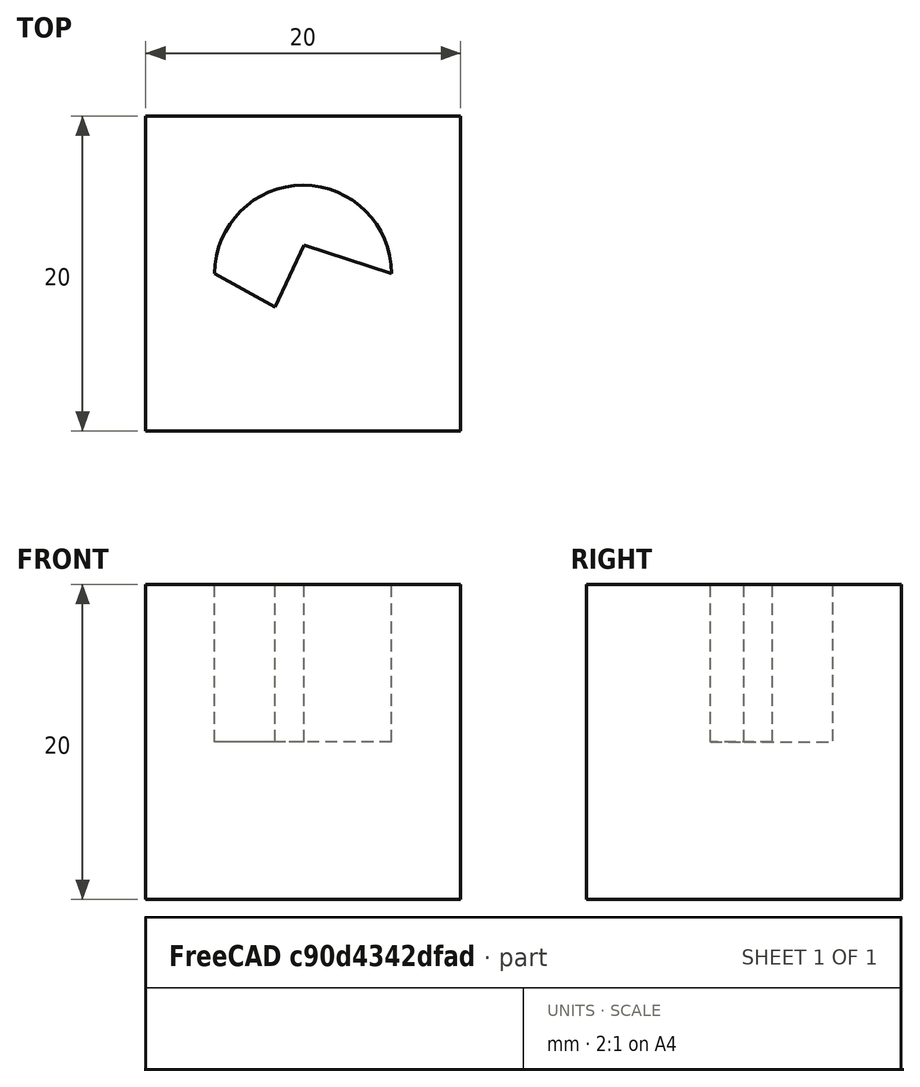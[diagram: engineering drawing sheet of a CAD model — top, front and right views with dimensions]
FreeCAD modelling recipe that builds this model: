
FCSTD DOCUMENT  (FreeCAD 0.21R33694 (Git))
Label: extrudeLimitation-1
License: All rights reserved
LicenseURL: http://en.wikipedia.org/wiki/All_rights_reserved
objects: App::DocumentObjectGroupPython×1248, App::Part×2, Part::FeaturePython×1, Sketcher::SketchObject×1, Part::Extrusion×1
note: 3 computed .brp shape members not serialized (recipe doc carries the construction recipe); baked Part::Feature solids carry a one-line shape summary decoded from their .brp

FEATURE [App::DocumentObjectGroupPython] HALFPI  # scripted group (container) (typed FeaturePython)
  name = HALFPI
  value = pi/2.
FEATURE [App::DocumentObjectGroupPython] PI  # scripted group (container) (typed FeaturePython)
  name = PI
  value = 1.*pi
FEATURE [App::DocumentObjectGroupPython] TWOPI  # scripted group (container) (typed FeaturePython)
  name = TWOPI
  value = 2.*pi
FEATURE [App::DocumentObjectGroupPython] Constants  # scripted group (container) (typed FeaturePython)
  Group = -> [HALFPI,PI,TWOPI]
FEATURE [App::DocumentObjectGroupPython] Variables  # scripted group (container) (typed FeaturePython)
FEATURE [App::DocumentObjectGroupPython] Quantities  # scripted group (container) (typed FeaturePython)
FEATURE [App::DocumentObjectGroupPython] Isotopes  # scripted group (container) (typed FeaturePython)
FEATURE [App::DocumentObjectGroupPython] Elements  # scripted group (container) (typed FeaturePython)
FEATURE [App::DocumentObjectGroupPython] G4Isotopes  # scripted group (container) (typed FeaturePython)
FEATURE [App::DocumentObjectGroupPython] H_element  # scripted group (container) (typed FeaturePython)
  Z = 1
  atom_value = 1.008
  formula = H
  name = H_element
FEATURE [App::DocumentObjectGroupPython] He_element  # scripted group (container) (typed FeaturePython)
  Z = 2
  atom_value = 4.0026
  formula = He
  name = He_element
FEATURE [App::DocumentObjectGroupPython] Li_element  # scripted group (container) (typed FeaturePython)
  Z = 3
  atom_value = 6.94
  formula = Li
  name = Li_element
FEATURE [App::DocumentObjectGroupPython] Be_element  # scripted group (container) (typed FeaturePython)
  Z = 4
  atom_value = 9.01218
  formula = Be
  name = Be_element
FEATURE [App::DocumentObjectGroupPython] B_element  # scripted group (container) (typed FeaturePython)
  Z = 5
  atom_value = 10.81
  formula = B
  name = B_element
FEATURE [App::DocumentObjectGroupPython] C_element  # scripted group (container) (typed FeaturePython)
  Z = 6
  atom_value = 12.011
  formula = C
  name = C_element
FEATURE [App::DocumentObjectGroupPython] N_element  # scripted group (container) (typed FeaturePython)
  Z = 7
  atom_value = 14.007
  formula = N
  name = N_element
FEATURE [App::DocumentObjectGroupPython] O_element  # scripted group (container) (typed FeaturePython)
  Z = 8
  atom_value = 15.999
  formula = O
  name = O_element
FEATURE [App::DocumentObjectGroupPython] F_element  # scripted group (container) (typed FeaturePython)
  Z = 9
  atom_value = 18.9984
  formula = F
  name = F_element
FEATURE [App::DocumentObjectGroupPython] Ne_element  # scripted group (container) (typed FeaturePython)
  Z = 10
  atom_value = 20.1797
  formula = Ne
  name = Ne_element
FEATURE [App::DocumentObjectGroupPython] Na_element  # scripted group (container) (typed FeaturePython)
  Z = 11
  atom_value = 22.9898
  formula = Na
  name = Na_element
FEATURE [App::DocumentObjectGroupPython] Mg_element  # scripted group (container) (typed FeaturePython)
  Z = 12
  atom_value = 24.305
  formula = Mg
  name = Mg_element
FEATURE [App::DocumentObjectGroupPython] Al_element  # scripted group (container) (typed FeaturePython)
  Z = 13
  atom_value = 26.9815
  formula = Al
  name = Al_element
FEATURE [App::DocumentObjectGroupPython] Si_element  # scripted group (container) (typed FeaturePython)
  Z = 14
  atom_value = 28.085
  formula = Si
  name = Si_element
FEATURE [App::DocumentObjectGroupPython] P_element  # scripted group (container) (typed FeaturePython)
  Z = 15
  atom_value = 30.9738
  formula = P
  name = P_element
FEATURE [App::DocumentObjectGroupPython] S_element  # scripted group (container) (typed FeaturePython)
  Z = 16
  atom_value = 32.06
  formula = S
  name = S_element
FEATURE [App::DocumentObjectGroupPython] Cl_element  # scripted group (container) (typed FeaturePython)
  Z = 17
  atom_value = 35.45
  formula = Cl
  name = Cl_element
FEATURE [App::DocumentObjectGroupPython] Ar_element  # scripted group (container) (typed FeaturePython)
  Z = 18
  atom_value = 39.95
  formula = Ar
  name = Ar_element
FEATURE [App::DocumentObjectGroupPython] K_element  # scripted group (container) (typed FeaturePython)
  Z = 19
  atom_value = 39.0983
  formula = K
  name = K_element
FEATURE [App::DocumentObjectGroupPython] Ca_element  # scripted group (container) (typed FeaturePython)
  Z = 20
  atom_value = 40.078
  formula = Ca
  name = Ca_element
FEATURE [App::DocumentObjectGroupPython] Sc_element  # scripted group (container) (typed FeaturePython)
  Z = 21
  atom_value = 44.9559
  formula = Sc
  name = Sc_element
FEATURE [App::DocumentObjectGroupPython] Ti_element  # scripted group (container) (typed FeaturePython)
  Z = 22
  atom_value = 47.867
  formula = Ti
  name = Ti_element
FEATURE [App::DocumentObjectGroupPython] V_element  # scripted group (container) (typed FeaturePython)
  Z = 23
  atom_value = 50.9415
  formula = V
  name = V_element
FEATURE [App::DocumentObjectGroupPython] Cr_element  # scripted group (container) (typed FeaturePython)
  Z = 24
  atom_value = 51.9961
  formula = Cr
  name = Cr_element
FEATURE [App::DocumentObjectGroupPython] Mn_element  # scripted group (container) (typed FeaturePython)
  Z = 25
  atom_value = 54.938
  formula = Mn
  name = Mn_element
FEATURE [App::DocumentObjectGroupPython] Fe_element  # scripted group (container) (typed FeaturePython)
  Z = 26
  atom_value = 55.845
  formula = Fe
  name = Fe_element
FEATURE [App::DocumentObjectGroupPython] Co_element  # scripted group (container) (typed FeaturePython)
  Z = 27
  atom_value = 58.9332
  formula = Co
  name = Co_element
FEATURE [App::DocumentObjectGroupPython] Ni_element  # scripted group (container) (typed FeaturePython)
  Z = 28
  atom_value = 58.6934
  formula = Ni
  name = Ni_element
FEATURE [App::DocumentObjectGroupPython] Cu_element  # scripted group (container) (typed FeaturePython)
  Z = 29
  atom_value = 63.546
  formula = Cu
  name = Cu_element
FEATURE [App::DocumentObjectGroupPython] Zn_element  # scripted group (container) (typed FeaturePython)
  Z = 30
  atom_value = 65.38
  formula = Zn
  name = Zn_element
FEATURE [App::DocumentObjectGroupPython] Ga_element  # scripted group (container) (typed FeaturePython)
  Z = 31
  atom_value = 69.723
  formula = Ga
  name = Ga_element
FEATURE [App::DocumentObjectGroupPython] Ge_element  # scripted group (container) (typed FeaturePython)
  Z = 32
  atom_value = 72.63
  formula = Ge
  name = Ge_element
FEATURE [App::DocumentObjectGroupPython] As_element  # scripted group (container) (typed FeaturePython)
  Z = 33
  atom_value = 74.9216
  formula = As
  name = As_element
FEATURE [App::DocumentObjectGroupPython] Se_element  # scripted group (container) (typed FeaturePython)
  Z = 34
  atom_value = 78.971
  formula = Se
  name = Se_element
FEATURE [App::DocumentObjectGroupPython] Br_element  # scripted group (container) (typed FeaturePython)
  Z = 35
  atom_value = 79.904
  formula = Br
  name = Br_element
FEATURE [App::DocumentObjectGroupPython] Kr_element  # scripted group (container) (typed FeaturePython)
  Z = 36
  atom_value = 83.798
  formula = Kr
  name = Kr_element
FEATURE [App::DocumentObjectGroupPython] Rb_element  # scripted group (container) (typed FeaturePython)
  Z = 37
  atom_value = 85.4678
  formula = Rb
  name = Rb_element
FEATURE [App::DocumentObjectGroupPython] Sr_element  # scripted group (container) (typed FeaturePython)
  Z = 38
  atom_value = 87.62
  formula = Sr
  name = Sr_element
FEATURE [App::DocumentObjectGroupPython] Y_element  # scripted group (container) (typed FeaturePython)
  Z = 39
  atom_value = 88.9058
  formula = Y
  name = Y_element
FEATURE [App::DocumentObjectGroupPython] Zr_element  # scripted group (container) (typed FeaturePython)
  Z = 40
  atom_value = 91.224
  formula = Zr
  name = Zr_element
FEATURE [App::DocumentObjectGroupPython] Nb_element  # scripted group (container) (typed FeaturePython)
  Z = 41
  atom_value = 92.9064
  formula = Nb
  name = Nb_element
FEATURE [App::DocumentObjectGroupPython] Mo_element  # scripted group (container) (typed FeaturePython)
  Z = 42
  atom_value = 95.95
  formula = Mo
  name = Mo_element
FEATURE [App::DocumentObjectGroupPython] Tc_element  # scripted group (container) (typed FeaturePython)
  Z = 43
  atom_value = 97
  formula = Tc
  name = Tc_element
FEATURE [App::DocumentObjectGroupPython] Ru_element  # scripted group (container) (typed FeaturePython)
  Z = 44
  atom_value = 101.07
  formula = Ru
  name = Ru_element
FEATURE [App::DocumentObjectGroupPython] Rh_element  # scripted group (container) (typed FeaturePython)
  Z = 45
  atom_value = 102.905
  formula = Rh
  name = Rh_element
FEATURE [App::DocumentObjectGroupPython] Pd_element  # scripted group (container) (typed FeaturePython)
  Z = 46
  atom_value = 106.42
  formula = Pd
  name = Pd_element
FEATURE [App::DocumentObjectGroupPython] Ag_element  # scripted group (container) (typed FeaturePython)
  Z = 47
  atom_value = 107.868
  formula = Ag
  name = Ag_element
FEATURE [App::DocumentObjectGroupPython] Cd_element  # scripted group (container) (typed FeaturePython)
  Z = 48
  atom_value = 112.414
  formula = Cd
  name = Cd_element
FEATURE [App::DocumentObjectGroupPython] In_element  # scripted group (container) (typed FeaturePython)
  Z = 49
  atom_value = 114.818
  formula = In
  name = In_element
FEATURE [App::DocumentObjectGroupPython] Sn_element  # scripted group (container) (typed FeaturePython)
  Z = 50
  atom_value = 118.71
  formula = Sn
  name = Sn_element
FEATURE [App::DocumentObjectGroupPython] Sb_element  # scripted group (container) (typed FeaturePython)
  Z = 51
  atom_value = 121.76
  formula = Sb
  name = Sb_element
FEATURE [App::DocumentObjectGroupPython] Te_element  # scripted group (container) (typed FeaturePython)
  Z = 52
  atom_value = 127.6
  formula = Te
  name = Te_element
FEATURE [App::DocumentObjectGroupPython] I_element  # scripted group (container) (typed FeaturePython)
  Z = 53
  atom_value = 126.904
  formula = I
  name = I_element
FEATURE [App::DocumentObjectGroupPython] Xe_element  # scripted group (container) (typed FeaturePython)
  Z = 54
  atom_value = 131.293
  formula = Xe
  name = Xe_element
FEATURE [App::DocumentObjectGroupPython] Cs_element  # scripted group (container) (typed FeaturePython)
  Z = 55
  atom_value = 132.905
  formula = Cs
  name = Cs_element
FEATURE [App::DocumentObjectGroupPython] Ba_element  # scripted group (container) (typed FeaturePython)
  Z = 56
  atom_value = 137.327
  formula = Ba
  name = Ba_element
FEATURE [App::DocumentObjectGroupPython] La_element  # scripted group (container) (typed FeaturePython)
  Z = 57
  atom_value = 138.905
  formula = La
  name = La_element
FEATURE [App::DocumentObjectGroupPython] Ce_element  # scripted group (container) (typed FeaturePython)
  Z = 58
  atom_value = 140.116
  formula = Ce
  name = Ce_element
FEATURE [App::DocumentObjectGroupPython] Pr_element  # scripted group (container) (typed FeaturePython)
  Z = 59
  atom_value = 140.908
  formula = Pr
  name = Pr_element
FEATURE [App::DocumentObjectGroupPython] Nd_element  # scripted group (container) (typed FeaturePython)
  Z = 60
  atom_value = 144.242
  formula = Nd
  name = Nd_element
FEATURE [App::DocumentObjectGroupPython] Pm_element  # scripted group (container) (typed FeaturePython)
  Z = 61
  atom_value = 145
  formula = Pm
  name = Pm_element
FEATURE [App::DocumentObjectGroupPython] Sm_element  # scripted group (container) (typed FeaturePython)
  Z = 62
  atom_value = 150.36
  formula = Sm
  name = Sm_element
FEATURE [App::DocumentObjectGroupPython] Eu_element  # scripted group (container) (typed FeaturePython)
  Z = 63
  atom_value = 151.964
  formula = Eu
  name = Eu_element
FEATURE [App::DocumentObjectGroupPython] Gd_element  # scripted group (container) (typed FeaturePython)
  Z = 64
  atom_value = 157.25
  formula = Gd
  name = Gd_element
FEATURE [App::DocumentObjectGroupPython] Tb_element  # scripted group (container) (typed FeaturePython)
  Z = 65
  atom_value = 158.925
  formula = Tb
  name = Tb_element
FEATURE [App::DocumentObjectGroupPython] Dy_element  # scripted group (container) (typed FeaturePython)
  Z = 66
  atom_value = 162.5
  formula = Dy
  name = Dy_element
FEATURE [App::DocumentObjectGroupPython] Ho_element  # scripted group (container) (typed FeaturePython)
  Z = 67
  atom_value = 164.93
  formula = Ho
  name = Ho_element
FEATURE [App::DocumentObjectGroupPython] Er_element  # scripted group (container) (typed FeaturePython)
  Z = 68
  atom_value = 167.259
  formula = Er
  name = Er_element
FEATURE [App::DocumentObjectGroupPython] Tm_element  # scripted group (container) (typed FeaturePython)
  Z = 69
  atom_value = 168.934
  formula = Tm
  name = Tm_element
FEATURE [App::DocumentObjectGroupPython] Yb_element  # scripted group (container) (typed FeaturePython)
  Z = 70
  atom_value = 173.045
  formula = Yb
  name = Yb_element
FEATURE [App::DocumentObjectGroupPython] Lu_element  # scripted group (container) (typed FeaturePython)
  Z = 71
  atom_value = 174.967
  formula = Lu
  name = Lu_element
FEATURE [App::DocumentObjectGroupPython] Hf_element  # scripted group (container) (typed FeaturePython)
  Z = 72
  atom_value = 178.49
  formula = Hf
  name = Hf_element
FEATURE [App::DocumentObjectGroupPython] Ta_element  # scripted group (container) (typed FeaturePython)
  Z = 73
  atom_value = 180.948
  formula = Ta
  name = Ta_element
FEATURE [App::DocumentObjectGroupPython] W_element  # scripted group (container) (typed FeaturePython)
  Z = 74
  atom_value = 183.84
  formula = W
  name = W_element
FEATURE [App::DocumentObjectGroupPython] Re_element  # scripted group (container) (typed FeaturePython)
  Z = 75
  atom_value = 186.207
  formula = Re
  name = Re_element
FEATURE [App::DocumentObjectGroupPython] Os_element  # scripted group (container) (typed FeaturePython)
  Z = 76
  atom_value = 190.23
  formula = Os
  name = Os_element
FEATURE [App::DocumentObjectGroupPython] Ir_element  # scripted group (container) (typed FeaturePython)
  Z = 77
  atom_value = 192.217
  formula = Ir
  name = Ir_element
FEATURE [App::DocumentObjectGroupPython] Pt_element  # scripted group (container) (typed FeaturePython)
  Z = 78
  atom_value = 195.084
  formula = Pt
  name = Pt_element
FEATURE [App::DocumentObjectGroupPython] Au_element  # scripted group (container) (typed FeaturePython)
  Z = 79
  atom_value = 196.967
  formula = Au
  name = Au_element
FEATURE [App::DocumentObjectGroupPython] Hg_element  # scripted group (container) (typed FeaturePython)
  Z = 80
  atom_value = 200.592
  formula = Hg
  name = Hg_element
FEATURE [App::DocumentObjectGroupPython] Tl_element  # scripted group (container) (typed FeaturePython)
  Z = 81
  atom_value = 204.38
  formula = Tl
  name = Tl_element
FEATURE [App::DocumentObjectGroupPython] Pb_element  # scripted group (container) (typed FeaturePython)
  Z = 82
  atom_value = 207.2
  formula = Pb
  name = Pb_element
FEATURE [App::DocumentObjectGroupPython] Bi_element  # scripted group (container) (typed FeaturePython)
  Z = 83
  atom_value = 208.98
  formula = Bi
  name = Bi_element
FEATURE [App::DocumentObjectGroupPython] Po_element  # scripted group (container) (typed FeaturePython)
  Z = 84
  atom_value = 209
  formula = Po
  name = Po_element
FEATURE [App::DocumentObjectGroupPython] At_element  # scripted group (container) (typed FeaturePython)
  Z = 85
  atom_value = 210
  formula = At
  name = At_element
FEATURE [App::DocumentObjectGroupPython] Rn_element  # scripted group (container) (typed FeaturePython)
  Z = 86
  atom_value = 222
  formula = Rn
  name = Rn_element
FEATURE [App::DocumentObjectGroupPython] Fr_element  # scripted group (container) (typed FeaturePython)
  Z = 87
  atom_value = 223
  formula = Fr
  name = Fr_element
FEATURE [App::DocumentObjectGroupPython] Ra_element  # scripted group (container) (typed FeaturePython)
  Z = 88
  atom_value = 226
  formula = Ra
  name = Ra_element
FEATURE [App::DocumentObjectGroupPython] Ac_element  # scripted group (container) (typed FeaturePython)
  Z = 89
  atom_value = 227
  formula = Ac
  name = Ac_element
FEATURE [App::DocumentObjectGroupPython] Th_element  # scripted group (container) (typed FeaturePython)
  Z = 90
  atom_value = 232.038
  formula = Th
  name = Th_element
FEATURE [App::DocumentObjectGroupPython] Pa_element  # scripted group (container) (typed FeaturePython)
  Z = 91
  atom_value = 231.036
  formula = Pa
  name = Pa_element
FEATURE [App::DocumentObjectGroupPython] U_element  # scripted group (container) (typed FeaturePython)
  Z = 92
  atom_value = 238.029
  formula = U
  name = U_element
FEATURE [App::DocumentObjectGroupPython] Np_element  # scripted group (container) (typed FeaturePython)
  Z = 93
  atom_value = 237
  formula = Np
  name = Np_element
FEATURE [App::DocumentObjectGroupPython] Pu_element  # scripted group (container) (typed FeaturePython)
  Z = 94
  atom_value = 244
  formula = Pu
  name = Pu_element
FEATURE [App::DocumentObjectGroupPython] Am_element  # scripted group (container) (typed FeaturePython)
  Z = 95
  atom_value = 243
  formula = Am
  name = Am_element
FEATURE [App::DocumentObjectGroupPython] Cm_element  # scripted group (container) (typed FeaturePython)
  Z = 96
  atom_value = 247
  formula = Cm
  name = Cm_element
FEATURE [App::DocumentObjectGroupPython] Bk_element  # scripted group (container) (typed FeaturePython)
  Z = 97
  atom_value = 247
  formula = Bk
  name = Bk_element
FEATURE [App::DocumentObjectGroupPython] Cf_element  # scripted group (container) (typed FeaturePython)
  Z = 98
  atom_value = 251
  formula = Cf
  name = Cf_element
FEATURE [App::DocumentObjectGroupPython] G4Elements  # scripted group (container) (typed FeaturePython)
  Group = -> [H_element,He_element,Li_element,Be_element,B_element,C_element,N_element,O_element,F_element,Ne_element,Na_element,Mg_element,Al_element,Si_element,P_element,S_element,Cl_element,Ar_element,K_element,Ca_element,Sc_element,Ti_element,V_element,Cr_element,Mn_element,Fe_element,Co_element,Ni_element,Cu_element,Zn_element,Ga_element,Ge_element,As_element,Se_element,Br_element,Kr_element,Rb_element,+61 more]
FEATURE [App::DocumentObjectGroupPython] H_element001  label="H_element : 0.101"  # scripted group (container) (typed FeaturePython)
  n = 0.101327
FEATURE [App::DocumentObjectGroupPython] C_element001  label="C_element : 0.775"  # scripted group (container) (typed FeaturePython)
  n = 0.7755
FEATURE [App::DocumentObjectGroupPython] N_element001  label="N_element : 0.035"  # scripted group (container) (typed FeaturePython)
  n = 0.035057
FEATURE [App::DocumentObjectGroupPython] O_element001  label="O_element : 0.052"  # scripted group (container) (typed FeaturePython)
  n = 0.0523159
FEATURE [App::DocumentObjectGroupPython] F_element001  label="F_element : 0.017"  # scripted group (container) (typed FeaturePython)
  n = 0.017422
FEATURE [App::DocumentObjectGroupPython] Ca_element001  label="Ca_element : 0.018"  # scripted group (container) (typed FeaturePython)
  n = 0.018378
FEATURE [App::DocumentObjectGroupPython] G4_A_150_TISSUE  label="G4_A-150_TISSUE"  # scripted group (container) (typed FeaturePython)
  Dunit = g/cm3
  Dvalue = 1.127
  Group = -> [H_element001,C_element001,N_element001,O_element001,F_element001,Ca_element001]
  conduct = 2
  density = 1
  expand = 3
  formula = G4_A-150_TISSUE
  name = G4_A-150_TISSUE
  specific = 4
FEATURE [App::DocumentObjectGroupPython] C_element002  label="C_element : 3"  # scripted group (container) (typed FeaturePython)
  n = 3
  ref = C_element
FEATURE [App::DocumentObjectGroupPython] H_element002  label="H_element : 6"  # scripted group (container) (typed FeaturePython)
  n = 6
  ref = H_element
FEATURE [App::DocumentObjectGroupPython] O_element002  label="O_element : 1"  # scripted group (container) (typed FeaturePython)
  n = 1
  ref = O_element
FEATURE [App::DocumentObjectGroupPython] G4_ACETONE  # scripted group (container) (typed FeaturePython)
  Dunit = g/cm3
  Dvalue = 0.7899
  Group = -> [C_element002,H_element002,O_element002]
  conduct = 2
  density = 1
  expand = 3
  formula = G4_ACETONE
  name = G4_ACETONE
  specific = 4
FEATURE [App::DocumentObjectGroupPython] C_element003  label="C_element : 2"  # scripted group (container) (typed FeaturePython)
  n = 2
  ref = C_element
FEATURE [App::DocumentObjectGroupPython] H_element003  label="H_element : 2"  # scripted group (container) (typed FeaturePython)
  n = 2
  ref = H_element
FEATURE [App::DocumentObjectGroupPython] G4_ACETYLENE  # scripted group (container) (typed FeaturePython)
  Dunit = g/cm3
  Dvalue = 0.0010967
  Group = -> [C_element003,H_element003]
  conduct = 2
  density = 1
  expand = 3
  formula = G4_ACETYLENE
  name = G4_ACETYLENE
  specific = 4
FEATURE [App::DocumentObjectGroupPython] C_element004  label="C_element : 5"  # scripted group (container) (typed FeaturePython)
  n = 5
  ref = C_element
FEATURE [App::DocumentObjectGroupPython] H_element004  label="H_element : 5"  # scripted group (container) (typed FeaturePython)
  n = 5
  ref = H_element
FEATURE [App::DocumentObjectGroupPython] N_element002  label="N_element : 5"  # scripted group (container) (typed FeaturePython)
  n = 5
  ref = N_element
FEATURE [App::DocumentObjectGroupPython] G4_ADENINE  # scripted group (container) (typed FeaturePython)
  Dunit = g/cm3
  Dvalue = 1.6
  Group = -> [C_element004,H_element004,N_element002]
  conduct = 2
  density = 1
  expand = 3
  formula = G4_ADENINE
  name = G4_ADENINE
  specific = 4
FEATURE [App::DocumentObjectGroupPython] H_element005  label="H_element : 0.114"  # scripted group (container) (typed FeaturePython)
  n = 0.114
FEATURE [App::DocumentObjectGroupPython] C_element005  label="C_element : 0.598"  # scripted group (container) (typed FeaturePython)
  n = 0.598
FEATURE [App::DocumentObjectGroupPython] N_element003  label="N_element : 0.007"  # scripted group (container) (typed FeaturePython)
  n = 0.007
FEATURE [App::DocumentObjectGroupPython] O_element003  label="O_element : 0.278"  # scripted group (container) (typed FeaturePython)
  n = 0.278
FEATURE [App::DocumentObjectGroupPython] Na_element001  label="Na_element : 0.001"  # scripted group (container) (typed FeaturePython)
  n = 0.001
FEATURE [App::DocumentObjectGroupPython] S_element001  label="S_element : 0.001"  # scripted group (container) (typed FeaturePython)
  n = 0.001
FEATURE [App::DocumentObjectGroupPython] Cl_element001  label="Cl_element : 0.001"  # scripted group (container) (typed FeaturePython)
  n = 0.001
FEATURE [App::DocumentObjectGroupPython] G4_ADIPOSE_TISSUE_ICRP  # scripted group (container) (typed FeaturePython)
  Dunit = g/cm3
  Dvalue = 0.95
  Group = -> [H_element005,C_element005,N_element003,O_element003,Na_element001,S_element001,Cl_element001]
  conduct = 2
  density = 1
  expand = 3
  formula = G4_ADIPOSE_TISSUE_ICRP
  name = G4_ADIPOSE_TISSUE_ICRP
  specific = 4
FEATURE [App::DocumentObjectGroupPython] C_element006  label="C_element : 0.000"  # scripted group (container) (typed FeaturePython)
  n = 0.000124
FEATURE [App::DocumentObjectGroupPython] N_element004  label="N_element : 0.755"  # scripted group (container) (typed FeaturePython)
  n = 0.755268
FEATURE [App::DocumentObjectGroupPython] O_element004  label="O_element : 0.232"  # scripted group (container) (typed FeaturePython)
  n = 0.231781
FEATURE [App::DocumentObjectGroupPython] Ar_element001  label="Ar_element : 0.013"  # scripted group (container) (typed FeaturePython)
  n = 0.012827
FEATURE [App::DocumentObjectGroupPython] G4_AIR  # scripted group (container) (typed FeaturePython)
  Dunit = g/cm3
  Dvalue = 0.00120479
  Group = -> [C_element006,N_element004,O_element004,Ar_element001]
  conduct = 2
  density = 1
  expand = 3
  formula = G4_AIR
  name = G4_AIR
  specific = 4
FEATURE [App::DocumentObjectGroupPython] C_element007  label="C_element : 006"  # scripted group (container) (typed FeaturePython)
  n = 3
  ref = C_element
FEATURE [App::DocumentObjectGroupPython] H_element006  label="H_element : 7"  # scripted group (container) (typed FeaturePython)
  n = 7
  ref = H_element
FEATURE [App::DocumentObjectGroupPython] N_element005  label="N_element : 1"  # scripted group (container) (typed FeaturePython)
  n = 1
  ref = N_element
FEATURE [App::DocumentObjectGroupPython] O_element005  label="O_element : 2"  # scripted group (container) (typed FeaturePython)
  n = 2
  ref = O_element
FEATURE [App::DocumentObjectGroupPython] G4_ALANINE  # scripted group (container) (typed FeaturePython)
  Dunit = g/cm3
  Dvalue = 1.42
  Group = -> [C_element007,H_element006,N_element005,O_element005]
  conduct = 2
  density = 1
  expand = 3
  formula = G4_ALANINE
  name = G4_ALANINE
  specific = 4
FEATURE [App::DocumentObjectGroupPython] Al_element001  label="Al_element : 2"  # scripted group (container) (typed FeaturePython)
  n = 2
  ref = Al_element
FEATURE [App::DocumentObjectGroupPython] O_element006  label="O_element : 3"  # scripted group (container) (typed FeaturePython)
  n = 3
  ref = O_element
FEATURE [App::DocumentObjectGroupPython] G4_ALUMINUM_OXIDE  # scripted group (container) (typed FeaturePython)
  Dunit = g/cm3
  Dvalue = 3.97
  Group = -> [Al_element001,O_element006]
  conduct = 2
  density = 1
  expand = 3
  formula = G4_ALUMINUM_OXIDE
  name = G4_ALUMINUM_OXIDE
  specific = 4
FEATURE [App::DocumentObjectGroupPython] H_element007  label="H_element : 0.106"  # scripted group (container) (typed FeaturePython)
  n = 0.10593
FEATURE [App::DocumentObjectGroupPython] C_element008  label="C_element : 0.789"  # scripted group (container) (typed FeaturePython)
  n = 0.788974
FEATURE [App::DocumentObjectGroupPython] O_element007  label="O_element : 0.105"  # scripted group (container) (typed FeaturePython)
  n = 0.105096
FEATURE [App::DocumentObjectGroupPython] G4_AMBER  # scripted group (container) (typed FeaturePython)
  Dunit = g/cm3
  Dvalue = 1.1
  Group = -> [H_element007,C_element008,O_element007]
  conduct = 2
  density = 1
  expand = 3
  formula = G4_AMBER
  name = G4_AMBER
  specific = 4
FEATURE [App::DocumentObjectGroupPython] N_element006  label="N_element : 006"  # scripted group (container) (typed FeaturePython)
  n = 1
  ref = N_element
FEATURE [App::DocumentObjectGroupPython] H_element008  label="H_element : 3"  # scripted group (container) (typed FeaturePython)
  n = 3
  ref = H_element
FEATURE [App::DocumentObjectGroupPython] G4_AMMONIA  # scripted group (container) (typed FeaturePython)
  Dunit = g/cm3
  Dvalue = 0.000826019
  Group = -> [N_element006,H_element008]
  conduct = 2
  density = 1
  expand = 3
  formula = G4_AMMONIA
  name = G4_AMMONIA
  specific = 4
FEATURE [App::DocumentObjectGroupPython] C_element009  label="C_element : 6"  # scripted group (container) (typed FeaturePython)
  n = 6
  ref = C_element
FEATURE [App::DocumentObjectGroupPython] H_element009  label="H_element : 008"  # scripted group (container) (typed FeaturePython)
  n = 7
  ref = H_element
FEATURE [App::DocumentObjectGroupPython] N_element007  label="N_element : 007"  # scripted group (container) (typed FeaturePython)
  n = 1
  ref = N_element
FEATURE [App::DocumentObjectGroupPython] G4_ANILINE  # scripted group (container) (typed FeaturePython)
  Dunit = g/cm3
  Dvalue = 1.0235
  Group = -> [C_element009,H_element009,N_element007]
  conduct = 2
  density = 1
  expand = 3
  formula = G4_ANILINE
  name = G4_ANILINE
  specific = 4
FEATURE [App::DocumentObjectGroupPython] C_element010  label="C_element : 14"  # scripted group (container) (typed FeaturePython)
  n = 14
  ref = C_element
FEATURE [App::DocumentObjectGroupPython] H_element010  label="H_element : 10"  # scripted group (container) (typed FeaturePython)
  n = 10
  ref = H_element
FEATURE [App::DocumentObjectGroupPython] G4_ANTHRACENE  # scripted group (container) (typed FeaturePython)
  Dunit = g/cm3
  Dvalue = 1.283
  Group = -> [C_element010,H_element010]
  conduct = 2
  density = 1
  expand = 3
  formula = G4_ANTHRACENE
  name = G4_ANTHRACENE
  specific = 4
FEATURE [App::DocumentObjectGroupPython] H_element011  label="H_element : 0.065"  # scripted group (container) (typed FeaturePython)
  n = 0.0654709
FEATURE [App::DocumentObjectGroupPython] C_element011  label="C_element : 0.537"  # scripted group (container) (typed FeaturePython)
  n = 0.536944
FEATURE [App::DocumentObjectGroupPython] N_element008  label="N_element : 0.021"  # scripted group (container) (typed FeaturePython)
  n = 0.0215
FEATURE [App::DocumentObjectGroupPython] O_element008  label="O_element : 0.032"  # scripted group (container) (typed FeaturePython)
  n = 0.032085
FEATURE [App::DocumentObjectGroupPython] F_element002  label="F_element : 0.167"  # scripted group (container) (typed FeaturePython)
  n = 0.167411
FEATURE [App::DocumentObjectGroupPython] Ca_element002  label="Ca_element : 0.177"  # scripted group (container) (typed FeaturePython)
  n = 0.176589
FEATURE [App::DocumentObjectGroupPython] G4_B_100_BONE  label="G4_B-100_BONE"  # scripted group (container) (typed FeaturePython)
  Dunit = g/cm3
  Dvalue = 1.45
  Group = -> [H_element011,C_element011,N_element008,O_element008,F_element002,Ca_element002]
  conduct = 2
  density = 1
  expand = 3
  formula = G4_B-100_BONE
  name = G4_B-100_BONE
  specific = 4
FEATURE [App::DocumentObjectGroupPython] H_element012  label="H_element : 0.057"  # scripted group (container) (typed FeaturePython)
  n = 0.057441
FEATURE [App::DocumentObjectGroupPython] C_element012  label="C_element : 0.790"  # scripted group (container) (typed FeaturePython)
  n = 0.774591
FEATURE [App::DocumentObjectGroupPython] O_element009  label="O_element : 0.168"  # scripted group (container) (typed FeaturePython)
  n = 0.167968
FEATURE [App::DocumentObjectGroupPython] G4_BAKELITE  # scripted group (container) (typed FeaturePython)
  Dunit = g/cm3
  Dvalue = 1.25
  Group = -> [H_element012,C_element012,O_element009]
  conduct = 2
  density = 1
  expand = 3
  formula = G4_BAKELITE
  name = G4_BAKELITE
  specific = 4
FEATURE [App::DocumentObjectGroupPython] Ba_element001  label="Ba_element : 1"  # scripted group (container) (typed FeaturePython)
  n = 1
  ref = Ba_element
FEATURE [App::DocumentObjectGroupPython] F_element003  label="F_element : 2"  # scripted group (container) (typed FeaturePython)
  n = 2
  ref = F_element
FEATURE [App::DocumentObjectGroupPython] G4_BARIUM_FLUORIDE  # scripted group (container) (typed FeaturePython)
  Dunit = g/cm3
  Dvalue = 4.89
  Group = -> [Ba_element001,F_element003]
  conduct = 2
  density = 1
  expand = 3
  formula = G4_BARIUM_FLUORIDE
  name = G4_BARIUM_FLUORIDE
  specific = 4
FEATURE [App::DocumentObjectGroupPython] Ba_element002  label="Ba_element : 002"  # scripted group (container) (typed FeaturePython)
  n = 1
  ref = Ba_element
FEATURE [App::DocumentObjectGroupPython] S_element002  label="S_element : 1"  # scripted group (container) (typed FeaturePython)
  n = 1
  ref = S_element
FEATURE [App::DocumentObjectGroupPython] O_element010  label="O_element : 4"  # scripted group (container) (typed FeaturePython)
  n = 4
  ref = O_element
FEATURE [App::DocumentObjectGroupPython] G4_BARIUM_SULFATE  # scripted group (container) (typed FeaturePython)
  Dunit = g/cm3
  Dvalue = 4.5
  Group = -> [Ba_element002,S_element002,O_element010]
  conduct = 2
  density = 1
  expand = 3
  formula = G4_BARIUM_SULFATE
  name = G4_BARIUM_SULFATE
  specific = 4
FEATURE [App::DocumentObjectGroupPython] C_element013  label="C_element : 007"  # scripted group (container) (typed FeaturePython)
  n = 6
  ref = C_element
FEATURE [App::DocumentObjectGroupPython] H_element013  label="H_element : 009"  # scripted group (container) (typed FeaturePython)
  n = 6
  ref = H_element
FEATURE [App::DocumentObjectGroupPython] G4_BENZENE  # scripted group (container) (typed FeaturePython)
  Dunit = g/cm3
  Dvalue = 0.87865
  Group = -> [C_element013,H_element013]
  conduct = 2
  density = 1
  expand = 3
  formula = G4_BENZENE
  name = G4_BENZENE
  specific = 4
FEATURE [App::DocumentObjectGroupPython] Be_element001  label="Be_element : 1"  # scripted group (container) (typed FeaturePython)
  n = 1
  ref = Be_element
FEATURE [App::DocumentObjectGroupPython] O_element011  label="O_element : 005"  # scripted group (container) (typed FeaturePython)
  n = 1
  ref = O_element
FEATURE [App::DocumentObjectGroupPython] G4_BERYLLIUM_OXIDE  # scripted group (container) (typed FeaturePython)
  Dunit = g/cm3
  Dvalue = 3.01
  Group = -> [Be_element001,O_element011]
  conduct = 2
  density = 1
  expand = 3
  formula = G4_BERYLLIUM_OXIDE
  name = G4_BERYLLIUM_OXIDE
  specific = 4
FEATURE [App::DocumentObjectGroupPython] Bi_element001  label="Bi_element : 4"  # scripted group (container) (typed FeaturePython)
  n = 4
  ref = Bi_element
FEATURE [App::DocumentObjectGroupPython] Ge_element001  label="Ge_element : 3"  # scripted group (container) (typed FeaturePython)
  n = 3
  ref = Ge_element
FEATURE [App::DocumentObjectGroupPython] O_element012  label="O_element : 12"  # scripted group (container) (typed FeaturePython)
  n = 12
  ref = O_element
FEATURE [App::DocumentObjectGroupPython] G4_BGO  # scripted group (container) (typed FeaturePython)
  Dunit = g/cm3
  Dvalue = 7.13
  Group = -> [Bi_element001,Ge_element001,O_element012]
  conduct = 2
  density = 1
  expand = 3
  formula = G4_BGO
  name = G4_BGO
  specific = 4
FEATURE [App::DocumentObjectGroupPython] H_element014  label="H_element : 0.102"  # scripted group (container) (typed FeaturePython)
  n = 0.102
FEATURE [App::DocumentObjectGroupPython] C_element014  label="C_element : 0.110"  # scripted group (container) (typed FeaturePython)
  n = 0.11
FEATURE [App::DocumentObjectGroupPython] N_element009  label="N_element : 0.033"  # scripted group (container) (typed FeaturePython)
  n = 0.033
FEATURE [App::DocumentObjectGroupPython] O_element013  label="O_element : 0.745"  # scripted group (container) (typed FeaturePython)
  n = 0.745
FEATURE [App::DocumentObjectGroupPython] Na_element002  label="Na_element : 0.002"  # scripted group (container) (typed FeaturePython)
  n = 0.001
FEATURE [App::DocumentObjectGroupPython] P_element001  label="P_element : 0.001"  # scripted group (container) (typed FeaturePython)
  n = 0.001
FEATURE [App::DocumentObjectGroupPython] S_element003  label="S_element : 0.002"  # scripted group (container) (typed FeaturePython)
  n = 0.002
FEATURE [App::DocumentObjectGroupPython] Cl_element002  label="Cl_element : 0.003"  # scripted group (container) (typed FeaturePython)
  n = 0.003
FEATURE [App::DocumentObjectGroupPython] K_element001  label="K_element : 0.002"  # scripted group (container) (typed FeaturePython)
  n = 0.002
FEATURE [App::DocumentObjectGroupPython] Fe_element001  label="Fe_element : 0.001"  # scripted group (container) (typed FeaturePython)
  n = 0.001
FEATURE [App::DocumentObjectGroupPython] G4_BLOOD_ICRP  # scripted group (container) (typed FeaturePython)
  Dunit = g/cm3
  Dvalue = 1.06
  Group = -> [H_element014,C_element014,N_element009,O_element013,Na_element002,P_element001,S_element003,Cl_element002,K_element001,Fe_element001]
  conduct = 2
  density = 1
  expand = 3
  formula = G4_BLOOD_ICRP
  name = G4_BLOOD_ICRP
  specific = 4
FEATURE [App::DocumentObjectGroupPython] H_element015  label="H_element : 0.064"  # scripted group (container) (typed FeaturePython)
  n = 0.064
FEATURE [App::DocumentObjectGroupPython] C_element015  label="C_element : 0.278"  # scripted group (container) (typed FeaturePython)
  n = 0.278
FEATURE [App::DocumentObjectGroupPython] N_element010  label="N_element : 0.027"  # scripted group (container) (typed FeaturePython)
  n = 0.027
FEATURE [App::DocumentObjectGroupPython] O_element014  label="O_element : 0.410"  # scripted group (container) (typed FeaturePython)
  n = 0.41
FEATURE [App::DocumentObjectGroupPython] Mg_element001  label="Mg_element : 0.002"  # scripted group (container) (typed FeaturePython)
  n = 0.002
FEATURE [App::DocumentObjectGroupPython] P_element002  label="P_element : 0.070"  # scripted group (container) (typed FeaturePython)
  n = 0.07
FEATURE [App::DocumentObjectGroupPython] S_element004  label="S_element : 0.003"  # scripted group (container) (typed FeaturePython)
  n = 0.002
FEATURE [App::DocumentObjectGroupPython] Ca_element003  label="Ca_element : 0.147"  # scripted group (container) (typed FeaturePython)
  n = 0.147
FEATURE [App::DocumentObjectGroupPython] G4_BONE_COMPACT_ICRU  # scripted group (container) (typed FeaturePython)
  Dunit = g/cm3
  Dvalue = 1.85
  Group = -> [H_element015,C_element015,N_element010,O_element014,Mg_element001,P_element002,S_element004,Ca_element003]
  conduct = 2
  density = 1
  expand = 3
  formula = G4_BONE_COMPACT_ICRU
  name = G4_BONE_COMPACT_ICRU
  specific = 4
FEATURE [App::DocumentObjectGroupPython] H_element016  label="H_element : 0.034"  # scripted group (container) (typed FeaturePython)
  n = 0.034
FEATURE [App::DocumentObjectGroupPython] C_element016  label="C_element : 0.155"  # scripted group (container) (typed FeaturePython)
  n = 0.155
FEATURE [App::DocumentObjectGroupPython] N_element011  label="N_element : 0.042"  # scripted group (container) (typed FeaturePython)
  n = 0.042
FEATURE [App::DocumentObjectGroupPython] O_element015  label="O_element : 0.435"  # scripted group (container) (typed FeaturePython)
  n = 0.435
FEATURE [App::DocumentObjectGroupPython] Na_element003  label="Na_element : 0.003"  # scripted group (container) (typed FeaturePython)
  n = 0.001
FEATURE [App::DocumentObjectGroupPython] Mg_element002  label="Mg_element : 0.003"  # scripted group (container) (typed FeaturePython)
  n = 0.002
FEATURE [App::DocumentObjectGroupPython] P_element003  label="P_element : 0.103"  # scripted group (container) (typed FeaturePython)
  n = 0.103
FEATURE [App::DocumentObjectGroupPython] S_element005  label="S_element : 0.004"  # scripted group (container) (typed FeaturePython)
  n = 0.003
FEATURE [App::DocumentObjectGroupPython] Ca_element004  label="Ca_element : 0.225"  # scripted group (container) (typed FeaturePython)
  n = 0.225
FEATURE [App::DocumentObjectGroupPython] G4_BONE_CORTICAL_ICRP  # scripted group (container) (typed FeaturePython)
  Dunit = g/cm3
  Dvalue = 1.92
  Group = -> [H_element016,C_element016,N_element011,O_element015,Na_element003,Mg_element002,P_element003,S_element005,Ca_element004]
  conduct = 2
  density = 1
  expand = 3
  formula = G4_BONE_CORTICAL_ICRP
  name = G4_BONE_CORTICAL_ICRP
  specific = 4
FEATURE [App::DocumentObjectGroupPython] B_element001  label="B_element : 4"  # scripted group (container) (typed FeaturePython)
  n = 4
  ref = B_element
FEATURE [App::DocumentObjectGroupPython] C_element017  label="C_element : 1"  # scripted group (container) (typed FeaturePython)
  n = 1
  ref = C_element
FEATURE [App::DocumentObjectGroupPython] G4_BORON_CARBIDE  # scripted group (container) (typed FeaturePython)
  Dunit = g/cm3
  Dvalue = 2.52
  Group = -> [B_element001,C_element017]
  conduct = 2
  density = 1
  expand = 3
  formula = G4_BORON_CARBIDE
  name = G4_BORON_CARBIDE
  specific = 4
FEATURE [App::DocumentObjectGroupPython] B_element002  label="B_element : 2"  # scripted group (container) (typed FeaturePython)
  n = 2
  ref = B_element
FEATURE [App::DocumentObjectGroupPython] O_element016  label="O_element : 006"  # scripted group (container) (typed FeaturePython)
  n = 3
  ref = O_element
FEATURE [App::DocumentObjectGroupPython] G4_BORON_OXIDE  # scripted group (container) (typed FeaturePython)
  Dunit = g/cm3
  Dvalue = 1.812
  Group = -> [B_element002,O_element016]
  conduct = 2
  density = 1
  expand = 3
  formula = G4_BORON_OXIDE
  name = G4_BORON_OXIDE
  specific = 4
FEATURE [App::DocumentObjectGroupPython] H_element017  label="H_element : 0.107"  # scripted group (container) (typed FeaturePython)
  n = 0.107
FEATURE [App::DocumentObjectGroupPython] C_element018  label="C_element : 0.145"  # scripted group (container) (typed FeaturePython)
  n = 0.145
FEATURE [App::DocumentObjectGroupPython] N_element012  label="N_element : 0.022"  # scripted group (container) (typed FeaturePython)
  n = 0.022
FEATURE [App::DocumentObjectGroupPython] O_element017  label="O_element : 0.712"  # scripted group (container) (typed FeaturePython)
  n = 0.712
FEATURE [App::DocumentObjectGroupPython] Na_element004  label="Na_element : 0.004"  # scripted group (container) (typed FeaturePython)
  n = 0.002
FEATURE [App::DocumentObjectGroupPython] P_element004  label="P_element : 0.004"  # scripted group (container) (typed FeaturePython)
  n = 0.004
FEATURE [App::DocumentObjectGroupPython] S_element006  label="S_element : 0.005"  # scripted group (container) (typed FeaturePython)
  n = 0.002
FEATURE [App::DocumentObjectGroupPython] Cl_element003  label="Cl_element : 0.004"  # scripted group (container) (typed FeaturePython)
  n = 0.003
FEATURE [App::DocumentObjectGroupPython] K_element002  label="K_element : 0.003"  # scripted group (container) (typed FeaturePython)
  n = 0.003
FEATURE [App::DocumentObjectGroupPython] G4_BRAIN_ICRP  # scripted group (container) (typed FeaturePython)
  Dunit = g/cm3
  Dvalue = 1.04
  Group = -> [H_element017,C_element018,N_element012,O_element017,Na_element004,P_element004,S_element006,Cl_element003,K_element002]
  conduct = 2
  density = 1
  expand = 3
  formula = G4_BRAIN_ICRP
  name = G4_BRAIN_ICRP
  specific = 4
FEATURE [App::DocumentObjectGroupPython] C_element019  label="C_element : 4"  # scripted group (container) (typed FeaturePython)
  n = 4
  ref = C_element
FEATURE [App::DocumentObjectGroupPython] H_element018  label="H_element : 010"  # scripted group (container) (typed FeaturePython)
  n = 10
  ref = H_element
FEATURE [App::DocumentObjectGroupPython] G4_BUTANE  # scripted group (container) (typed FeaturePython)
  Dunit = g/cm3
  Dvalue = 0.00249343
  Group = -> [C_element019,H_element018]
  conduct = 2
  density = 1
  expand = 3
  formula = G4_BUTANE
  name = G4_BUTANE
  specific = 4
FEATURE [App::DocumentObjectGroupPython] C_element020  label="C_element : 008"  # scripted group (container) (typed FeaturePython)
  n = 4
  ref = C_element
FEATURE [App::DocumentObjectGroupPython] H_element019  label="H_element : 011"  # scripted group (container) (typed FeaturePython)
  n = 10
  ref = H_element
FEATURE [App::DocumentObjectGroupPython] O_element018  label="O_element : 007"  # scripted group (container) (typed FeaturePython)
  n = 1
  ref = O_element
FEATURE [App::DocumentObjectGroupPython] G4_N_BUTYL_ALCOHOL  label="G4_N-BUTYL_ALCOHOL"  # scripted group (container) (typed FeaturePython)
  Dunit = g/cm3
  Dvalue = 0.8098
  Group = -> [C_element020,H_element019,O_element018]
  conduct = 2
  density = 1
  expand = 3
  formula = G4_N-BUTYL_ALCOHOL
  name = G4_N-BUTYL_ALCOHOL
  specific = 4
FEATURE [App::DocumentObjectGroupPython] H_element020  label="H_element : 0.025"  # scripted group (container) (typed FeaturePython)
  n = 0.02468
FEATURE [App::DocumentObjectGroupPython] C_element021  label="C_element : 0.502"  # scripted group (container) (typed FeaturePython)
  n = 0.501611
FEATURE [App::DocumentObjectGroupPython] O_element019  label="O_element : 0.005"  # scripted group (container) (typed FeaturePython)
  n = 0.004527
FEATURE [App::DocumentObjectGroupPython] F_element004  label="F_element : 0.465"  # scripted group (container) (typed FeaturePython)
  n = 0.465209
FEATURE [App::DocumentObjectGroupPython] Si_element001  label="Si_element : 0.004"  # scripted group (container) (typed FeaturePython)
  n = 0.003973
FEATURE [App::DocumentObjectGroupPython] G4_C_552  label="G4_C-552"  # scripted group (container) (typed FeaturePython)
  Dunit = g/cm3
  Dvalue = 1.76
  Group = -> [H_element020,C_element021,O_element019,F_element004,Si_element001]
  conduct = 2
  density = 1
  expand = 3
  formula = G4_C-552
  name = G4_C-552
  specific = 4
FEATURE [App::DocumentObjectGroupPython] Cd_element001  label="Cd_element : 1"  # scripted group (container) (typed FeaturePython)
  n = 1
  ref = Cd_element
FEATURE [App::DocumentObjectGroupPython] Te_element001  label="Te_element : 1"  # scripted group (container) (typed FeaturePython)
  n = 1
  ref = Te_element
FEATURE [App::DocumentObjectGroupPython] G4_CADMIUM_TELLURIDE  # scripted group (container) (typed FeaturePython)
  Dunit = g/cm3
  Dvalue = 6.2
  Group = -> [Cd_element001,Te_element001]
  conduct = 2
  density = 1
  expand = 3
  formula = G4_CADMIUM_TELLURIDE
  name = G4_CADMIUM_TELLURIDE
  specific = 4
FEATURE [App::DocumentObjectGroupPython] Cd_element002  label="Cd_element : 002"  # scripted group (container) (typed FeaturePython)
  n = 1
  ref = Cd_element
FEATURE [App::DocumentObjectGroupPython] W_element001  label="W_element : 1"  # scripted group (container) (typed FeaturePython)
  n = 1
  ref = W_element
FEATURE [App::DocumentObjectGroupPython] O_element020  label="O_element : 008"  # scripted group (container) (typed FeaturePython)
  n = 4
  ref = O_element
FEATURE [App::DocumentObjectGroupPython] G4_CADMIUM_TUNGSTATE  # scripted group (container) (typed FeaturePython)
  Dunit = g/cm3
  Dvalue = 7.9
  Group = -> [Cd_element002,W_element001,O_element020]
  conduct = 2
  density = 1
  expand = 3
  formula = G4_CADMIUM_TUNGSTATE
  name = G4_CADMIUM_TUNGSTATE
  specific = 4
FEATURE [App::DocumentObjectGroupPython] Ca_element005  label="Ca_element : 1"  # scripted group (container) (typed FeaturePython)
  n = 1
  ref = Ca_element
FEATURE [App::DocumentObjectGroupPython] C_element022  label="C_element : 009"  # scripted group (container) (typed FeaturePython)
  n = 1
  ref = C_element
FEATURE [App::DocumentObjectGroupPython] O_element021  label="O_element : 009"  # scripted group (container) (typed FeaturePython)
  n = 3
  ref = O_element
FEATURE [App::DocumentObjectGroupPython] G4_CALCIUM_CARBONATE  # scripted group (container) (typed FeaturePython)
  Dunit = g/cm3
  Dvalue = 2.8
  Group = -> [Ca_element005,C_element022,O_element021]
  conduct = 2
  density = 1
  expand = 3
  formula = G4_CALCIUM_CARBONATE
  name = G4_CALCIUM_CARBONATE
  specific = 4
FEATURE [App::DocumentObjectGroupPython] Ca_element006  label="Ca_element : 002"  # scripted group (container) (typed FeaturePython)
  n = 1
  ref = Ca_element
FEATURE [App::DocumentObjectGroupPython] F_element005  label="F_element : 003"  # scripted group (container) (typed FeaturePython)
  n = 2
  ref = F_element
FEATURE [App::DocumentObjectGroupPython] G4_CALCIUM_FLUORIDE  # scripted group (container) (typed FeaturePython)
  Dunit = g/cm3
  Dvalue = 3.18
  Group = -> [Ca_element006,F_element005]
  conduct = 2
  density = 1
  expand = 3
  formula = G4_CALCIUM_FLUORIDE
  name = G4_CALCIUM_FLUORIDE
  specific = 4
FEATURE [App::DocumentObjectGroupPython] Ca_element007  label="Ca_element : 003"  # scripted group (container) (typed FeaturePython)
  n = 1
  ref = Ca_element
FEATURE [App::DocumentObjectGroupPython] O_element022  label="O_element : 010"  # scripted group (container) (typed FeaturePython)
  n = 1
  ref = O_element
FEATURE [App::DocumentObjectGroupPython] G4_CALCIUM_OXIDE  # scripted group (container) (typed FeaturePython)
  Dunit = g/cm3
  Dvalue = 3.3
  Group = -> [Ca_element007,O_element022]
  conduct = 2
  density = 1
  expand = 3
  formula = G4_CALCIUM_OXIDE
  name = G4_CALCIUM_OXIDE
  specific = 4
FEATURE [App::DocumentObjectGroupPython] Ca_element008  label="Ca_element : 004"  # scripted group (container) (typed FeaturePython)
  n = 1
  ref = Ca_element
FEATURE [App::DocumentObjectGroupPython] S_element007  label="S_element : 002"  # scripted group (container) (typed FeaturePython)
  n = 1
  ref = S_element
FEATURE [App::DocumentObjectGroupPython] O_element023  label="O_element : 011"  # scripted group (container) (typed FeaturePython)
  n = 4
  ref = O_element
FEATURE [App::DocumentObjectGroupPython] G4_CALCIUM_SULFATE  # scripted group (container) (typed FeaturePython)
  Dunit = g/cm3
  Dvalue = 2.96
  Group = -> [Ca_element008,S_element007,O_element023]
  conduct = 2
  density = 1
  expand = 3
  formula = G4_CALCIUM_SULFATE
  name = G4_CALCIUM_SULFATE
  specific = 4
FEATURE [App::DocumentObjectGroupPython] Ca_element009  label="Ca_element : 005"  # scripted group (container) (typed FeaturePython)
  n = 1
  ref = Ca_element
FEATURE [App::DocumentObjectGroupPython] W_element002  label="W_element : 002"  # scripted group (container) (typed FeaturePython)
  n = 1
  ref = W_element
FEATURE [App::DocumentObjectGroupPython] O_element024  label="O_element : 012"  # scripted group (container) (typed FeaturePython)
  n = 4
  ref = O_element
FEATURE [App::DocumentObjectGroupPython] G4_CALCIUM_TUNGSTATE  # scripted group (container) (typed FeaturePython)
  Dunit = g/cm3
  Dvalue = 6.062
  Group = -> [Ca_element009,W_element002,O_element024]
  conduct = 2
  density = 1
  expand = 3
  formula = G4_CALCIUM_TUNGSTATE
  name = G4_CALCIUM_TUNGSTATE
  specific = 4
FEATURE [App::DocumentObjectGroupPython] C_element023  label="C_element : 010"  # scripted group (container) (typed FeaturePython)
  n = 1
  ref = C_element
FEATURE [App::DocumentObjectGroupPython] O_element025  label="O_element : 013"  # scripted group (container) (typed FeaturePython)
  n = 2
  ref = O_element
FEATURE [App::DocumentObjectGroupPython] G4_CARBON_DIOXIDE  # scripted group (container) (typed FeaturePython)
  Dunit = g/cm3
  Dvalue = 0.00184212
  Group = -> [C_element023,O_element025]
  conduct = 2
  density = 1
  expand = 3
  formula = G4_CARBON_DIOXIDE
  name = G4_CARBON_DIOXIDE
  specific = 4
FEATURE [App::DocumentObjectGroupPython] C_element024  label="C_element : 011"  # scripted group (container) (typed FeaturePython)
  n = 1
  ref = C_element
FEATURE [App::DocumentObjectGroupPython] Cl_element004  label="Cl_element : 4"  # scripted group (container) (typed FeaturePython)
  n = 4
  ref = Cl_element
FEATURE [App::DocumentObjectGroupPython] G4_CARBON_TETRACHLORIDE  # scripted group (container) (typed FeaturePython)
  Dunit = g/cm3
  Dvalue = 1.594
  Group = -> [C_element024,Cl_element004]
  conduct = 2
  density = 1
  expand = 3
  formula = G4_CARBON_TETRACHLORIDE
  name = G4_CARBON_TETRACHLORIDE
  specific = 4
FEATURE [App::DocumentObjectGroupPython] C_element025  label="C_element : 012"  # scripted group (container) (typed FeaturePython)
  n = 6
  ref = C_element
FEATURE [App::DocumentObjectGroupPython] H_element021  label="H_element : 012"  # scripted group (container) (typed FeaturePython)
  n = 10
  ref = H_element
FEATURE [App::DocumentObjectGroupPython] O_element026  label="O_element : 5"  # scripted group (container) (typed FeaturePython)
  n = 5
  ref = O_element
FEATURE [App::DocumentObjectGroupPython] G4_CELLULOSE_CELLOPHANE  # scripted group (container) (typed FeaturePython)
  Dunit = g/cm3
  Dvalue = 1.42
  Group = -> [C_element025,H_element021,O_element026]
  conduct = 2
  density = 1
  expand = 3
  formula = G4_CELLULOSE_CELLOPHANE
  name = G4_CELLULOSE_CELLOPHANE
  specific = 4
FEATURE [App::DocumentObjectGroupPython] H_element022  label="H_element : 0.067"  # scripted group (container) (typed FeaturePython)
  n = 0.067125
FEATURE [App::DocumentObjectGroupPython] C_element026  label="C_element : 0.545"  # scripted group (container) (typed FeaturePython)
  n = 0.545403
FEATURE [App::DocumentObjectGroupPython] O_element027  label="O_element : 0.387"  # scripted group (container) (typed FeaturePython)
  n = 0.387472
FEATURE [App::DocumentObjectGroupPython] G4_CELLULOSE_BUTYRATE  # scripted group (container) (typed FeaturePython)
  Dunit = g/cm3
  Dvalue = 1.2
  Group = -> [H_element022,C_element026,O_element027]
  conduct = 2
  density = 1
  expand = 3
  formula = G4_CELLULOSE_BUTYRATE
  name = G4_CELLULOSE_BUTYRATE
  specific = 4
FEATURE [App::DocumentObjectGroupPython] H_element023  label="H_element : 0.029"  # scripted group (container) (typed FeaturePython)
  n = 0.029216
FEATURE [App::DocumentObjectGroupPython] C_element027  label="C_element : 0.271"  # scripted group (container) (typed FeaturePython)
  n = 0.271296
FEATURE [App::DocumentObjectGroupPython] N_element013  label="N_element : 0.121"  # scripted group (container) (typed FeaturePython)
  n = 0.121276
FEATURE [App::DocumentObjectGroupPython] O_element028  label="O_element : 0.578"  # scripted group (container) (typed FeaturePython)
  n = 0.578212
FEATURE [App::DocumentObjectGroupPython] G4_CELLULOSE_NITRATE  # scripted group (container) (typed FeaturePython)
  Dunit = g/cm3
  Dvalue = 1.49
  Group = -> [H_element023,C_element027,N_element013,O_element028]
  conduct = 2
  density = 1
  expand = 3
  formula = G4_CELLULOSE_NITRATE
  name = G4_CELLULOSE_NITRATE
  specific = 4
FEATURE [App::DocumentObjectGroupPython] H_element024  label="H_element : 0.108"  # scripted group (container) (typed FeaturePython)
  n = 0.107596
FEATURE [App::DocumentObjectGroupPython] N_element014  label="N_element : 0.001"  # scripted group (container) (typed FeaturePython)
  n = 0.0008
FEATURE [App::DocumentObjectGroupPython] O_element029  label="O_element : 0.875"  # scripted group (container) (typed FeaturePython)
  n = 0.874976
FEATURE [App::DocumentObjectGroupPython] S_element008  label="S_element : 0.015"  # scripted group (container) (typed FeaturePython)
  n = 0.014627
FEATURE [App::DocumentObjectGroupPython] Ce_element001  label="Ce_element : 0.002"  # scripted group (container) (typed FeaturePython)
  n = 0.002001
FEATURE [App::DocumentObjectGroupPython] G4_CERIC_SULFATE  # scripted group (container) (typed FeaturePython)
  Dunit = g/cm3
  Dvalue = 1.03
  Group = -> [H_element024,N_element014,O_element029,S_element008,Ce_element001]
  conduct = 2
  density = 1
  expand = 3
  formula = G4_CERIC_SULFATE
  name = G4_CERIC_SULFATE
  specific = 4
FEATURE [App::DocumentObjectGroupPython] Cs_element001  label="Cs_element : 1"  # scripted group (container) (typed FeaturePython)
  n = 1
  ref = Cs_element
FEATURE [App::DocumentObjectGroupPython] F_element006  label="F_element : 1"  # scripted group (container) (typed FeaturePython)
  n = 1
  ref = F_element
FEATURE [App::DocumentObjectGroupPython] G4_CESIUM_FLUORIDE  # scripted group (container) (typed FeaturePython)
  Dunit = g/cm3
  Dvalue = 4.115
  Group = -> [Cs_element001,F_element006]
  conduct = 2
  density = 1
  expand = 3
  formula = G4_CESIUM_FLUORIDE
  name = G4_CESIUM_FLUORIDE
  specific = 4
FEATURE [App::DocumentObjectGroupPython] Cs_element002  label="Cs_element : 002"  # scripted group (container) (typed FeaturePython)
  n = 1
  ref = Cs_element
FEATURE [App::DocumentObjectGroupPython] I_element001  label="I_element : 1"  # scripted group (container) (typed FeaturePython)
  n = 1
  ref = I_element
FEATURE [App::DocumentObjectGroupPython] G4_CESIUM_IODIDE  # scripted group (container) (typed FeaturePython)
  Dunit = g/cm3
  Dvalue = 4.51
  Group = -> [Cs_element002,I_element001]
  conduct = 2
  density = 1
  expand = 3
  formula = G4_CESIUM_IODIDE
  name = G4_CESIUM_IODIDE
  specific = 4
FEATURE [App::DocumentObjectGroupPython] C_element028  label="C_element : 013"  # scripted group (container) (typed FeaturePython)
  n = 6
  ref = C_element
FEATURE [App::DocumentObjectGroupPython] H_element025  label="H_element : 013"  # scripted group (container) (typed FeaturePython)
  n = 5
  ref = H_element
FEATURE [App::DocumentObjectGroupPython] Cl_element005  label="Cl_element : 1"  # scripted group (container) (typed FeaturePython)
  n = 1
  ref = Cl_element
FEATURE [App::DocumentObjectGroupPython] G4_CHLOROBENZENE  # scripted group (container) (typed FeaturePython)
  Dunit = g/cm3
  Dvalue = 1.1058
  Group = -> [C_element028,H_element025,Cl_element005]
  conduct = 2
  density = 1
  expand = 3
  formula = G4_CHLOROBENZENE
  name = G4_CHLOROBENZENE
  specific = 4
FEATURE [App::DocumentObjectGroupPython] C_element029  label="C_element : 014"  # scripted group (container) (typed FeaturePython)
  n = 1
  ref = C_element
FEATURE [App::DocumentObjectGroupPython] H_element026  label="H_element : 1"  # scripted group (container) (typed FeaturePython)
  n = 1
  ref = H_element
FEATURE [App::DocumentObjectGroupPython] Cl_element006  label="Cl_element : 3"  # scripted group (container) (typed FeaturePython)
  n = 3
  ref = Cl_element
FEATURE [App::DocumentObjectGroupPython] G4_CHLOROFORM  # scripted group (container) (typed FeaturePython)
  Dunit = g/cm3
  Dvalue = 1.4832
  Group = -> [C_element029,H_element026,Cl_element006]
  conduct = 2
  density = 1
  expand = 3
  formula = G4_CHLOROFORM
  name = G4_CHLOROFORM
  specific = 4
FEATURE [App::DocumentObjectGroupPython] H_element027  label="H_element : 0.010"  # scripted group (container) (typed FeaturePython)
  n = 0.01
FEATURE [App::DocumentObjectGroupPython] C_element030  label="C_element : 0.001"  # scripted group (container) (typed FeaturePython)
  n = 0.001
FEATURE [App::DocumentObjectGroupPython] O_element030  label="O_element : 0.529"  # scripted group (container) (typed FeaturePython)
  n = 0.529107
FEATURE [App::DocumentObjectGroupPython] Na_element005  label="Na_element : 0.016"  # scripted group (container) (typed FeaturePython)
  n = 0.016
FEATURE [App::DocumentObjectGroupPython] Mg_element003  label="Mg_element : 0.004"  # scripted group (container) (typed FeaturePython)
  n = 0.002
FEATURE [App::DocumentObjectGroupPython] Al_element002  label="Al_element : 0.034"  # scripted group (container) (typed FeaturePython)
  n = 0.033872
FEATURE [App::DocumentObjectGroupPython] Si_element002  label="Si_element : 0.337"  # scripted group (container) (typed FeaturePython)
  n = 0.337021
FEATURE [App::DocumentObjectGroupPython] K_element003  label="K_element : 0.013"  # scripted group (container) (typed FeaturePython)
  n = 0.013
FEATURE [App::DocumentObjectGroupPython] Ca_element010  label="Ca_element : 0.044"  # scripted group (container) (typed FeaturePython)
  n = 0.044
FEATURE [App::DocumentObjectGroupPython] Fe_element002  label="Fe_element : 0.014"  # scripted group (container) (typed FeaturePython)
  n = 0.014
FEATURE [App::DocumentObjectGroupPython] G4_CONCRETE  # scripted group (container) (typed FeaturePython)
  Dunit = g/cm3
  Dvalue = 2.3
  Group = -> [H_element027,C_element030,O_element030,Na_element005,Mg_element003,Al_element002,Si_element002,K_element003,Ca_element010,Fe_element002]
  conduct = 2
  density = 1
  expand = 3
  formula = G4_CONCRETE
  name = G4_CONCRETE
  specific = 4
FEATURE [App::DocumentObjectGroupPython] C_element031  label="C_element : 015"  # scripted group (container) (typed FeaturePython)
  n = 6
  ref = C_element
FEATURE [App::DocumentObjectGroupPython] H_element028  label="H_element : 12"  # scripted group (container) (typed FeaturePython)
  n = 12
  ref = H_element
FEATURE [App::DocumentObjectGroupPython] G4_CYCLOHEXANE  # scripted group (container) (typed FeaturePython)
  Dunit = g/cm3
  Dvalue = 0.779
  Group = -> [C_element031,H_element028]
  conduct = 2
  density = 1
  expand = 3
  formula = G4_CYCLOHEXANE
  name = G4_CYCLOHEXANE
  specific = 4
FEATURE [App::DocumentObjectGroupPython] C_element032  label="C_element : 016"  # scripted group (container) (typed FeaturePython)
  n = 6
  ref = C_element
FEATURE [App::DocumentObjectGroupPython] H_element029  label="H_element : 4"  # scripted group (container) (typed FeaturePython)
  n = 4
  ref = H_element
FEATURE [App::DocumentObjectGroupPython] Cl_element007  label="Cl_element : 2"  # scripted group (container) (typed FeaturePython)
  n = 2
  ref = Cl_element
FEATURE [App::DocumentObjectGroupPython] G4_1_2_DICHLOROBENZENE  label="G4_1.2-DICHLOROBENZENE"  # scripted group (container) (typed FeaturePython)
  Dunit = g/cm3
  Dvalue = 1.3048
  Group = -> [C_element032,H_element029,Cl_element007]
  conduct = 2
  density = 1
  expand = 3
  formula = G4_1.2-DICHLOROBENZENE
  name = G4_1.2-DICHLOROBENZENE
  specific = 4
FEATURE [App::DocumentObjectGroupPython] C_element033  label="C_element : 017"  # scripted group (container) (typed FeaturePython)
  n = 4
  ref = C_element
FEATURE [App::DocumentObjectGroupPython] H_element030  label="H_element : 8"  # scripted group (container) (typed FeaturePython)
  n = 8
  ref = H_element
FEATURE [App::DocumentObjectGroupPython] O_element031  label="O_element : 014"  # scripted group (container) (typed FeaturePython)
  n = 1
  ref = O_element
FEATURE [App::DocumentObjectGroupPython] Cl_element008  label="Cl_element : 005"  # scripted group (container) (typed FeaturePython)
  n = 2
  ref = Cl_element
FEATURE [App::DocumentObjectGroupPython] G4_DICHLORODIETHYL_ETHER  # scripted group (container) (typed FeaturePython)
  Dunit = g/cm3
  Dvalue = 1.2199
  Group = -> [C_element033,H_element030,O_element031,Cl_element008]
  conduct = 2
  density = 1
  expand = 3
  formula = G4_DICHLORODIETHYL_ETHER
  name = G4_DICHLORODIETHYL_ETHER
  specific = 4
FEATURE [App::DocumentObjectGroupPython] C_element034  label="C_element : 018"  # scripted group (container) (typed FeaturePython)
  n = 2
  ref = C_element
FEATURE [App::DocumentObjectGroupPython] H_element031  label="H_element : 014"  # scripted group (container) (typed FeaturePython)
  n = 4
  ref = H_element
FEATURE [App::DocumentObjectGroupPython] Cl_element009  label="Cl_element : 006"  # scripted group (container) (typed FeaturePython)
  n = 2
  ref = Cl_element
FEATURE [App::DocumentObjectGroupPython] G4_1_2_DICHLOROETHANE  label="G4_1.2-DICHLOROETHANE"  # scripted group (container) (typed FeaturePython)
  Dunit = g/cm3
  Dvalue = 1.2351
  Group = -> [C_element034,H_element031,Cl_element009]
  conduct = 2
  density = 1
  expand = 3
  formula = G4_1.2-DICHLOROETHANE
  name = G4_1.2-DICHLOROETHANE
  specific = 4
FEATURE [App::DocumentObjectGroupPython] C_element035  label="C_element : 019"  # scripted group (container) (typed FeaturePython)
  n = 4
  ref = C_element
FEATURE [App::DocumentObjectGroupPython] H_element032  label="H_element : 015"  # scripted group (container) (typed FeaturePython)
  n = 10
  ref = H_element
FEATURE [App::DocumentObjectGroupPython] O_element032  label="O_element : 015"  # scripted group (container) (typed FeaturePython)
  n = 1
  ref = O_element
FEATURE [App::DocumentObjectGroupPython] G4_DIETHYL_ETHER  # scripted group (container) (typed FeaturePython)
  Dunit = g/cm3
  Dvalue = 0.71378
  Group = -> [C_element035,H_element032,O_element032]
  conduct = 2
  density = 1
  expand = 3
  formula = G4_DIETHYL_ETHER
  name = G4_DIETHYL_ETHER
  specific = 4
FEATURE [App::DocumentObjectGroupPython] C_element036  label="C_element : 020"  # scripted group (container) (typed FeaturePython)
  n = 3
  ref = C_element
FEATURE [App::DocumentObjectGroupPython] H_element033  label="H_element : 016"  # scripted group (container) (typed FeaturePython)
  n = 7
  ref = H_element
FEATURE [App::DocumentObjectGroupPython] N_element015  label="N_element : 008"  # scripted group (container) (typed FeaturePython)
  n = 1
  ref = N_element
FEATURE [App::DocumentObjectGroupPython] O_element033  label="O_element : 016"  # scripted group (container) (typed FeaturePython)
  n = 1
  ref = O_element
FEATURE [App::DocumentObjectGroupPython] G4_N_N_DIMETHYL_FORMAMIDE  label="G4_N.N-DIMETHYL_FORMAMIDE"  # scripted group (container) (typed FeaturePython)
  Dunit = g/cm3
  Dvalue = 0.9487
  Group = -> [C_element036,H_element033,N_element015,O_element033]
  conduct = 2
  density = 1
  expand = 3
  formula = G4_N.N-DIMETHYL_FORMAMIDE
  name = G4_N.N-DIMETHYL_FORMAMIDE
  specific = 4
FEATURE [App::DocumentObjectGroupPython] C_element037  label="C_element : 021"  # scripted group (container) (typed FeaturePython)
  n = 2
  ref = C_element
FEATURE [App::DocumentObjectGroupPython] H_element034  label="H_element : 017"  # scripted group (container) (typed FeaturePython)
  n = 6
  ref = H_element
FEATURE [App::DocumentObjectGroupPython] O_element034  label="O_element : 017"  # scripted group (container) (typed FeaturePython)
  n = 1
  ref = O_element
FEATURE [App::DocumentObjectGroupPython] S_element009  label="S_element : 003"  # scripted group (container) (typed FeaturePython)
  n = 1
  ref = S_element
FEATURE [App::DocumentObjectGroupPython] G4_DIMETHYL_SULFOXIDE  # scripted group (container) (typed FeaturePython)
  Dunit = g/cm3
  Dvalue = 1.1014
  Group = -> [C_element037,H_element034,O_element034,S_element009]
  conduct = 2
  density = 1
  expand = 3
  formula = G4_DIMETHYL_SULFOXIDE
  name = G4_DIMETHYL_SULFOXIDE
  specific = 4
FEATURE [App::DocumentObjectGroupPython] C_element038  label="C_element : 022"  # scripted group (container) (typed FeaturePython)
  n = 2
  ref = C_element
FEATURE [App::DocumentObjectGroupPython] H_element035  label="H_element : 018"  # scripted group (container) (typed FeaturePython)
  n = 6
  ref = H_element
FEATURE [App::DocumentObjectGroupPython] G4_ETHANE  # scripted group (container) (typed FeaturePython)
  Dunit = g/cm3
  Dvalue = 0.00125324
  Group = -> [C_element038,H_element035]
  conduct = 2
  density = 1
  expand = 3
  formula = G4_ETHANE
  name = G4_ETHANE
  specific = 4
FEATURE [App::DocumentObjectGroupPython] C_element039  label="C_element : 023"  # scripted group (container) (typed FeaturePython)
  n = 2
  ref = C_element
FEATURE [App::DocumentObjectGroupPython] H_element036  label="H_element : 019"  # scripted group (container) (typed FeaturePython)
  n = 6
  ref = H_element
FEATURE [App::DocumentObjectGroupPython] O_element035  label="O_element : 018"  # scripted group (container) (typed FeaturePython)
  n = 1
  ref = O_element
FEATURE [App::DocumentObjectGroupPython] G4_ETHYL_ALCOHOL  # scripted group (container) (typed FeaturePython)
  Dunit = g/cm3
  Dvalue = 0.7893
  Group = -> [C_element039,H_element036,O_element035]
  conduct = 2
  density = 1
  expand = 3
  formula = G4_ETHYL_ALCOHOL
  name = G4_ETHYL_ALCOHOL
  specific = 4
FEATURE [App::DocumentObjectGroupPython] H_element037  label="H_element : 0.090"  # scripted group (container) (typed FeaturePython)
  n = 0.090027
FEATURE [App::DocumentObjectGroupPython] C_element040  label="C_element : 0.585"  # scripted group (container) (typed FeaturePython)
  n = 0.585182
FEATURE [App::DocumentObjectGroupPython] O_element036  label="O_element : 0.325"  # scripted group (container) (typed FeaturePython)
  n = 0.324791
FEATURE [App::DocumentObjectGroupPython] G4_ETHYL_CELLULOSE  # scripted group (container) (typed FeaturePython)
  Dunit = g/cm3
  Dvalue = 1.13
  Group = -> [H_element037,C_element040,O_element036]
  conduct = 2
  density = 1
  expand = 3
  formula = G4_ETHYL_CELLULOSE
  name = G4_ETHYL_CELLULOSE
  specific = 4
FEATURE [App::DocumentObjectGroupPython] C_element041  label="C_element : 024"  # scripted group (container) (typed FeaturePython)
  n = 2
  ref = C_element
FEATURE [App::DocumentObjectGroupPython] H_element038  label="H_element : 020"  # scripted group (container) (typed FeaturePython)
  n = 4
  ref = H_element
FEATURE [App::DocumentObjectGroupPython] G4_ETHYLENE  # scripted group (container) (typed FeaturePython)
  Dunit = g/cm3
  Dvalue = 0.00117497
  Group = -> [C_element041,H_element038]
  conduct = 2
  density = 1
  expand = 3
  formula = G4_ETHYLENE
  name = G4_ETHYLENE
  specific = 4
FEATURE [App::DocumentObjectGroupPython] H_element039  label="H_element : 0.096"  # scripted group (container) (typed FeaturePython)
  n = 0.096
FEATURE [App::DocumentObjectGroupPython] C_element042  label="C_element : 0.195"  # scripted group (container) (typed FeaturePython)
  n = 0.195
FEATURE [App::DocumentObjectGroupPython] N_element016  label="N_element : 0.057"  # scripted group (container) (typed FeaturePython)
  n = 0.057
FEATURE [App::DocumentObjectGroupPython] O_element037  label="O_element : 0.646"  # scripted group (container) (typed FeaturePython)
  n = 0.646
FEATURE [App::DocumentObjectGroupPython] Na_element006  label="Na_element : 0.017"  # scripted group (container) (typed FeaturePython)
  n = 0.001
FEATURE [App::DocumentObjectGroupPython] P_element005  label="P_element : 0.104"  # scripted group (container) (typed FeaturePython)
  n = 0.001
FEATURE [App::DocumentObjectGroupPython] S_element010  label="S_element : 0.016"  # scripted group (container) (typed FeaturePython)
  n = 0.003
FEATURE [App::DocumentObjectGroupPython] Cl_element010  label="Cl_element : 0.005"  # scripted group (container) (typed FeaturePython)
  n = 0.001
FEATURE [App::DocumentObjectGroupPython] G4_EYE_LENS_ICRP  # scripted group (container) (typed FeaturePython)
  Dunit = g/cm3
  Dvalue = 1.07
  Group = -> [H_element039,C_element042,N_element016,O_element037,Na_element006,P_element005,S_element010,Cl_element010]
  conduct = 2
  density = 1
  expand = 3
  formula = G4_EYE_LENS_ICRP
  name = G4_EYE_LENS_ICRP
  specific = 4
FEATURE [App::DocumentObjectGroupPython] Fe_element003  label="Fe_element : 2"  # scripted group (container) (typed FeaturePython)
  n = 2
  ref = Fe_element
FEATURE [App::DocumentObjectGroupPython] O_element038  label="O_element : 019"  # scripted group (container) (typed FeaturePython)
  n = 3
  ref = O_element
FEATURE [App::DocumentObjectGroupPython] G4_FERRIC_OXIDE  # scripted group (container) (typed FeaturePython)
  Dunit = g/cm3
  Dvalue = 5.2
  Group = -> [Fe_element003,O_element038]
  conduct = 2
  density = 1
  expand = 3
  formula = G4_FERRIC_OXIDE
  name = G4_FERRIC_OXIDE
  specific = 4
FEATURE [App::DocumentObjectGroupPython] Fe_element004  label="Fe_element : 1"  # scripted group (container) (typed FeaturePython)
  n = 1
  ref = Fe_element
FEATURE [App::DocumentObjectGroupPython] B_element003  label="B_element : 1"  # scripted group (container) (typed FeaturePython)
  n = 1
  ref = B_element
FEATURE [App::DocumentObjectGroupPython] G4_FERROBORIDE  # scripted group (container) (typed FeaturePython)
  Dunit = g/cm3
  Dvalue = 7.15
  Group = -> [Fe_element004,B_element003]
  conduct = 2
  density = 1
  expand = 3
  formula = G4_FERROBORIDE
  name = G4_FERROBORIDE
  specific = 4
FEATURE [App::DocumentObjectGroupPython] Fe_element005  label="Fe_element : 003"  # scripted group (container) (typed FeaturePython)
  n = 1
  ref = Fe_element
FEATURE [App::DocumentObjectGroupPython] O_element039  label="O_element : 020"  # scripted group (container) (typed FeaturePython)
  n = 1
  ref = O_element
FEATURE [App::DocumentObjectGroupPython] G4_FERROUS_OXIDE  # scripted group (container) (typed FeaturePython)
  Dunit = g/cm3
  Dvalue = 5.7
  Group = -> [Fe_element005,O_element039]
  conduct = 2
  density = 1
  expand = 3
  formula = G4_FERROUS_OXIDE
  name = G4_FERROUS_OXIDE
  specific = 4
FEATURE [App::DocumentObjectGroupPython] H_element040  label="H_element : 0.115"  # scripted group (container) (typed FeaturePython)
  n = 0.108259
FEATURE [App::DocumentObjectGroupPython] N_element017  label="N_element : 0.000"  # scripted group (container) (typed FeaturePython)
  n = 2.7e-05
FEATURE [App::DocumentObjectGroupPython] O_element040  label="O_element : 0.879"  # scripted group (container) (typed FeaturePython)
  n = 0.878636
FEATURE [App::DocumentObjectGroupPython] Na_element007  label="Na_element : 0.000"  # scripted group (container) (typed FeaturePython)
  n = 2.2e-05
FEATURE [App::DocumentObjectGroupPython] S_element011  label="S_element : 0.013"  # scripted group (container) (typed FeaturePython)
  n = 0.012968
FEATURE [App::DocumentObjectGroupPython] Cl_element011  label="Cl_element : 0.000"  # scripted group (container) (typed FeaturePython)
  n = 3.4e-05
FEATURE [App::DocumentObjectGroupPython] Fe_element006  label="Fe_element : 0.000"  # scripted group (container) (typed FeaturePython)
  n = 5.4e-05
FEATURE [App::DocumentObjectGroupPython] G4_FERROUS_SULFATE  # scripted group (container) (typed FeaturePython)
  Dunit = g/cm3
  Dvalue = 1.024
  Group = -> [H_element040,N_element017,O_element040,Na_element007,S_element011,Cl_element011,Fe_element006]
  conduct = 2
  density = 1
  expand = 3
  formula = G4_FERROUS_SULFATE
  name = G4_FERROUS_SULFATE
  specific = 4
FEATURE [App::DocumentObjectGroupPython] C_element043  label="C_element : 0.099"  # scripted group (container) (typed FeaturePython)
  n = 0.099335
FEATURE [App::DocumentObjectGroupPython] F_element007  label="F_element : 0.314"  # scripted group (container) (typed FeaturePython)
  n = 0.314247
FEATURE [App::DocumentObjectGroupPython] Cl_element012  label="Cl_element : 0.586"  # scripted group (container) (typed FeaturePython)
  n = 0.586418
FEATURE [App::DocumentObjectGroupPython] G4_FREON_12  label="G4_FREON-12"  # scripted group (container) (typed FeaturePython)
  Dunit = g/cm3
  Dvalue = 1.12
  Group = -> [C_element043,F_element007,Cl_element012]
  conduct = 2
  density = 1
  expand = 3
  formula = G4_FREON-12
  name = G4_FREON-12
  specific = 4
FEATURE [App::DocumentObjectGroupPython] C_element044  label="C_element : 0.057"  # scripted group (container) (typed FeaturePython)
  n = 0.057245
FEATURE [App::DocumentObjectGroupPython] F_element008  label="F_element : 0.181"  # scripted group (container) (typed FeaturePython)
  n = 0.181096
FEATURE [App::DocumentObjectGroupPython] Br_element001  label="Br_element : 0.762"  # scripted group (container) (typed FeaturePython)
  n = 0.761659
FEATURE [App::DocumentObjectGroupPython] G4_FREON_12B2  label="G4_FREON-12B2"  # scripted group (container) (typed FeaturePython)
  Dunit = g/cm3
  Dvalue = 1.8
  Group = -> [C_element044,F_element008,Br_element001]
  conduct = 2
  density = 1
  expand = 3
  formula = G4_FREON-12B2
  name = G4_FREON-12B2
  specific = 4
FEATURE [App::DocumentObjectGroupPython] C_element045  label="C_element : 0.115"  # scripted group (container) (typed FeaturePython)
  n = 0.114983
FEATURE [App::DocumentObjectGroupPython] F_element009  label="F_element : 0.546"  # scripted group (container) (typed FeaturePython)
  n = 0.545621
FEATURE [App::DocumentObjectGroupPython] Cl_element013  label="Cl_element : 0.339"  # scripted group (container) (typed FeaturePython)
  n = 0.339396
FEATURE [App::DocumentObjectGroupPython] G4_FREON_13  label="G4_FREON-13"  # scripted group (container) (typed FeaturePython)
  Dunit = g/cm3
  Dvalue = 0.95
  Group = -> [C_element045,F_element009,Cl_element013]
  conduct = 2
  density = 1
  expand = 3
  formula = G4_FREON-13
  name = G4_FREON-13
  specific = 4
FEATURE [App::DocumentObjectGroupPython] C_element046  label="C_element : 025"  # scripted group (container) (typed FeaturePython)
  n = 1
  ref = C_element
FEATURE [App::DocumentObjectGroupPython] F_element010  label="F_element : 3"  # scripted group (container) (typed FeaturePython)
  n = 3
  ref = F_element
FEATURE [App::DocumentObjectGroupPython] Br_element002  label="Br_element : 1"  # scripted group (container) (typed FeaturePython)
  n = 1
  ref = Br_element
FEATURE [App::DocumentObjectGroupPython] G4_FREON_13B1  label="G4_FREON-13B1"  # scripted group (container) (typed FeaturePython)
  Dunit = g/cm3
  Dvalue = 1.5
  Group = -> [C_element046,F_element010,Br_element002]
  conduct = 2
  density = 1
  expand = 3
  formula = G4_FREON-13B1
  name = G4_FREON-13B1
  specific = 4
FEATURE [App::DocumentObjectGroupPython] C_element047  label="C_element : 0.061"  # scripted group (container) (typed FeaturePython)
  n = 0.061309
FEATURE [App::DocumentObjectGroupPython] F_element011  label="F_element : 0.291"  # scripted group (container) (typed FeaturePython)
  n = 0.290924
FEATURE [App::DocumentObjectGroupPython] I_element002  label="I_element : 0.648"  # scripted group (container) (typed FeaturePython)
  n = 0.647767
FEATURE [App::DocumentObjectGroupPython] G4_FREON_13I1  label="G4_FREON-13I1"  # scripted group (container) (typed FeaturePython)
  Dunit = g/cm3
  Dvalue = 1.8
  Group = -> [C_element047,F_element011,I_element002]
  conduct = 2
  density = 1
  expand = 3
  formula = G4_FREON-13I1
  name = G4_FREON-13I1
  specific = 4
FEATURE [App::DocumentObjectGroupPython] Gd_element001  label="Gd_element : 2"  # scripted group (container) (typed FeaturePython)
  n = 2
  ref = Gd_element
FEATURE [App::DocumentObjectGroupPython] O_element041  label="O_element : 021"  # scripted group (container) (typed FeaturePython)
  n = 2
  ref = O_element
FEATURE [App::DocumentObjectGroupPython] S_element012  label="S_element : 004"  # scripted group (container) (typed FeaturePython)
  n = 1
  ref = S_element
FEATURE [App::DocumentObjectGroupPython] G4_GADOLINIUM_OXYSULFIDE  # scripted group (container) (typed FeaturePython)
  Dunit = g/cm3
  Dvalue = 7.44
  Group = -> [Gd_element001,O_element041,S_element012]
  conduct = 2
  density = 1
  expand = 3
  formula = G4_GADOLINIUM_OXYSULFIDE
  name = G4_GADOLINIUM_OXYSULFIDE
  specific = 4
FEATURE [App::DocumentObjectGroupPython] Ga_element001  label="Ga_element : 1"  # scripted group (container) (typed FeaturePython)
  n = 1
  ref = Ga_element
FEATURE [App::DocumentObjectGroupPython] As_element001  label="As_element : 1"  # scripted group (container) (typed FeaturePython)
  n = 1
  ref = As_element
FEATURE [App::DocumentObjectGroupPython] G4_GALLIUM_ARSENIDE  # scripted group (container) (typed FeaturePython)
  Dunit = g/cm3
  Dvalue = 5.31
  Group = -> [Ga_element001,As_element001]
  conduct = 2
  density = 1
  expand = 3
  formula = G4_GALLIUM_ARSENIDE
  name = G4_GALLIUM_ARSENIDE
  specific = 4
FEATURE [App::DocumentObjectGroupPython] H_element041  label="H_element : 0.081"  # scripted group (container) (typed FeaturePython)
  n = 0.08118
FEATURE [App::DocumentObjectGroupPython] C_element048  label="C_element : 0.416"  # scripted group (container) (typed FeaturePython)
  n = 0.41606
FEATURE [App::DocumentObjectGroupPython] N_element018  label="N_element : 0.111"  # scripted group (container) (typed FeaturePython)
  n = 0.11124
FEATURE [App::DocumentObjectGroupPython] O_element042  label="O_element : 0.381"  # scripted group (container) (typed FeaturePython)
  n = 0.38064
FEATURE [App::DocumentObjectGroupPython] S_element013  label="S_element : 0.011"  # scripted group (container) (typed FeaturePython)
  n = 0.01088
FEATURE [App::DocumentObjectGroupPython] G4_GEL_PHOTO_EMULSION  # scripted group (container) (typed FeaturePython)
  Dunit = g/cm3
  Dvalue = 1.2914
  Group = -> [H_element041,C_element048,N_element018,O_element042,S_element013]
  conduct = 2
  density = 1
  expand = 3
  formula = G4_GEL_PHOTO_EMULSION
  name = G4_GEL_PHOTO_EMULSION
  specific = 4
FEATURE [App::DocumentObjectGroupPython] B_element004  label="B_element : 0.040"  # scripted group (container) (typed FeaturePython)
  n = 0.0400639
FEATURE [App::DocumentObjectGroupPython] O_element043  label="O_element : 0.540"  # scripted group (container) (typed FeaturePython)
  n = 0.539561
FEATURE [App::DocumentObjectGroupPython] Na_element008  label="Na_element : 0.028"  # scripted group (container) (typed FeaturePython)
  n = 0.0281909
FEATURE [App::DocumentObjectGroupPython] Al_element003  label="Al_element : 0.012"  # scripted group (container) (typed FeaturePython)
  n = 0.011644
FEATURE [App::DocumentObjectGroupPython] Si_element003  label="Si_element : 0.377"  # scripted group (container) (typed FeaturePython)
  n = 0.377219
FEATURE [App::DocumentObjectGroupPython] K_element004  label="K_element : 0.014"  # scripted group (container) (typed FeaturePython)
  n = 0.00332099
FEATURE [App::DocumentObjectGroupPython] G4_Pyrex_Glass  # scripted group (container) (typed FeaturePython)
  Dunit = g/cm3
  Dvalue = 2.23
  Group = -> [B_element004,O_element043,Na_element008,Al_element003,Si_element003,K_element004]
  conduct = 2
  density = 1
  expand = 3
  formula = G4_Pyrex_Glass
  name = G4_Pyrex_Glass
  specific = 4
FEATURE [App::DocumentObjectGroupPython] O_element044  label="O_element : 0.156"  # scripted group (container) (typed FeaturePython)
  n = 0.156453
FEATURE [App::DocumentObjectGroupPython] Si_element004  label="Si_element : 0.081"  # scripted group (container) (typed FeaturePython)
  n = 0.080866
FEATURE [App::DocumentObjectGroupPython] Ti_element001  label="Ti_element : 0.008"  # scripted group (container) (typed FeaturePython)
  n = 0.008092
FEATURE [App::DocumentObjectGroupPython] As_element002  label="As_element : 0.003"  # scripted group (container) (typed FeaturePython)
  n = 0.002651
FEATURE [App::DocumentObjectGroupPython] Pb_element001  label="Pb_element : 0.752"  # scripted group (container) (typed FeaturePython)
  n = 0.751938
FEATURE [App::DocumentObjectGroupPython] G4_GLASS_LEAD  # scripted group (container) (typed FeaturePython)
  Dunit = g/cm3
  Dvalue = 6.22
  Group = -> [O_element044,Si_element004,Ti_element001,As_element002,Pb_element001]
  conduct = 2
  density = 1
  expand = 3
  formula = G4_GLASS_LEAD
  name = G4_GLASS_LEAD
  specific = 4
FEATURE [App::DocumentObjectGroupPython] O_element045  label="O_element : 0.460"  # scripted group (container) (typed FeaturePython)
  n = 0.4598
FEATURE [App::DocumentObjectGroupPython] Na_element009  label="Na_element : 0.096"  # scripted group (container) (typed FeaturePython)
  n = 0.0964411
FEATURE [App::DocumentObjectGroupPython] Si_element005  label="Si_element : 0.378"  # scripted group (container) (typed FeaturePython)
  n = 0.336553
FEATURE [App::DocumentObjectGroupPython] Ca_element011  label="Ca_element : 0.107"  # scripted group (container) (typed FeaturePython)
  n = 0.107205
FEATURE [App::DocumentObjectGroupPython] G4_GLASS_PLATE  # scripted group (container) (typed FeaturePython)
  Dunit = g/cm3
  Dvalue = 2.4
  Group = -> [O_element045,Na_element009,Si_element005,Ca_element011]
  conduct = 2
  density = 1
  expand = 3
  formula = G4_GLASS_PLATE
  name = G4_GLASS_PLATE
  specific = 4
FEATURE [App::DocumentObjectGroupPython] C_element049  label="C_element : 026"  # scripted group (container) (typed FeaturePython)
  n = 5
  ref = C_element
FEATURE [App::DocumentObjectGroupPython] H_element042  label="H_element : 021"  # scripted group (container) (typed FeaturePython)
  n = 10
  ref = H_element
FEATURE [App::DocumentObjectGroupPython] N_element019  label="N_element : 2"  # scripted group (container) (typed FeaturePython)
  n = 2
  ref = N_element
FEATURE [App::DocumentObjectGroupPython] O_element046  label="O_element : 022"  # scripted group (container) (typed FeaturePython)
  n = 3
  ref = O_element
FEATURE [App::DocumentObjectGroupPython] G4_GLUTAMINE  # scripted group (container) (typed FeaturePython)
  Dunit = g/cm3
  Dvalue = 1.46
  Group = -> [C_element049,H_element042,N_element019,O_element046]
  conduct = 2
  density = 1
  expand = 3
  formula = G4_GLUTAMINE
  name = G4_GLUTAMINE
  specific = 4
FEATURE [App::DocumentObjectGroupPython] C_element050  label="C_element : 027"  # scripted group (container) (typed FeaturePython)
  n = 3
  ref = C_element
FEATURE [App::DocumentObjectGroupPython] H_element043  label="H_element : 022"  # scripted group (container) (typed FeaturePython)
  n = 8
  ref = H_element
FEATURE [App::DocumentObjectGroupPython] O_element047  label="O_element : 023"  # scripted group (container) (typed FeaturePython)
  n = 3
  ref = O_element
FEATURE [App::DocumentObjectGroupPython] G4_GLYCEROL  # scripted group (container) (typed FeaturePython)
  Dunit = g/cm3
  Dvalue = 1.2613
  Group = -> [C_element050,H_element043,O_element047]
  conduct = 2
  density = 1
  expand = 3
  formula = G4_GLYCEROL
  name = G4_GLYCEROL
  specific = 4
FEATURE [App::DocumentObjectGroupPython] C_element051  label="C_element : 028"  # scripted group (container) (typed FeaturePython)
  n = 5
  ref = C_element
FEATURE [App::DocumentObjectGroupPython] H_element044  label="H_element : 023"  # scripted group (container) (typed FeaturePython)
  n = 5
  ref = H_element
FEATURE [App::DocumentObjectGroupPython] N_element020  label="N_element : 009"  # scripted group (container) (typed FeaturePython)
  n = 5
  ref = N_element
FEATURE [App::DocumentObjectGroupPython] O_element048  label="O_element : 024"  # scripted group (container) (typed FeaturePython)
  n = 1
  ref = O_element
FEATURE [App::DocumentObjectGroupPython] G4_GUANINE  # scripted group (container) (typed FeaturePython)
  Dunit = g/cm3
  Dvalue = 2.2
  Group = -> [C_element051,H_element044,N_element020,O_element048]
  conduct = 2
  density = 1
  expand = 3
  formula = G4_GUANINE
  name = G4_GUANINE
  specific = 4
FEATURE [App::DocumentObjectGroupPython] Ca_element012  label="Ca_element : 006"  # scripted group (container) (typed FeaturePython)
  n = 1
  ref = Ca_element
FEATURE [App::DocumentObjectGroupPython] S_element014  label="S_element : 005"  # scripted group (container) (typed FeaturePython)
  n = 1
  ref = S_element
FEATURE [App::DocumentObjectGroupPython] O_element049  label="O_element : 6"  # scripted group (container) (typed FeaturePython)
  n = 6
  ref = O_element
FEATURE [App::DocumentObjectGroupPython] H_element045  label="H_element : 024"  # scripted group (container) (typed FeaturePython)
  n = 4
  ref = H_element
FEATURE [App::DocumentObjectGroupPython] G4_GYPSUM  # scripted group (container) (typed FeaturePython)
  Dunit = g/cm3
  Dvalue = 2.32
  Group = -> [Ca_element012,S_element014,O_element049,H_element045]
  conduct = 2
  density = 1
  expand = 3
  formula = G4_GYPSUM
  name = G4_GYPSUM
  specific = 4
FEATURE [App::DocumentObjectGroupPython] C_element052  label="C_element : 7"  # scripted group (container) (typed FeaturePython)
  n = 7
  ref = C_element
FEATURE [App::DocumentObjectGroupPython] H_element046  label="H_element : 16"  # scripted group (container) (typed FeaturePython)
  n = 16
  ref = H_element
FEATURE [App::DocumentObjectGroupPython] G4_N_HEPTANE  label="G4_N-HEPTANE"  # scripted group (container) (typed FeaturePython)
  Dunit = g/cm3
  Dvalue = 0.68376
  Group = -> [C_element052,H_element046]
  conduct = 2
  density = 1
  expand = 3
  formula = G4_N-HEPTANE
  name = G4_N-HEPTANE
  specific = 4
FEATURE [App::DocumentObjectGroupPython] C_element053  label="C_element : 029"  # scripted group (container) (typed FeaturePython)
  n = 6
  ref = C_element
FEATURE [App::DocumentObjectGroupPython] H_element047  label="H_element : 14"  # scripted group (container) (typed FeaturePython)
  n = 14
  ref = H_element
FEATURE [App::DocumentObjectGroupPython] G4_N_HEXANE  label="G4_N-HEXANE"  # scripted group (container) (typed FeaturePython)
  Dunit = g/cm3
  Dvalue = 0.6603
  Group = -> [C_element053,H_element047]
  conduct = 2
  density = 1
  expand = 3
  formula = G4_N-HEXANE
  name = G4_N-HEXANE
  specific = 4
FEATURE [App::DocumentObjectGroupPython] C_element054  label="C_element : 22"  # scripted group (container) (typed FeaturePython)
  n = 22
  ref = C_element
FEATURE [App::DocumentObjectGroupPython] H_element048  label="H_element : 025"  # scripted group (container) (typed FeaturePython)
  n = 10
  ref = H_element
FEATURE [App::DocumentObjectGroupPython] N_element021  label="N_element : 010"  # scripted group (container) (typed FeaturePython)
  n = 2
  ref = N_element
FEATURE [App::DocumentObjectGroupPython] O_element050  label="O_element : 025"  # scripted group (container) (typed FeaturePython)
  n = 5
  ref = O_element
FEATURE [App::DocumentObjectGroupPython] G4_KAPTON  # scripted group (container) (typed FeaturePython)
  Dunit = g/cm3
  Dvalue = 1.42
  Group = -> [C_element054,H_element048,N_element021,O_element050]
  conduct = 2
  density = 1
  expand = 3
  formula = G4_KAPTON
  name = G4_KAPTON
  specific = 4
FEATURE [App::DocumentObjectGroupPython] La_element001  label="La_element : 1"  # scripted group (container) (typed FeaturePython)
  n = 1
  ref = La_element
FEATURE [App::DocumentObjectGroupPython] Br_element003  label="Br_element : 002"  # scripted group (container) (typed FeaturePython)
  n = 1
  ref = Br_element
FEATURE [App::DocumentObjectGroupPython] O_element051  label="O_element : 026"  # scripted group (container) (typed FeaturePython)
  n = 1
  ref = O_element
FEATURE [App::DocumentObjectGroupPython] G4_LANTHANUM_OXYBROMIDE  # scripted group (container) (typed FeaturePython)
  Dunit = g/cm3
  Dvalue = 6.28
  Group = -> [La_element001,Br_element003,O_element051]
  conduct = 2
  density = 1
  expand = 3
  formula = G4_LANTHANUM_OXYBROMIDE
  name = G4_LANTHANUM_OXYBROMIDE
  specific = 4
FEATURE [App::DocumentObjectGroupPython] La_element002  label="La_element : 2"  # scripted group (container) (typed FeaturePython)
  n = 2
  ref = La_element
FEATURE [App::DocumentObjectGroupPython] O_element052  label="O_element : 027"  # scripted group (container) (typed FeaturePython)
  n = 2
  ref = O_element
FEATURE [App::DocumentObjectGroupPython] S_element015  label="S_element : 006"  # scripted group (container) (typed FeaturePython)
  n = 1
  ref = S_element
FEATURE [App::DocumentObjectGroupPython] G4_LANTHANUM_OXYSULFIDE  # scripted group (container) (typed FeaturePython)
  Dunit = g/cm3
  Dvalue = 5.86
  Group = -> [La_element002,O_element052,S_element015]
  conduct = 2
  density = 1
  expand = 3
  formula = G4_LANTHANUM_OXYSULFIDE
  name = G4_LANTHANUM_OXYSULFIDE
  specific = 4
FEATURE [App::DocumentObjectGroupPython] O_element053  label="O_element : 0.072"  # scripted group (container) (typed FeaturePython)
  n = 0.071682
FEATURE [App::DocumentObjectGroupPython] Pb_element002  label="Pb_element : 0.928"  # scripted group (container) (typed FeaturePython)
  n = 0.928318
FEATURE [App::DocumentObjectGroupPython] G4_LEAD_OXIDE  # scripted group (container) (typed FeaturePython)
  Dunit = g/cm3
  Dvalue = 9.53
  Group = -> [O_element053,Pb_element002]
  conduct = 2
  density = 1
  expand = 3
  formula = G4_LEAD_OXIDE
  name = G4_LEAD_OXIDE
  specific = 4
FEATURE [App::DocumentObjectGroupPython] Li_element001  label="Li_element : 1"  # scripted group (container) (typed FeaturePython)
  n = 1
  ref = Li_element
FEATURE [App::DocumentObjectGroupPython] N_element022  label="N_element : 011"  # scripted group (container) (typed FeaturePython)
  n = 1
  ref = N_element
FEATURE [App::DocumentObjectGroupPython] H_element049  label="H_element : 026"  # scripted group (container) (typed FeaturePython)
  n = 2
  ref = H_element
FEATURE [App::DocumentObjectGroupPython] G4_LITHIUM_AMIDE  # scripted group (container) (typed FeaturePython)
  Dunit = g/cm3
  Dvalue = 1.178
  Group = -> [Li_element001,N_element022,H_element049]
  conduct = 2
  density = 1
  expand = 3
  formula = G4_LITHIUM_AMIDE
  name = G4_LITHIUM_AMIDE
  specific = 4
FEATURE [App::DocumentObjectGroupPython] Li_element002  label="Li_element : 2"  # scripted group (container) (typed FeaturePython)
  n = 2
  ref = Li_element
FEATURE [App::DocumentObjectGroupPython] C_element055  label="C_element : 030"  # scripted group (container) (typed FeaturePython)
  n = 1
  ref = C_element
FEATURE [App::DocumentObjectGroupPython] O_element054  label="O_element : 028"  # scripted group (container) (typed FeaturePython)
  n = 3
  ref = O_element
FEATURE [App::DocumentObjectGroupPython] G4_LITHIUM_CARBONATE  # scripted group (container) (typed FeaturePython)
  Dunit = g/cm3
  Dvalue = 2.11
  Group = -> [Li_element002,C_element055,O_element054]
  conduct = 2
  density = 1
  expand = 3
  formula = G4_LITHIUM_CARBONATE
  name = G4_LITHIUM_CARBONATE
  specific = 4
FEATURE [App::DocumentObjectGroupPython] Li_element003  label="Li_element : 003"  # scripted group (container) (typed FeaturePython)
  n = 1
  ref = Li_element
FEATURE [App::DocumentObjectGroupPython] F_element012  label="F_element : 004"  # scripted group (container) (typed FeaturePython)
  n = 1
  ref = F_element
FEATURE [App::DocumentObjectGroupPython] G4_LITHIUM_FLUORIDE  # scripted group (container) (typed FeaturePython)
  Dunit = g/cm3
  Dvalue = 2.635
  Group = -> [Li_element003,F_element012]
  conduct = 2
  density = 1
  expand = 3
  formula = G4_LITHIUM_FLUORIDE
  name = G4_LITHIUM_FLUORIDE
  specific = 4
FEATURE [App::DocumentObjectGroupPython] Li_element004  label="Li_element : 004"  # scripted group (container) (typed FeaturePython)
  n = 1
  ref = Li_element
FEATURE [App::DocumentObjectGroupPython] H_element050  label="H_element : 027"  # scripted group (container) (typed FeaturePython)
  n = 1
  ref = H_element
FEATURE [App::DocumentObjectGroupPython] G4_LITHIUM_HYDRIDE  # scripted group (container) (typed FeaturePython)
  Dunit = g/cm3
  Dvalue = 0.82
  Group = -> [Li_element004,H_element050]
  conduct = 2
  density = 1
  expand = 3
  formula = G4_LITHIUM_HYDRIDE
  name = G4_LITHIUM_HYDRIDE
  specific = 4
FEATURE [App::DocumentObjectGroupPython] Li_element005  label="Li_element : 005"  # scripted group (container) (typed FeaturePython)
  n = 1
  ref = Li_element
FEATURE [App::DocumentObjectGroupPython] I_element003  label="I_element : 002"  # scripted group (container) (typed FeaturePython)
  n = 1
  ref = I_element
FEATURE [App::DocumentObjectGroupPython] G4_LITHIUM_IODIDE  # scripted group (container) (typed FeaturePython)
  Dunit = g/cm3
  Dvalue = 3.494
  Group = -> [Li_element005,I_element003]
  conduct = 2
  density = 1
  expand = 3
  formula = G4_LITHIUM_IODIDE
  name = G4_LITHIUM_IODIDE
  specific = 4
FEATURE [App::DocumentObjectGroupPython] Li_element006  label="Li_element : 006"  # scripted group (container) (typed FeaturePython)
  n = 2
  ref = Li_element
FEATURE [App::DocumentObjectGroupPython] O_element055  label="O_element : 029"  # scripted group (container) (typed FeaturePython)
  n = 1
  ref = O_element
FEATURE [App::DocumentObjectGroupPython] G4_LITHIUM_OXIDE  # scripted group (container) (typed FeaturePython)
  Dunit = g/cm3
  Dvalue = 2.013
  Group = -> [Li_element006,O_element055]
  conduct = 2
  density = 1
  expand = 3
  formula = G4_LITHIUM_OXIDE
  name = G4_LITHIUM_OXIDE
  specific = 4
FEATURE [App::DocumentObjectGroupPython] Li_element007  label="Li_element : 007"  # scripted group (container) (typed FeaturePython)
  n = 2
  ref = Li_element
FEATURE [App::DocumentObjectGroupPython] B_element005  label="B_element : 005"  # scripted group (container) (typed FeaturePython)
  n = 4
  ref = B_element
FEATURE [App::DocumentObjectGroupPython] O_element056  label="O_element : 7"  # scripted group (container) (typed FeaturePython)
  n = 7
  ref = O_element
FEATURE [App::DocumentObjectGroupPython] G4_LITHIUM_TETRABORATE  # scripted group (container) (typed FeaturePython)
  Dunit = g/cm3
  Dvalue = 2.44
  Group = -> [Li_element007,B_element005,O_element056]
  conduct = 2
  density = 1
  expand = 3
  formula = G4_LITHIUM_TETRABORATE
  name = G4_LITHIUM_TETRABORATE
  specific = 4
FEATURE [App::DocumentObjectGroupPython] H_element051  label="H_element : 0.105"  # scripted group (container) (typed FeaturePython)
  n = 0.105
FEATURE [App::DocumentObjectGroupPython] C_element056  label="C_element : 0.083"  # scripted group (container) (typed FeaturePython)
  n = 0.083
FEATURE [App::DocumentObjectGroupPython] N_element023  label="N_element : 0.023"  # scripted group (container) (typed FeaturePython)
  n = 0.023
FEATURE [App::DocumentObjectGroupPython] O_element057  label="O_element : 0.779"  # scripted group (container) (typed FeaturePython)
  n = 0.779
FEATURE [App::DocumentObjectGroupPython] Na_element010  label="Na_element : 0.097"  # scripted group (container) (typed FeaturePython)
  n = 0.002
FEATURE [App::DocumentObjectGroupPython] P_element006  label="P_element : 0.105"  # scripted group (container) (typed FeaturePython)
  n = 0.001
FEATURE [App::DocumentObjectGroupPython] S_element016  label="S_element : 0.017"  # scripted group (container) (typed FeaturePython)
  n = 0.002
FEATURE [App::DocumentObjectGroupPython] Cl_element014  label="Cl_element : 0.587"  # scripted group (container) (typed FeaturePython)
  n = 0.003
FEATURE [App::DocumentObjectGroupPython] K_element005  label="K_element : 0.015"  # scripted group (container) (typed FeaturePython)
  n = 0.002
FEATURE [App::DocumentObjectGroupPython] G4_LUNG_ICRP  # scripted group (container) (typed FeaturePython)
  Dunit = g/cm3
  Dvalue = 1.04
  Group = -> [H_element051,C_element056,N_element023,O_element057,Na_element010,P_element006,S_element016,Cl_element014,K_element005]
  conduct = 2
  density = 1
  expand = 3
  formula = G4_LUNG_ICRP
  name = G4_LUNG_ICRP
  specific = 4
FEATURE [App::DocumentObjectGroupPython] H_element052  label="H_element : 0.116"  # scripted group (container) (typed FeaturePython)
  n = 0.114318
FEATURE [App::DocumentObjectGroupPython] C_element057  label="C_element : 0.656"  # scripted group (container) (typed FeaturePython)
  n = 0.655824
FEATURE [App::DocumentObjectGroupPython] O_element058  label="O_element : 0.092"  # scripted group (container) (typed FeaturePython)
  n = 0.0921831
FEATURE [App::DocumentObjectGroupPython] Mg_element004  label="Mg_element : 0.135"  # scripted group (container) (typed FeaturePython)
  n = 0.134792
FEATURE [App::DocumentObjectGroupPython] Ca_element013  label="Ca_element : 0.003"  # scripted group (container) (typed FeaturePython)
  n = 0.002883
FEATURE [App::DocumentObjectGroupPython] G4_M3_WAX  # scripted group (container) (typed FeaturePython)
  Dunit = g/cm3
  Dvalue = 1.05
  Group = -> [H_element052,C_element057,O_element058,Mg_element004,Ca_element013]
  conduct = 2
  density = 1
  expand = 3
  formula = G4_M3_WAX
  name = G4_M3_WAX
  specific = 4
FEATURE [App::DocumentObjectGroupPython] Mg_element005  label="Mg_element : 1"  # scripted group (container) (typed FeaturePython)
  n = 1
  ref = Mg_element
FEATURE [App::DocumentObjectGroupPython] C_element058  label="C_element : 031"  # scripted group (container) (typed FeaturePython)
  n = 1
  ref = C_element
FEATURE [App::DocumentObjectGroupPython] O_element059  label="O_element : 030"  # scripted group (container) (typed FeaturePython)
  n = 3
  ref = O_element
FEATURE [App::DocumentObjectGroupPython] G4_MAGNESIUM_CARBONATE  # scripted group (container) (typed FeaturePython)
  Dunit = g/cm3
  Dvalue = 2.958
  Group = -> [Mg_element005,C_element058,O_element059]
  conduct = 2
  density = 1
  expand = 3
  formula = G4_MAGNESIUM_CARBONATE
  name = G4_MAGNESIUM_CARBONATE
  specific = 4
FEATURE [App::DocumentObjectGroupPython] Mg_element006  label="Mg_element : 002"  # scripted group (container) (typed FeaturePython)
  n = 1
  ref = Mg_element
FEATURE [App::DocumentObjectGroupPython] F_element013  label="F_element : 005"  # scripted group (container) (typed FeaturePython)
  n = 2
  ref = F_element
FEATURE [App::DocumentObjectGroupPython] G4_MAGNESIUM_FLUORIDE  # scripted group (container) (typed FeaturePython)
  Dunit = g/cm3
  Dvalue = 3
  Group = -> [Mg_element006,F_element013]
  conduct = 2
  density = 1
  expand = 3
  formula = G4_MAGNESIUM_FLUORIDE
  name = G4_MAGNESIUM_FLUORIDE
  specific = 4
FEATURE [App::DocumentObjectGroupPython] Mg_element007  label="Mg_element : 003"  # scripted group (container) (typed FeaturePython)
  n = 1
  ref = Mg_element
FEATURE [App::DocumentObjectGroupPython] O_element060  label="O_element : 031"  # scripted group (container) (typed FeaturePython)
  n = 1
  ref = O_element
FEATURE [App::DocumentObjectGroupPython] G4_MAGNESIUM_OXIDE  # scripted group (container) (typed FeaturePython)
  Dunit = g/cm3
  Dvalue = 3.58
  Group = -> [Mg_element007,O_element060]
  conduct = 2
  density = 1
  expand = 3
  formula = G4_MAGNESIUM_OXIDE
  name = G4_MAGNESIUM_OXIDE
  specific = 4
FEATURE [App::DocumentObjectGroupPython] Mg_element008  label="Mg_element : 004"  # scripted group (container) (typed FeaturePython)
  n = 1
  ref = Mg_element
FEATURE [App::DocumentObjectGroupPython] B_element006  label="B_element : 006"  # scripted group (container) (typed FeaturePython)
  n = 4
  ref = B_element
FEATURE [App::DocumentObjectGroupPython] O_element061  label="O_element : 032"  # scripted group (container) (typed FeaturePython)
  n = 7
  ref = O_element
FEATURE [App::DocumentObjectGroupPython] G4_MAGNESIUM_TETRABORATE  # scripted group (container) (typed FeaturePython)
  Dunit = g/cm3
  Dvalue = 2.53
  Group = -> [Mg_element008,B_element006,O_element061]
  conduct = 2
  density = 1
  expand = 3
  formula = G4_MAGNESIUM_TETRABORATE
  name = G4_MAGNESIUM_TETRABORATE
  specific = 4
FEATURE [App::DocumentObjectGroupPython] Hg_element001  label="Hg_element : 1"  # scripted group (container) (typed FeaturePython)
  n = 1
  ref = Hg_element
FEATURE [App::DocumentObjectGroupPython] I_element004  label="I_element : 2"  # scripted group (container) (typed FeaturePython)
  n = 2
  ref = I_element
FEATURE [App::DocumentObjectGroupPython] G4_MERCURIC_IODIDE  # scripted group (container) (typed FeaturePython)
  Dunit = g/cm3
  Dvalue = 6.36
  Group = -> [Hg_element001,I_element004]
  conduct = 2
  density = 1
  expand = 3
  formula = G4_MERCURIC_IODIDE
  name = G4_MERCURIC_IODIDE
  specific = 4
FEATURE [App::DocumentObjectGroupPython] C_element059  label="C_element : 032"  # scripted group (container) (typed FeaturePython)
  n = 1
  ref = C_element
FEATURE [App::DocumentObjectGroupPython] H_element053  label="H_element : 028"  # scripted group (container) (typed FeaturePython)
  n = 4
  ref = H_element
FEATURE [App::DocumentObjectGroupPython] G4_METHANE  # scripted group (container) (typed FeaturePython)
  Dunit = g/cm3
  Dvalue = 0.000667151
  Group = -> [C_element059,H_element053]
  conduct = 2
  density = 1
  expand = 3
  formula = G4_METHANE
  name = G4_METHANE
  specific = 4
FEATURE [App::DocumentObjectGroupPython] C_element060  label="C_element : 033"  # scripted group (container) (typed FeaturePython)
  n = 1
  ref = C_element
FEATURE [App::DocumentObjectGroupPython] H_element054  label="H_element : 029"  # scripted group (container) (typed FeaturePython)
  n = 4
  ref = H_element
FEATURE [App::DocumentObjectGroupPython] O_element062  label="O_element : 033"  # scripted group (container) (typed FeaturePython)
  n = 1
  ref = O_element
FEATURE [App::DocumentObjectGroupPython] G4_METHANOL  # scripted group (container) (typed FeaturePython)
  Dunit = g/cm3
  Dvalue = 0.7914
  Group = -> [C_element060,H_element054,O_element062]
  conduct = 2
  density = 1
  expand = 3
  formula = G4_METHANOL
  name = G4_METHANOL
  specific = 4
FEATURE [App::DocumentObjectGroupPython] H_element055  label="H_element : 0.134"  # scripted group (container) (typed FeaturePython)
  n = 0.13404
FEATURE [App::DocumentObjectGroupPython] C_element061  label="C_element : 0.778"  # scripted group (container) (typed FeaturePython)
  n = 0.77796
FEATURE [App::DocumentObjectGroupPython] O_element063  label="O_element : 0.035"  # scripted group (container) (typed FeaturePython)
  n = 0.03502
FEATURE [App::DocumentObjectGroupPython] Mg_element009  label="Mg_element : 0.039"  # scripted group (container) (typed FeaturePython)
  n = 0.038594
FEATURE [App::DocumentObjectGroupPython] Ti_element002  label="Ti_element : 0.014"  # scripted group (container) (typed FeaturePython)
  n = 0.014386
FEATURE [App::DocumentObjectGroupPython] G4_MIX_D_WAX  # scripted group (container) (typed FeaturePython)
  Dunit = g/cm3
  Dvalue = 0.99
  Group = -> [H_element055,C_element061,O_element063,Mg_element009,Ti_element002]
  conduct = 2
  density = 1
  expand = 3
  formula = G4_MIX_D_WAX
  name = G4_MIX_D_WAX
  specific = 4
FEATURE [App::DocumentObjectGroupPython] H_element056  label="H_element : 0.135"  # scripted group (container) (typed FeaturePython)
  n = 0.081192
FEATURE [App::DocumentObjectGroupPython] C_element062  label="C_element : 0.583"  # scripted group (container) (typed FeaturePython)
  n = 0.583442
FEATURE [App::DocumentObjectGroupPython] N_element024  label="N_element : 0.018"  # scripted group (container) (typed FeaturePython)
  n = 0.017798
FEATURE [App::DocumentObjectGroupPython] O_element064  label="O_element : 0.186"  # scripted group (container) (typed FeaturePython)
  n = 0.186381
FEATURE [App::DocumentObjectGroupPython] Mg_element010  label="Mg_element : 0.130"  # scripted group (container) (typed FeaturePython)
  n = 0.130287
FEATURE [App::DocumentObjectGroupPython] Cl_element015  label="Cl_element : 0.588"  # scripted group (container) (typed FeaturePython)
  n = 0.0009
FEATURE [App::DocumentObjectGroupPython] G4_MS20_TISSUE  # scripted group (container) (typed FeaturePython)
  Dunit = g/cm3
  Dvalue = 1
  Group = -> [H_element056,C_element062,N_element024,O_element064,Mg_element010,Cl_element015]
  conduct = 2
  density = 1
  expand = 3
  formula = G4_MS20_TISSUE
  name = G4_MS20_TISSUE
  specific = 4
FEATURE [App::DocumentObjectGroupPython] H_element057  label="H_element : 0.136"  # scripted group (container) (typed FeaturePython)
  n = 0.102
FEATURE [App::DocumentObjectGroupPython] C_element063  label="C_element : 0.143"  # scripted group (container) (typed FeaturePython)
  n = 0.143
FEATURE [App::DocumentObjectGroupPython] N_element025  label="N_element : 0.034"  # scripted group (container) (typed FeaturePython)
  n = 0.034
FEATURE [App::DocumentObjectGroupPython] O_element065  label="O_element : 0.710"  # scripted group (container) (typed FeaturePython)
  n = 0.71
FEATURE [App::DocumentObjectGroupPython] Na_element011  label="Na_element : 0.098"  # scripted group (container) (typed FeaturePython)
  n = 0.001
FEATURE [App::DocumentObjectGroupPython] P_element007  label="P_element : 0.002"  # scripted group (container) (typed FeaturePython)
  n = 0.002
FEATURE [App::DocumentObjectGroupPython] S_element017  label="S_element : 0.018"  # scripted group (container) (typed FeaturePython)
  n = 0.003
FEATURE [App::DocumentObjectGroupPython] Cl_element016  label="Cl_element : 0.589"  # scripted group (container) (typed FeaturePython)
  n = 0.001
FEATURE [App::DocumentObjectGroupPython] K_element006  label="K_element : 0.004"  # scripted group (container) (typed FeaturePython)
  n = 0.004
FEATURE [App::DocumentObjectGroupPython] G4_MUSCLE_SKELETAL_ICRP  # scripted group (container) (typed FeaturePython)
  Dunit = g/cm3
  Dvalue = 1.05
  Group = -> [H_element057,C_element063,N_element025,O_element065,Na_element011,P_element007,S_element017,Cl_element016,K_element006]
  conduct = 2
  density = 1
  expand = 3
  formula = G4_MUSCLE_SKELETAL_ICRP
  name = G4_MUSCLE_SKELETAL_ICRP
  specific = 4
FEATURE [App::DocumentObjectGroupPython] H_element058  label="H_element : 0.137"  # scripted group (container) (typed FeaturePython)
  n = 0.102102
FEATURE [App::DocumentObjectGroupPython] C_element064  label="C_element : 0.123"  # scripted group (container) (typed FeaturePython)
  n = 0.123123
FEATURE [App::DocumentObjectGroupPython] N_element026  label="N_element : 0.756"  # scripted group (container) (typed FeaturePython)
  n = 0.035035
FEATURE [App::DocumentObjectGroupPython] O_element066  label="O_element : 0.730"  # scripted group (container) (typed FeaturePython)
  n = 0.72973
FEATURE [App::DocumentObjectGroupPython] Na_element012  label="Na_element : 0.099"  # scripted group (container) (typed FeaturePython)
  n = 0.001001
FEATURE [App::DocumentObjectGroupPython] P_element008  label="P_element : 0.106"  # scripted group (container) (typed FeaturePython)
  n = 0.002002
FEATURE [App::DocumentObjectGroupPython] S_element018  label="S_element : 0.019"  # scripted group (container) (typed FeaturePython)
  n = 0.004004
FEATURE [App::DocumentObjectGroupPython] K_element007  label="K_element : 0.016"  # scripted group (container) (typed FeaturePython)
  n = 0.003003
FEATURE [App::DocumentObjectGroupPython] G4_MUSCLE_STRIATED_ICRU  # scripted group (container) (typed FeaturePython)
  Dunit = g/cm3
  Dvalue = 1.04
  Group = -> [H_element058,C_element064,N_element026,O_element066,Na_element012,P_element008,S_element018,K_element007]
  conduct = 2
  density = 1
  expand = 3
  formula = G4_MUSCLE_STRIATED_ICRU
  name = G4_MUSCLE_STRIATED_ICRU
  specific = 4
FEATURE [App::DocumentObjectGroupPython] H_element059  label="H_element : 0.098"  # scripted group (container) (typed FeaturePython)
  n = 0.0982341
FEATURE [App::DocumentObjectGroupPython] C_element065  label="C_element : 0.156"  # scripted group (container) (typed FeaturePython)
  n = 0.156214
FEATURE [App::DocumentObjectGroupPython] N_element027  label="N_element : 0.757"  # scripted group (container) (typed FeaturePython)
  n = 0.035451
FEATURE [App::DocumentObjectGroupPython] O_element067  label="O_element : 0.880"  # scripted group (container) (typed FeaturePython)
  n = 0.710101
FEATURE [App::DocumentObjectGroupPython] G4_MUSCLE_WITH_SUCROSE  # scripted group (container) (typed FeaturePython)
  Dunit = g/cm3
  Dvalue = 1.11
  Group = -> [H_element059,C_element065,N_element027,O_element067]
  conduct = 2
  density = 1
  expand = 3
  formula = G4_MUSCLE_WITH_SUCROSE
  name = G4_MUSCLE_WITH_SUCROSE
  specific = 4
FEATURE [App::DocumentObjectGroupPython] H_element060  label="H_element : 0.138"  # scripted group (container) (typed FeaturePython)
  n = 0.101969
FEATURE [App::DocumentObjectGroupPython] C_element066  label="C_element : 0.120"  # scripted group (container) (typed FeaturePython)
  n = 0.120058
FEATURE [App::DocumentObjectGroupPython] N_element028  label="N_element : 0.758"  # scripted group (container) (typed FeaturePython)
  n = 0.035451
FEATURE [App::DocumentObjectGroupPython] O_element068  label="O_element : 0.743"  # scripted group (container) (typed FeaturePython)
  n = 0.742522
FEATURE [App::DocumentObjectGroupPython] G4_MUSCLE_WITHOUT_SUCROSE  # scripted group (container) (typed FeaturePython)
  Dunit = g/cm3
  Dvalue = 1.07
  Group = -> [H_element060,C_element066,N_element028,O_element068]
  conduct = 2
  density = 1
  expand = 3
  formula = G4_MUSCLE_WITHOUT_SUCROSE
  name = G4_MUSCLE_WITHOUT_SUCROSE
  specific = 4
FEATURE [App::DocumentObjectGroupPython] C_element067  label="C_element : 10"  # scripted group (container) (typed FeaturePython)
  n = 10
  ref = C_element
FEATURE [App::DocumentObjectGroupPython] H_element061  label="H_element : 030"  # scripted group (container) (typed FeaturePython)
  n = 8
  ref = H_element
FEATURE [App::DocumentObjectGroupPython] G4_NAPHTHALENE  # scripted group (container) (typed FeaturePython)
  Dunit = g/cm3
  Dvalue = 1.145
  Group = -> [C_element067,H_element061]
  conduct = 2
  density = 1
  expand = 3
  formula = G4_NAPHTHALENE
  name = G4_NAPHTHALENE
  specific = 4
FEATURE [App::DocumentObjectGroupPython] C_element068  label="C_element : 034"  # scripted group (container) (typed FeaturePython)
  n = 6
  ref = C_element
FEATURE [App::DocumentObjectGroupPython] H_element062  label="H_element : 031"  # scripted group (container) (typed FeaturePython)
  n = 5
  ref = H_element
FEATURE [App::DocumentObjectGroupPython] N_element029  label="N_element : 012"  # scripted group (container) (typed FeaturePython)
  n = 1
  ref = N_element
FEATURE [App::DocumentObjectGroupPython] O_element069  label="O_element : 034"  # scripted group (container) (typed FeaturePython)
  n = 2
  ref = O_element
FEATURE [App::DocumentObjectGroupPython] G4_NITROBENZENE  # scripted group (container) (typed FeaturePython)
  Dunit = g/cm3
  Dvalue = 1.19867
  Group = -> [C_element068,H_element062,N_element029,O_element069]
  conduct = 2
  density = 1
  expand = 3
  formula = G4_NITROBENZENE
  name = G4_NITROBENZENE
  specific = 4
FEATURE [App::DocumentObjectGroupPython] N_element030  label="N_element : 013"  # scripted group (container) (typed FeaturePython)
  n = 2
  ref = N_element
FEATURE [App::DocumentObjectGroupPython] O_element070  label="O_element : 035"  # scripted group (container) (typed FeaturePython)
  n = 1
  ref = O_element
FEATURE [App::DocumentObjectGroupPython] G4_NITROUS_OXIDE  # scripted group (container) (typed FeaturePython)
  Dunit = g/cm3
  Dvalue = 0.00183094
  Group = -> [N_element030,O_element070]
  conduct = 2
  density = 1
  expand = 3
  formula = G4_NITROUS_OXIDE
  name = G4_NITROUS_OXIDE
  specific = 4
FEATURE [App::DocumentObjectGroupPython] H_element063  label="H_element : 0.104"  # scripted group (container) (typed FeaturePython)
  n = 0.103509
FEATURE [App::DocumentObjectGroupPython] C_element069  label="C_element : 0.648"  # scripted group (container) (typed FeaturePython)
  n = 0.648416
FEATURE [App::DocumentObjectGroupPython] N_element031  label="N_element : 0.100"  # scripted group (container) (typed FeaturePython)
  n = 0.0995361
FEATURE [App::DocumentObjectGroupPython] O_element071  label="O_element : 0.149"  # scripted group (container) (typed FeaturePython)
  n = 0.148539
FEATURE [App::DocumentObjectGroupPython] G4_NYLON_8062  label="G4_NYLON-8062"  # scripted group (container) (typed FeaturePython)
  Dunit = g/cm3
  Dvalue = 1.08
  Group = -> [H_element063,C_element069,N_element031,O_element071]
  conduct = 2
  density = 1
  expand = 3
  formula = G4_NYLON-8062
  name = G4_NYLON-8062
  specific = 4
FEATURE [App::DocumentObjectGroupPython] C_element070  label="C_element : 035"  # scripted group (container) (typed FeaturePython)
  n = 6
  ref = C_element
FEATURE [App::DocumentObjectGroupPython] H_element064  label="H_element : 11"  # scripted group (container) (typed FeaturePython)
  n = 11
  ref = H_element
FEATURE [App::DocumentObjectGroupPython] N_element032  label="N_element : 014"  # scripted group (container) (typed FeaturePython)
  n = 1
  ref = N_element
FEATURE [App::DocumentObjectGroupPython] O_element072  label="O_element : 036"  # scripted group (container) (typed FeaturePython)
  n = 1
  ref = O_element
FEATURE [App::DocumentObjectGroupPython] G4_NYLON_6_6  label="G4_NYLON-6-6"  # scripted group (container) (typed FeaturePython)
  Dunit = g/cm3
  Dvalue = 1.14
  Group = -> [C_element070,H_element064,N_element032,O_element072]
  conduct = 2
  density = 1
  expand = 3
  formula = G4_NYLON-6-6
  name = G4_NYLON-6-6
  specific = 4
FEATURE [App::DocumentObjectGroupPython] H_element065  label="H_element : 0.139"  # scripted group (container) (typed FeaturePython)
  n = 0.107062
FEATURE [App::DocumentObjectGroupPython] C_element071  label="C_element : 0.680"  # scripted group (container) (typed FeaturePython)
  n = 0.680449
FEATURE [App::DocumentObjectGroupPython] N_element033  label="N_element : 0.099"  # scripted group (container) (typed FeaturePython)
  n = 0.099189
FEATURE [App::DocumentObjectGroupPython] O_element073  label="O_element : 0.113"  # scripted group (container) (typed FeaturePython)
  n = 0.1133
FEATURE [App::DocumentObjectGroupPython] G4_NYLON_6_10  label="G4_NYLON-6-10"  # scripted group (container) (typed FeaturePython)
  Dunit = g/cm3
  Dvalue = 1.14
  Group = -> [H_element065,C_element071,N_element033,O_element073]
  conduct = 2
  density = 1
  expand = 3
  formula = G4_NYLON-6-10
  name = G4_NYLON-6-10
  specific = 4
FEATURE [App::DocumentObjectGroupPython] H_element066  label="H_element : 0.140"  # scripted group (container) (typed FeaturePython)
  n = 0.115476
FEATURE [App::DocumentObjectGroupPython] C_element072  label="C_element : 0.721"  # scripted group (container) (typed FeaturePython)
  n = 0.720818
FEATURE [App::DocumentObjectGroupPython] N_element034  label="N_element : 0.076"  # scripted group (container) (typed FeaturePython)
  n = 0.0764169
FEATURE [App::DocumentObjectGroupPython] O_element074  label="O_element : 0.087"  # scripted group (container) (typed FeaturePython)
  n = 0.0872889
FEATURE [App::DocumentObjectGroupPython] G4_NYLON_11_RILSAN  label="G4_NYLON-11_RILSAN"  # scripted group (container) (typed FeaturePython)
  Dunit = g/cm3
  Dvalue = 1.425
  Group = -> [H_element066,C_element072,N_element034,O_element074]
  conduct = 2
  density = 1
  expand = 3
  formula = G4_NYLON-11_RILSAN
  name = G4_NYLON-11_RILSAN
  specific = 4
FEATURE [App::DocumentObjectGroupPython] C_element073  label="C_element : 8"  # scripted group (container) (typed FeaturePython)
  n = 8
  ref = C_element
FEATURE [App::DocumentObjectGroupPython] H_element067  label="H_element : 18"  # scripted group (container) (typed FeaturePython)
  n = 18
  ref = H_element
FEATURE [App::DocumentObjectGroupPython] G4_OCTANE  # scripted group (container) (typed FeaturePython)
  Dunit = g/cm3
  Dvalue = 0.7026
  Group = -> [C_element073,H_element067]
  conduct = 2
  density = 1
  expand = 3
  formula = G4_OCTANE
  name = G4_OCTANE
  specific = 4
FEATURE [App::DocumentObjectGroupPython] C_element074  label="C_element : 25"  # scripted group (container) (typed FeaturePython)
  n = 25
  ref = C_element
FEATURE [App::DocumentObjectGroupPython] H_element068  label="H_element : 52"  # scripted group (container) (typed FeaturePython)
  n = 52
  ref = H_element
FEATURE [App::DocumentObjectGroupPython] G4_PARAFFIN  # scripted group (container) (typed FeaturePython)
  Dunit = g/cm3
  Dvalue = 0.93
  Group = -> [C_element074,H_element068]
  conduct = 2
  density = 1
  expand = 3
  formula = G4_PARAFFIN
  name = G4_PARAFFIN
  specific = 4
FEATURE [App::DocumentObjectGroupPython] C_element075  label="C_element : 036"  # scripted group (container) (typed FeaturePython)
  n = 5
  ref = C_element
FEATURE [App::DocumentObjectGroupPython] H_element069  label="H_element : 032"  # scripted group (container) (typed FeaturePython)
  n = 12
  ref = H_element
FEATURE [App::DocumentObjectGroupPython] G4_N_PENTANE  label="G4_N-PENTANE"  # scripted group (container) (typed FeaturePython)
  Dunit = g/cm3
  Dvalue = 0.6262
  Group = -> [C_element075,H_element069]
  conduct = 2
  density = 1
  expand = 3
  formula = G4_N-PENTANE
  name = G4_N-PENTANE
  specific = 4
FEATURE [App::DocumentObjectGroupPython] H_element070  label="H_element : 0.014"  # scripted group (container) (typed FeaturePython)
  n = 0.0141
FEATURE [App::DocumentObjectGroupPython] C_element076  label="C_element : 0.072"  # scripted group (container) (typed FeaturePython)
  n = 0.072261
FEATURE [App::DocumentObjectGroupPython] N_element035  label="N_element : 0.019"  # scripted group (container) (typed FeaturePython)
  n = 0.01932
FEATURE [App::DocumentObjectGroupPython] O_element075  label="O_element : 0.066"  # scripted group (container) (typed FeaturePython)
  n = 0.066101
FEATURE [App::DocumentObjectGroupPython] S_element019  label="S_element : 0.020"  # scripted group (container) (typed FeaturePython)
  n = 0.00189
FEATURE [App::DocumentObjectGroupPython] Br_element004  label="Br_element : 0.349"  # scripted group (container) (typed FeaturePython)
  n = 0.349103
FEATURE [App::DocumentObjectGroupPython] Ag_element001  label="Ag_element : 0.474"  # scripted group (container) (typed FeaturePython)
  n = 0.474105
FEATURE [App::DocumentObjectGroupPython] I_element005  label="I_element : 0.003"  # scripted group (container) (typed FeaturePython)
  n = 0.00312
FEATURE [App::DocumentObjectGroupPython] G4_PHOTO_EMULSION  # scripted group (container) (typed FeaturePython)
  Dunit = g/cm3
  Dvalue = 3.815
  Group = -> [H_element070,C_element076,N_element035,O_element075,S_element019,Br_element004,Ag_element001,I_element005]
  conduct = 2
  density = 1
  expand = 3
  formula = G4_PHOTO_EMULSION
  name = G4_PHOTO_EMULSION
  specific = 4
FEATURE [App::DocumentObjectGroupPython] C_element077  label="C_element : 9"  # scripted group (container) (typed FeaturePython)
  n = 9
  ref = C_element
FEATURE [App::DocumentObjectGroupPython] H_element071  label="H_element : 033"  # scripted group (container) (typed FeaturePython)
  n = 10
  ref = H_element
FEATURE [App::DocumentObjectGroupPython] G4_PLASTIC_SC_VINYLTOLUENE  # scripted group (container) (typed FeaturePython)
  Dunit = g/cm3
  Dvalue = 1.032
  Group = -> [C_element077,H_element071]
  conduct = 2
  density = 1
  expand = 3
  formula = G4_PLASTIC_SC_VINYLTOLUENE
  name = G4_PLASTIC_SC_VINYLTOLUENE
  specific = 4
FEATURE [App::DocumentObjectGroupPython] Pu_element001  label="Pu_element : 1"  # scripted group (container) (typed FeaturePython)
  n = 1
  ref = Pu_element
FEATURE [App::DocumentObjectGroupPython] O_element076  label="O_element : 037"  # scripted group (container) (typed FeaturePython)
  n = 2
  ref = O_element
FEATURE [App::DocumentObjectGroupPython] G4_PLUTONIUM_DIOXIDE  # scripted group (container) (typed FeaturePython)
  Dunit = g/cm3
  Dvalue = 11.46
  Group = -> [Pu_element001,O_element076]
  conduct = 2
  density = 1
  expand = 3
  formula = G4_PLUTONIUM_DIOXIDE
  name = G4_PLUTONIUM_DIOXIDE
  specific = 4
FEATURE [App::DocumentObjectGroupPython] C_element078  label="C_element : 037"  # scripted group (container) (typed FeaturePython)
  n = 3
  ref = C_element
FEATURE [App::DocumentObjectGroupPython] H_element072  label="H_element : 034"  # scripted group (container) (typed FeaturePython)
  n = 3
  ref = H_element
FEATURE [App::DocumentObjectGroupPython] N_element036  label="N_element : 015"  # scripted group (container) (typed FeaturePython)
  n = 1
  ref = N_element
FEATURE [App::DocumentObjectGroupPython] G4_POLYACRYLONITRILE  # scripted group (container) (typed FeaturePython)
  Dunit = g/cm3
  Dvalue = 1.17
  Group = -> [C_element078,H_element072,N_element036]
  conduct = 2
  density = 1
  expand = 3
  formula = G4_POLYACRYLONITRILE
  name = G4_POLYACRYLONITRILE
  specific = 4
FEATURE [App::DocumentObjectGroupPython] C_element079  label="C_element : 16"  # scripted group (container) (typed FeaturePython)
  n = 16
  ref = C_element
FEATURE [App::DocumentObjectGroupPython] H_element073  label="H_element : 035"  # scripted group (container) (typed FeaturePython)
  n = 14
  ref = H_element
FEATURE [App::DocumentObjectGroupPython] O_element077  label="O_element : 038"  # scripted group (container) (typed FeaturePython)
  n = 3
  ref = O_element
FEATURE [App::DocumentObjectGroupPython] G4_POLYCARBONATE  # scripted group (container) (typed FeaturePython)
  Dunit = g/cm3
  Dvalue = 1.2
  Group = -> [C_element079,H_element073,O_element077]
  conduct = 2
  density = 1
  expand = 3
  formula = G4_POLYCARBONATE
  name = G4_POLYCARBONATE
  specific = 4
FEATURE [App::DocumentObjectGroupPython] C_element080  label="C_element : 038"  # scripted group (container) (typed FeaturePython)
  n = 8
  ref = C_element
FEATURE [App::DocumentObjectGroupPython] H_element074  label="H_element : 036"  # scripted group (container) (typed FeaturePython)
  n = 7
  ref = H_element
FEATURE [App::DocumentObjectGroupPython] Cl_element017  label="Cl_element : 007"  # scripted group (container) (typed FeaturePython)
  n = 1
  ref = Cl_element
FEATURE [App::DocumentObjectGroupPython] G4_POLYCHLOROSTYRENE  # scripted group (container) (typed FeaturePython)
  Dunit = g/cm3
  Dvalue = 1.3
  Group = -> [C_element080,H_element074,Cl_element017]
  conduct = 2
  density = 1
  expand = 3
  formula = G4_POLYCHLOROSTYRENE
  name = G4_POLYCHLOROSTYRENE
  specific = 4
FEATURE [App::DocumentObjectGroupPython] C_element081  label="C_element : 039"  # scripted group (container) (typed FeaturePython)
  n = 1
  ref = C_element
FEATURE [App::DocumentObjectGroupPython] H_element075  label="H_element : 037"  # scripted group (container) (typed FeaturePython)
  n = 2
  ref = H_element
FEATURE [App::DocumentObjectGroupPython] G4_POLYETHYLENE  # scripted group (container) (typed FeaturePython)
  Dunit = g/cm3
  Dvalue = 0.94
  Group = -> [C_element081,H_element075]
  conduct = 2
  density = 1
  expand = 3
  formula = G4_POLYETHYLENE
  name = G4_POLYETHYLENE
  specific = 4
FEATURE [App::DocumentObjectGroupPython] C_element082  label="C_element : 040"  # scripted group (container) (typed FeaturePython)
  n = 10
  ref = C_element
FEATURE [App::DocumentObjectGroupPython] H_element076  label="H_element : 038"  # scripted group (container) (typed FeaturePython)
  n = 8
  ref = H_element
FEATURE [App::DocumentObjectGroupPython] O_element078  label="O_element : 039"  # scripted group (container) (typed FeaturePython)
  n = 4
  ref = O_element
FEATURE [App::DocumentObjectGroupPython] G4_MYLAR  # scripted group (container) (typed FeaturePython)
  Dunit = g/cm3
  Dvalue = 1.4
  Group = -> [C_element082,H_element076,O_element078]
  conduct = 2
  density = 1
  expand = 3
  formula = G4_MYLAR
  name = G4_MYLAR
  specific = 4
FEATURE [App::DocumentObjectGroupPython] C_element083  label="C_element : 041"  # scripted group (container) (typed FeaturePython)
  n = 5
  ref = C_element
FEATURE [App::DocumentObjectGroupPython] H_element077  label="H_element : 039"  # scripted group (container) (typed FeaturePython)
  n = 8
  ref = H_element
FEATURE [App::DocumentObjectGroupPython] O_element079  label="O_element : 040"  # scripted group (container) (typed FeaturePython)
  n = 2
  ref = O_element
FEATURE [App::DocumentObjectGroupPython] G4_PLEXIGLASS  # scripted group (container) (typed FeaturePython)
  Dunit = g/cm3
  Dvalue = 1.19
  Group = -> [C_element083,H_element077,O_element079]
  conduct = 2
  density = 1
  expand = 3
  formula = G4_PLEXIGLASS
  name = G4_PLEXIGLASS
  specific = 4
FEATURE [App::DocumentObjectGroupPython] C_element084  label="C_element : 042"  # scripted group (container) (typed FeaturePython)
  n = 1
  ref = C_element
FEATURE [App::DocumentObjectGroupPython] H_element078  label="H_element : 040"  # scripted group (container) (typed FeaturePython)
  n = 2
  ref = H_element
FEATURE [App::DocumentObjectGroupPython] O_element080  label="O_element : 041"  # scripted group (container) (typed FeaturePython)
  n = 1
  ref = O_element
FEATURE [App::DocumentObjectGroupPython] G4_POLYOXYMETHYLENE  # scripted group (container) (typed FeaturePython)
  Dunit = g/cm3
  Dvalue = 1.425
  Group = -> [C_element084,H_element078,O_element080]
  conduct = 2
  density = 1
  expand = 3
  formula = G4_POLYOXYMETHYLENE
  name = G4_POLYOXYMETHYLENE
  specific = 4
FEATURE [App::DocumentObjectGroupPython] C_element085  label="C_element : 043"  # scripted group (container) (typed FeaturePython)
  n = 2
  ref = C_element
FEATURE [App::DocumentObjectGroupPython] H_element079  label="H_element : 041"  # scripted group (container) (typed FeaturePython)
  n = 4
  ref = H_element
FEATURE [App::DocumentObjectGroupPython] G4_POLYPROPYLENE  # scripted group (container) (typed FeaturePython)
  Dunit = g/cm3
  Dvalue = 0.9
  Group = -> [C_element085,H_element079]
  conduct = 2
  density = 1
  expand = 3
  formula = G4_POLYPROPYLENE
  name = G4_POLYPROPYLENE
  specific = 4
FEATURE [App::DocumentObjectGroupPython] C_element086  label="C_element : 044"  # scripted group (container) (typed FeaturePython)
  n = 8
  ref = C_element
FEATURE [App::DocumentObjectGroupPython] H_element080  label="H_element : 042"  # scripted group (container) (typed FeaturePython)
  n = 8
  ref = H_element
FEATURE [App::DocumentObjectGroupPython] G4_POLYSTYRENE  # scripted group (container) (typed FeaturePython)
  Dunit = g/cm3
  Dvalue = 1.06
  Group = -> [C_element086,H_element080]
  conduct = 2
  density = 1
  expand = 3
  formula = G4_POLYSTYRENE
  name = G4_POLYSTYRENE
  specific = 4
FEATURE [App::DocumentObjectGroupPython] C_element087  label="C_element : 045"  # scripted group (container) (typed FeaturePython)
  n = 2
  ref = C_element
FEATURE [App::DocumentObjectGroupPython] F_element014  label="F_element : 4"  # scripted group (container) (typed FeaturePython)
  n = 4
  ref = F_element
FEATURE [App::DocumentObjectGroupPython] G4_TEFLON  # scripted group (container) (typed FeaturePython)
  Dunit = g/cm3
  Dvalue = 2.2
  Group = -> [C_element087,F_element014]
  conduct = 2
  density = 1
  expand = 3
  formula = G4_TEFLON
  name = G4_TEFLON
  specific = 4
FEATURE [App::DocumentObjectGroupPython] C_element088  label="C_element : 046"  # scripted group (container) (typed FeaturePython)
  n = 2
  ref = C_element
FEATURE [App::DocumentObjectGroupPython] F_element015  label="F_element : 006"  # scripted group (container) (typed FeaturePython)
  n = 3
  ref = F_element
FEATURE [App::DocumentObjectGroupPython] Cl_element018  label="Cl_element : 008"  # scripted group (container) (typed FeaturePython)
  n = 1
  ref = Cl_element
FEATURE [App::DocumentObjectGroupPython] G4_POLYTRIFLUOROCHLOROETHYLENE  # scripted group (container) (typed FeaturePython)
  Dunit = g/cm3
  Dvalue = 2.1
  Group = -> [C_element088,F_element015,Cl_element018]
  conduct = 2
  density = 1
  expand = 3
  formula = G4_POLYTRIFLUOROCHLOROETHYLENE
  name = G4_POLYTRIFLUOROCHLOROETHYLENE
  specific = 4
FEATURE [App::DocumentObjectGroupPython] C_element089  label="C_element : 047"  # scripted group (container) (typed FeaturePython)
  n = 4
  ref = C_element
FEATURE [App::DocumentObjectGroupPython] H_element081  label="H_element : 043"  # scripted group (container) (typed FeaturePython)
  n = 6
  ref = H_element
FEATURE [App::DocumentObjectGroupPython] O_element081  label="O_element : 042"  # scripted group (container) (typed FeaturePython)
  n = 2
  ref = O_element
FEATURE [App::DocumentObjectGroupPython] G4_POLYVINYL_ACETATE  # scripted group (container) (typed FeaturePython)
  Dunit = g/cm3
  Dvalue = 1.19
  Group = -> [C_element089,H_element081,O_element081]
  conduct = 2
  density = 1
  expand = 3
  formula = G4_POLYVINYL_ACETATE
  name = G4_POLYVINYL_ACETATE
  specific = 4
FEATURE [App::DocumentObjectGroupPython] C_element090  label="C_element : 048"  # scripted group (container) (typed FeaturePython)
  n = 2
  ref = C_element
FEATURE [App::DocumentObjectGroupPython] H_element082  label="H_element : 044"  # scripted group (container) (typed FeaturePython)
  n = 4
  ref = H_element
FEATURE [App::DocumentObjectGroupPython] O_element082  label="O_element : 043"  # scripted group (container) (typed FeaturePython)
  n = 1
  ref = O_element
FEATURE [App::DocumentObjectGroupPython] G4_POLYVINYL_ALCOHOL  # scripted group (container) (typed FeaturePython)
  Dunit = g/cm3
  Dvalue = 1.3
  Group = -> [C_element090,H_element082,O_element082]
  conduct = 2
  density = 1
  expand = 3
  formula = G4_POLYVINYL_ALCOHOL
  name = G4_POLYVINYL_ALCOHOL
  specific = 4
FEATURE [App::DocumentObjectGroupPython] C_element091  label="C_element : 049"  # scripted group (container) (typed FeaturePython)
  n = 8
  ref = C_element
FEATURE [App::DocumentObjectGroupPython] H_element083  label="H_element : 045"  # scripted group (container) (typed FeaturePython)
  n = 14
  ref = H_element
FEATURE [App::DocumentObjectGroupPython] O_element083  label="O_element : 044"  # scripted group (container) (typed FeaturePython)
  n = 2
  ref = O_element
FEATURE [App::DocumentObjectGroupPython] G4_POLYVINYL_BUTYRAL  # scripted group (container) (typed FeaturePython)
  Dunit = g/cm3
  Dvalue = 1.12
  Group = -> [C_element091,H_element083,O_element083]
  conduct = 2
  density = 1
  expand = 3
  formula = G4_POLYVINYL_BUTYRAL
  name = G4_POLYVINYL_BUTYRAL
  specific = 4
FEATURE [App::DocumentObjectGroupPython] C_element092  label="C_element : 050"  # scripted group (container) (typed FeaturePython)
  n = 2
  ref = C_element
FEATURE [App::DocumentObjectGroupPython] H_element084  label="H_element : 046"  # scripted group (container) (typed FeaturePython)
  n = 3
  ref = H_element
FEATURE [App::DocumentObjectGroupPython] Cl_element019  label="Cl_element : 009"  # scripted group (container) (typed FeaturePython)
  n = 1
  ref = Cl_element
FEATURE [App::DocumentObjectGroupPython] G4_POLYVINYL_CHLORIDE  # scripted group (container) (typed FeaturePython)
  Dunit = g/cm3
  Dvalue = 1.3
  Group = -> [C_element092,H_element084,Cl_element019]
  conduct = 2
  density = 1
  expand = 3
  formula = G4_POLYVINYL_CHLORIDE
  name = G4_POLYVINYL_CHLORIDE
  specific = 4
FEATURE [App::DocumentObjectGroupPython] C_element093  label="C_element : 051"  # scripted group (container) (typed FeaturePython)
  n = 2
  ref = C_element
FEATURE [App::DocumentObjectGroupPython] H_element085  label="H_element : 047"  # scripted group (container) (typed FeaturePython)
  n = 2
  ref = H_element
FEATURE [App::DocumentObjectGroupPython] Cl_element020  label="Cl_element : 010"  # scripted group (container) (typed FeaturePython)
  n = 2
  ref = Cl_element
FEATURE [App::DocumentObjectGroupPython] G4_POLYVINYLIDENE_CHLORIDE  # scripted group (container) (typed FeaturePython)
  Dunit = g/cm3
  Dvalue = 1.7
  Group = -> [C_element093,H_element085,Cl_element020]
  conduct = 2
  density = 1
  expand = 3
  formula = G4_POLYVINYLIDENE_CHLORIDE
  name = G4_POLYVINYLIDENE_CHLORIDE
  specific = 4
FEATURE [App::DocumentObjectGroupPython] C_element094  label="C_element : 052"  # scripted group (container) (typed FeaturePython)
  n = 2
  ref = C_element
FEATURE [App::DocumentObjectGroupPython] H_element086  label="H_element : 048"  # scripted group (container) (typed FeaturePython)
  n = 2
  ref = H_element
FEATURE [App::DocumentObjectGroupPython] F_element016  label="F_element : 007"  # scripted group (container) (typed FeaturePython)
  n = 2
  ref = F_element
FEATURE [App::DocumentObjectGroupPython] G4_POLYVINYLIDENE_FLUORIDE  # scripted group (container) (typed FeaturePython)
  Dunit = g/cm3
  Dvalue = 1.76
  Group = -> [C_element094,H_element086,F_element016]
  conduct = 2
  density = 1
  expand = 3
  formula = G4_POLYVINYLIDENE_FLUORIDE
  name = G4_POLYVINYLIDENE_FLUORIDE
  specific = 4
FEATURE [App::DocumentObjectGroupPython] C_element095  label="C_element : 053"  # scripted group (container) (typed FeaturePython)
  n = 6
  ref = C_element
FEATURE [App::DocumentObjectGroupPython] H_element087  label="H_element : 9"  # scripted group (container) (typed FeaturePython)
  n = 9
  ref = H_element
FEATURE [App::DocumentObjectGroupPython] N_element037  label="N_element : 016"  # scripted group (container) (typed FeaturePython)
  n = 1
  ref = N_element
FEATURE [App::DocumentObjectGroupPython] O_element084  label="O_element : 045"  # scripted group (container) (typed FeaturePython)
  n = 1
  ref = O_element
FEATURE [App::DocumentObjectGroupPython] G4_POLYVINYL_PYRROLIDONE  # scripted group (container) (typed FeaturePython)
  Dunit = g/cm3
  Dvalue = 1.25
  Group = -> [C_element095,H_element087,N_element037,O_element084]
  conduct = 2
  density = 1
  expand = 3
  formula = G4_POLYVINYL_PYRROLIDONE
  name = G4_POLYVINYL_PYRROLIDONE
  specific = 4
FEATURE [App::DocumentObjectGroupPython] K_element008  label="K_element : 1"  # scripted group (container) (typed FeaturePython)
  n = 1
  ref = K_element
FEATURE [App::DocumentObjectGroupPython] I_element006  label="I_element : 003"  # scripted group (container) (typed FeaturePython)
  n = 1
  ref = I_element
FEATURE [App::DocumentObjectGroupPython] G4_POTASSIUM_IODIDE  # scripted group (container) (typed FeaturePython)
  Dunit = g/cm3
  Dvalue = 3.13
  Group = -> [K_element008,I_element006]
  conduct = 2
  density = 1
  expand = 3
  formula = G4_POTASSIUM_IODIDE
  name = G4_POTASSIUM_IODIDE
  specific = 4
FEATURE [App::DocumentObjectGroupPython] K_element009  label="K_element : 2"  # scripted group (container) (typed FeaturePython)
  n = 2
  ref = K_element
FEATURE [App::DocumentObjectGroupPython] O_element085  label="O_element : 046"  # scripted group (container) (typed FeaturePython)
  n = 1
  ref = O_element
FEATURE [App::DocumentObjectGroupPython] G4_POTASSIUM_OXIDE  # scripted group (container) (typed FeaturePython)
  Dunit = g/cm3
  Dvalue = 2.32
  Group = -> [K_element009,O_element085]
  conduct = 2
  density = 1
  expand = 3
  formula = G4_POTASSIUM_OXIDE
  name = G4_POTASSIUM_OXIDE
  specific = 4
FEATURE [App::DocumentObjectGroupPython] C_element096  label="C_element : 054"  # scripted group (container) (typed FeaturePython)
  n = 3
  ref = C_element
FEATURE [App::DocumentObjectGroupPython] H_element088  label="H_element : 049"  # scripted group (container) (typed FeaturePython)
  n = 8
  ref = H_element
FEATURE [App::DocumentObjectGroupPython] G4_PROPANE  # scripted group (container) (typed FeaturePython)
  Dunit = g/cm3
  Dvalue = 0.00187939
  Group = -> [C_element096,H_element088]
  conduct = 2
  density = 1
  expand = 3
  formula = G4_PROPANE
  name = G4_PROPANE
  specific = 4
FEATURE [App::DocumentObjectGroupPython] C_element097  label="C_element : 055"  # scripted group (container) (typed FeaturePython)
  n = 3
  ref = C_element
FEATURE [App::DocumentObjectGroupPython] H_element089  label="H_element : 050"  # scripted group (container) (typed FeaturePython)
  n = 8
  ref = H_element
FEATURE [App::DocumentObjectGroupPython] G4_lPROPANE  # scripted group (container) (typed FeaturePython)
  Dunit = g/cm3
  Dvalue = 0.43
  Group = -> [C_element097,H_element089]
  conduct = 2
  density = 1
  expand = 3
  formula = G4_lPROPANE
  name = G4_lPROPANE
  specific = 4
FEATURE [App::DocumentObjectGroupPython] C_element098  label="C_element : 056"  # scripted group (container) (typed FeaturePython)
  n = 3
  ref = C_element
FEATURE [App::DocumentObjectGroupPython] H_element090  label="H_element : 051"  # scripted group (container) (typed FeaturePython)
  n = 8
  ref = H_element
FEATURE [App::DocumentObjectGroupPython] O_element086  label="O_element : 047"  # scripted group (container) (typed FeaturePython)
  n = 1
  ref = O_element
FEATURE [App::DocumentObjectGroupPython] G4_N_PROPYL_ALCOHOL  label="G4_N-PROPYL_ALCOHOL"  # scripted group (container) (typed FeaturePython)
  Dunit = g/cm3
  Dvalue = 0.8035
  Group = -> [C_element098,H_element090,O_element086]
  conduct = 2
  density = 1
  expand = 3
  formula = G4_N-PROPYL_ALCOHOL
  name = G4_N-PROPYL_ALCOHOL
  specific = 4
FEATURE [App::DocumentObjectGroupPython] C_element099  label="C_element : 057"  # scripted group (container) (typed FeaturePython)
  n = 5
  ref = C_element
FEATURE [App::DocumentObjectGroupPython] H_element091  label="H_element : 052"  # scripted group (container) (typed FeaturePython)
  n = 5
  ref = H_element
FEATURE [App::DocumentObjectGroupPython] N_element038  label="N_element : 017"  # scripted group (container) (typed FeaturePython)
  n = 1
  ref = N_element
FEATURE [App::DocumentObjectGroupPython] G4_PYRIDINE  # scripted group (container) (typed FeaturePython)
  Dunit = g/cm3
  Dvalue = 0.9819
  Group = -> [C_element099,H_element091,N_element038]
  conduct = 2
  density = 1
  expand = 3
  formula = G4_PYRIDINE
  name = G4_PYRIDINE
  specific = 4
FEATURE [App::DocumentObjectGroupPython] H_element092  label="H_element : 0.144"  # scripted group (container) (typed FeaturePython)
  n = 0.143711
FEATURE [App::DocumentObjectGroupPython] C_element100  label="C_element : 0.856"  # scripted group (container) (typed FeaturePython)
  n = 0.856289
FEATURE [App::DocumentObjectGroupPython] G4_RUBBER_BUTYL  # scripted group (container) (typed FeaturePython)
  Dunit = g/cm3
  Dvalue = 0.92
  Group = -> [H_element092,C_element100]
  conduct = 2
  density = 1
  expand = 3
  formula = G4_RUBBER_BUTYL
  name = G4_RUBBER_BUTYL
  specific = 4
FEATURE [App::DocumentObjectGroupPython] H_element093  label="H_element : 0.118"  # scripted group (container) (typed FeaturePython)
  n = 0.118371
FEATURE [App::DocumentObjectGroupPython] C_element101  label="C_element : 0.882"  # scripted group (container) (typed FeaturePython)
  n = 0.881629
FEATURE [App::DocumentObjectGroupPython] G4_RUBBER_NATURAL  # scripted group (container) (typed FeaturePython)
  Dunit = g/cm3
  Dvalue = 0.92
  Group = -> [H_element093,C_element101]
  conduct = 2
  density = 1
  expand = 3
  formula = G4_RUBBER_NATURAL
  name = G4_RUBBER_NATURAL
  specific = 4
FEATURE [App::DocumentObjectGroupPython] H_element094  label="H_element : 0.145"  # scripted group (container) (typed FeaturePython)
  n = 0.05692
FEATURE [App::DocumentObjectGroupPython] C_element102  label="C_element : 0.543"  # scripted group (container) (typed FeaturePython)
  n = 0.542646
FEATURE [App::DocumentObjectGroupPython] Cl_element021  label="Cl_element : 0.400"  # scripted group (container) (typed FeaturePython)
  n = 0.400434
FEATURE [App::DocumentObjectGroupPython] G4_RUBBER_NEOPRENE  # scripted group (container) (typed FeaturePython)
  Dunit = g/cm3
  Dvalue = 1.23
  Group = -> [H_element094,C_element102,Cl_element021]
  conduct = 2
  density = 1
  expand = 3
  formula = G4_RUBBER_NEOPRENE
  name = G4_RUBBER_NEOPRENE
  specific = 4
FEATURE [App::DocumentObjectGroupPython] Si_element006  label="Si_element : 1"  # scripted group (container) (typed FeaturePython)
  n = 1
  ref = Si_element
FEATURE [App::DocumentObjectGroupPython] O_element087  label="O_element : 048"  # scripted group (container) (typed FeaturePython)
  n = 2
  ref = O_element
FEATURE [App::DocumentObjectGroupPython] G4_SILICON_DIOXIDE  # scripted group (container) (typed FeaturePython)
  Dunit = g/cm3
  Dvalue = 2.32
  Group = -> [Si_element006,O_element087]
  conduct = 2
  density = 1
  expand = 3
  formula = G4_SILICON_DIOXIDE
  name = G4_SILICON_DIOXIDE
  specific = 4
FEATURE [App::DocumentObjectGroupPython] Ag_element002  label="Ag_element : 1"  # scripted group (container) (typed FeaturePython)
  n = 1
  ref = Ag_element
FEATURE [App::DocumentObjectGroupPython] Br_element005  label="Br_element : 003"  # scripted group (container) (typed FeaturePython)
  n = 1
  ref = Br_element
FEATURE [App::DocumentObjectGroupPython] G4_SILVER_BROMIDE  # scripted group (container) (typed FeaturePython)
  Dunit = g/cm3
  Dvalue = 6.473
  Group = -> [Ag_element002,Br_element005]
  conduct = 2
  density = 1
  expand = 3
  formula = G4_SILVER_BROMIDE
  name = G4_SILVER_BROMIDE
  specific = 4
FEATURE [App::DocumentObjectGroupPython] Ag_element003  label="Ag_element : 002"  # scripted group (container) (typed FeaturePython)
  n = 1
  ref = Ag_element
FEATURE [App::DocumentObjectGroupPython] Cl_element022  label="Cl_element : 011"  # scripted group (container) (typed FeaturePython)
  n = 1
  ref = Cl_element
FEATURE [App::DocumentObjectGroupPython] G4_SILVER_CHLORIDE  # scripted group (container) (typed FeaturePython)
  Dunit = g/cm3
  Dvalue = 5.56
  Group = -> [Ag_element003,Cl_element022]
  conduct = 2
  density = 1
  expand = 3
  formula = G4_SILVER_CHLORIDE
  name = G4_SILVER_CHLORIDE
  specific = 4
FEATURE [App::DocumentObjectGroupPython] Br_element006  label="Br_element : 0.423"  # scripted group (container) (typed FeaturePython)
  n = 0.422895
FEATURE [App::DocumentObjectGroupPython] Ag_element004  label="Ag_element : 0.574"  # scripted group (container) (typed FeaturePython)
  n = 0.573748
FEATURE [App::DocumentObjectGroupPython] I_element007  label="I_element : 0.649"  # scripted group (container) (typed FeaturePython)
  n = 0.003357
FEATURE [App::DocumentObjectGroupPython] G4_SILVER_HALIDES  # scripted group (container) (typed FeaturePython)
  Dunit = g/cm3
  Dvalue = 6.47
  Group = -> [Br_element006,Ag_element004,I_element007]
  conduct = 2
  density = 1
  expand = 3
  formula = G4_SILVER_HALIDES
  name = G4_SILVER_HALIDES
  specific = 4
FEATURE [App::DocumentObjectGroupPython] Ag_element005  label="Ag_element : 003"  # scripted group (container) (typed FeaturePython)
  n = 1
  ref = Ag_element
FEATURE [App::DocumentObjectGroupPython] I_element008  label="I_element : 004"  # scripted group (container) (typed FeaturePython)
  n = 1
  ref = I_element
FEATURE [App::DocumentObjectGroupPython] G4_SILVER_IODIDE  # scripted group (container) (typed FeaturePython)
  Dunit = g/cm3
  Dvalue = 6.01
  Group = -> [Ag_element005,I_element008]
  conduct = 2
  density = 1
  expand = 3
  formula = G4_SILVER_IODIDE
  name = G4_SILVER_IODIDE
  specific = 4
FEATURE [App::DocumentObjectGroupPython] H_element095  label="H_element : 0.100"  # scripted group (container) (typed FeaturePython)
  n = 0.1
FEATURE [App::DocumentObjectGroupPython] C_element103  label="C_element : 0.204"  # scripted group (container) (typed FeaturePython)
  n = 0.204
FEATURE [App::DocumentObjectGroupPython] N_element039  label="N_element : 0.759"  # scripted group (container) (typed FeaturePython)
  n = 0.042
FEATURE [App::DocumentObjectGroupPython] O_element088  label="O_element : 0.645"  # scripted group (container) (typed FeaturePython)
  n = 0.645
FEATURE [App::DocumentObjectGroupPython] Na_element013  label="Na_element : 0.100"  # scripted group (container) (typed FeaturePython)
  n = 0.002
FEATURE [App::DocumentObjectGroupPython] P_element009  label="P_element : 0.107"  # scripted group (container) (typed FeaturePython)
  n = 0.001
FEATURE [App::DocumentObjectGroupPython] S_element020  label="S_element : 0.021"  # scripted group (container) (typed FeaturePython)
  n = 0.002
FEATURE [App::DocumentObjectGroupPython] Cl_element023  label="Cl_element : 0.590"  # scripted group (container) (typed FeaturePython)
  n = 0.003
FEATURE [App::DocumentObjectGroupPython] K_element010  label="K_element : 0.001"  # scripted group (container) (typed FeaturePython)
  n = 0.001
FEATURE [App::DocumentObjectGroupPython] G4_SKIN_ICRP  # scripted group (container) (typed FeaturePython)
  Dunit = g/cm3
  Dvalue = 1.09
  Group = -> [H_element095,C_element103,N_element039,O_element088,Na_element013,P_element009,S_element020,Cl_element023,K_element010]
  conduct = 2
  density = 1
  expand = 3
  formula = G4_SKIN_ICRP
  name = G4_SKIN_ICRP
  specific = 4
FEATURE [App::DocumentObjectGroupPython] Na_element014  label="Na_element : 2"  # scripted group (container) (typed FeaturePython)
  n = 2
  ref = Na_element
FEATURE [App::DocumentObjectGroupPython] C_element104  label="C_element : 058"  # scripted group (container) (typed FeaturePython)
  n = 1
  ref = C_element
FEATURE [App::DocumentObjectGroupPython] O_element089  label="O_element : 049"  # scripted group (container) (typed FeaturePython)
  n = 3
  ref = O_element
FEATURE [App::DocumentObjectGroupPython] G4_SODIUM_CARBONATE  # scripted group (container) (typed FeaturePython)
  Dunit = g/cm3
  Dvalue = 2.532
  Group = -> [Na_element014,C_element104,O_element089]
  conduct = 2
  density = 1
  expand = 3
  formula = G4_SODIUM_CARBONATE
  name = G4_SODIUM_CARBONATE
  specific = 4
FEATURE [App::DocumentObjectGroupPython] Na_element015  label="Na_element : 1"  # scripted group (container) (typed FeaturePython)
  n = 1
  ref = Na_element
FEATURE [App::DocumentObjectGroupPython] I_element009  label="I_element : 005"  # scripted group (container) (typed FeaturePython)
  n = 1
  ref = I_element
FEATURE [App::DocumentObjectGroupPython] G4_SODIUM_IODIDE  # scripted group (container) (typed FeaturePython)
  Dunit = g/cm3
  Dvalue = 3.667
  Group = -> [Na_element015,I_element009]
  conduct = 2
  density = 1
  expand = 3
  formula = G4_SODIUM_IODIDE
  name = G4_SODIUM_IODIDE
  specific = 4
FEATURE [App::DocumentObjectGroupPython] Na_element016  label="Na_element : 003"  # scripted group (container) (typed FeaturePython)
  n = 2
  ref = Na_element
FEATURE [App::DocumentObjectGroupPython] O_element090  label="O_element : 050"  # scripted group (container) (typed FeaturePython)
  n = 1
  ref = O_element
FEATURE [App::DocumentObjectGroupPython] G4_SODIUM_MONOXIDE  # scripted group (container) (typed FeaturePython)
  Dunit = g/cm3
  Dvalue = 2.27
  Group = -> [Na_element016,O_element090]
  conduct = 2
  density = 1
  expand = 3
  formula = G4_SODIUM_MONOXIDE
  name = G4_SODIUM_MONOXIDE
  specific = 4
FEATURE [App::DocumentObjectGroupPython] Na_element017  label="Na_element : 004"  # scripted group (container) (typed FeaturePython)
  n = 1
  ref = Na_element
FEATURE [App::DocumentObjectGroupPython] N_element040  label="N_element : 018"  # scripted group (container) (typed FeaturePython)
  n = 1
  ref = N_element
FEATURE [App::DocumentObjectGroupPython] O_element091  label="O_element : 051"  # scripted group (container) (typed FeaturePython)
  n = 3
  ref = O_element
FEATURE [App::DocumentObjectGroupPython] G4_SODIUM_NITRATE  # scripted group (container) (typed FeaturePython)
  Dunit = g/cm3
  Dvalue = 2.261
  Group = -> [Na_element017,N_element040,O_element091]
  conduct = 2
  density = 1
  expand = 3
  formula = G4_SODIUM_NITRATE
  name = G4_SODIUM_NITRATE
  specific = 4
FEATURE [App::DocumentObjectGroupPython] C_element105  label="C_element : 059"  # scripted group (container) (typed FeaturePython)
  n = 14
  ref = C_element
FEATURE [App::DocumentObjectGroupPython] H_element096  label="H_element : 053"  # scripted group (container) (typed FeaturePython)
  n = 12
  ref = H_element
FEATURE [App::DocumentObjectGroupPython] G4_STILBENE  # scripted group (container) (typed FeaturePython)
  Dunit = g/cm3
  Dvalue = 0.9707
  Group = -> [C_element105,H_element096]
  conduct = 2
  density = 1
  expand = 3
  formula = G4_STILBENE
  name = G4_STILBENE
  specific = 4
FEATURE [App::DocumentObjectGroupPython] C_element106  label="C_element : 12"  # scripted group (container) (typed FeaturePython)
  n = 12
  ref = C_element
FEATURE [App::DocumentObjectGroupPython] H_element097  label="H_element : 22"  # scripted group (container) (typed FeaturePython)
  n = 22
  ref = H_element
FEATURE [App::DocumentObjectGroupPython] O_element092  label="O_element : 11"  # scripted group (container) (typed FeaturePython)
  n = 11
  ref = O_element
FEATURE [App::DocumentObjectGroupPython] G4_SUCROSE  # scripted group (container) (typed FeaturePython)
  Dunit = g/cm3
  Dvalue = 1.5805
  Group = -> [C_element106,H_element097,O_element092]
  conduct = 2
  density = 1
  expand = 3
  formula = G4_SUCROSE
  name = G4_SUCROSE
  specific = 4
FEATURE [App::DocumentObjectGroupPython] C_element107  label="C_element : 18"  # scripted group (container) (typed FeaturePython)
  n = 18
  ref = C_element
FEATURE [App::DocumentObjectGroupPython] H_element098  label="H_element : 054"  # scripted group (container) (typed FeaturePython)
  n = 14
  ref = H_element
FEATURE [App::DocumentObjectGroupPython] G4_TERPHENYL  # scripted group (container) (typed FeaturePython)
  Dunit = g/cm3
  Dvalue = 1.24
  Group = -> [C_element107,H_element098]
  conduct = 2
  density = 1
  expand = 3
  formula = G4_TERPHENYL
  name = G4_TERPHENYL
  specific = 4
FEATURE [App::DocumentObjectGroupPython] H_element099  label="H_element : 0.146"  # scripted group (container) (typed FeaturePython)
  n = 0.106
FEATURE [App::DocumentObjectGroupPython] C_element108  label="C_element : 0.883"  # scripted group (container) (typed FeaturePython)
  n = 0.099
FEATURE [App::DocumentObjectGroupPython] N_element041  label="N_element : 0.020"  # scripted group (container) (typed FeaturePython)
  n = 0.02
FEATURE [App::DocumentObjectGroupPython] O_element093  label="O_element : 0.766"  # scripted group (container) (typed FeaturePython)
  n = 0.766
FEATURE [App::DocumentObjectGroupPython] Na_element018  label="Na_element : 0.101"  # scripted group (container) (typed FeaturePython)
  n = 0.002
FEATURE [App::DocumentObjectGroupPython] P_element010  label="P_element : 0.108"  # scripted group (container) (typed FeaturePython)
  n = 0.001
FEATURE [App::DocumentObjectGroupPython] S_element021  label="S_element : 0.022"  # scripted group (container) (typed FeaturePython)
  n = 0.002
FEATURE [App::DocumentObjectGroupPython] Cl_element024  label="Cl_element : 0.002"  # scripted group (container) (typed FeaturePython)
  n = 0.002
FEATURE [App::DocumentObjectGroupPython] K_element011  label="K_element : 0.017"  # scripted group (container) (typed FeaturePython)
  n = 0.002
FEATURE [App::DocumentObjectGroupPython] G4_TESTIS_ICRP  # scripted group (container) (typed FeaturePython)
  Dunit = g/cm3
  Dvalue = 1.04
  Group = -> [H_element099,C_element108,N_element041,O_element093,Na_element018,P_element010,S_element021,Cl_element024,K_element011]
  conduct = 2
  density = 1
  expand = 3
  formula = G4_TESTIS_ICRP
  name = G4_TESTIS_ICRP
  specific = 4
FEATURE [App::DocumentObjectGroupPython] C_element109  label="C_element : 060"  # scripted group (container) (typed FeaturePython)
  n = 2
  ref = C_element
FEATURE [App::DocumentObjectGroupPython] Cl_element025  label="Cl_element : 012"  # scripted group (container) (typed FeaturePython)
  n = 4
  ref = Cl_element
FEATURE [App::DocumentObjectGroupPython] G4_TETRACHLOROETHYLENE  # scripted group (container) (typed FeaturePython)
  Dunit = g/cm3
  Dvalue = 1.625
  Group = -> [C_element109,Cl_element025]
  conduct = 2
  density = 1
  expand = 3
  formula = G4_TETRACHLOROETHYLENE
  name = G4_TETRACHLOROETHYLENE
  specific = 4
FEATURE [App::DocumentObjectGroupPython] Tl_element001  label="Tl_element : 1"  # scripted group (container) (typed FeaturePython)
  n = 1
  ref = Tl_element
FEATURE [App::DocumentObjectGroupPython] Cl_element026  label="Cl_element : 013"  # scripted group (container) (typed FeaturePython)
  n = 1
  ref = Cl_element
FEATURE [App::DocumentObjectGroupPython] G4_THALLIUM_CHLORIDE  # scripted group (container) (typed FeaturePython)
  Dunit = g/cm3
  Dvalue = 7.004
  Group = -> [Tl_element001,Cl_element026]
  conduct = 2
  density = 1
  expand = 3
  formula = G4_THALLIUM_CHLORIDE
  name = G4_THALLIUM_CHLORIDE
  specific = 4
FEATURE [App::DocumentObjectGroupPython] H_element100  label="H_element : 0.147"  # scripted group (container) (typed FeaturePython)
  n = 0.105
FEATURE [App::DocumentObjectGroupPython] C_element110  label="C_element : 0.256"  # scripted group (container) (typed FeaturePython)
  n = 0.256
FEATURE [App::DocumentObjectGroupPython] N_element042  label="N_element : 0.760"  # scripted group (container) (typed FeaturePython)
  n = 0.027
FEATURE [App::DocumentObjectGroupPython] O_element094  label="O_element : 0.602"  # scripted group (container) (typed FeaturePython)
  n = 0.602
FEATURE [App::DocumentObjectGroupPython] Na_element019  label="Na_element : 0.102"  # scripted group (container) (typed FeaturePython)
  n = 0.001
FEATURE [App::DocumentObjectGroupPython] P_element011  label="P_element : 0.109"  # scripted group (container) (typed FeaturePython)
  n = 0.002
FEATURE [App::DocumentObjectGroupPython] S_element022  label="S_element : 0.023"  # scripted group (container) (typed FeaturePython)
  n = 0.003
FEATURE [App::DocumentObjectGroupPython] Cl_element027  label="Cl_element : 0.591"  # scripted group (container) (typed FeaturePython)
  n = 0.002
FEATURE [App::DocumentObjectGroupPython] K_element012  label="K_element : 0.018"  # scripted group (container) (typed FeaturePython)
  n = 0.002
FEATURE [App::DocumentObjectGroupPython] G4_TISSUE_SOFT_ICRP  # scripted group (container) (typed FeaturePython)
  Dunit = g/cm3
  Dvalue = 1.03
  Group = -> [H_element100,C_element110,N_element042,O_element094,Na_element019,P_element011,S_element022,Cl_element027,K_element012]
  conduct = 2
  density = 1
  expand = 3
  formula = G4_TISSUE_SOFT_ICRP
  name = G4_TISSUE_SOFT_ICRP
  specific = 4
FEATURE [App::DocumentObjectGroupPython] H_element101  label="H_element : 0.148"  # scripted group (container) (typed FeaturePython)
  n = 0.101
FEATURE [App::DocumentObjectGroupPython] C_element111  label="C_element : 0.111"  # scripted group (container) (typed FeaturePython)
  n = 0.111
FEATURE [App::DocumentObjectGroupPython] N_element043  label="N_element : 0.026"  # scripted group (container) (typed FeaturePython)
  n = 0.026
FEATURE [App::DocumentObjectGroupPython] O_element095  label="O_element : 0.762"  # scripted group (container) (typed FeaturePython)
  n = 0.762
FEATURE [App::DocumentObjectGroupPython] G4_TISSUE_SOFT_ICRU_4  label="G4_TISSUE_SOFT_ICRU-4"  # scripted group (container) (typed FeaturePython)
  Dunit = g/cm3
  Dvalue = 1
  Group = -> [H_element101,C_element111,N_element043,O_element095]
  conduct = 2
  density = 1
  expand = 3
  formula = G4_TISSUE_SOFT_ICRU-4
  name = G4_TISSUE_SOFT_ICRU-4
  specific = 4
FEATURE [App::DocumentObjectGroupPython] H_element102  label="H_element : 0.149"  # scripted group (container) (typed FeaturePython)
  n = 0.101869
FEATURE [App::DocumentObjectGroupPython] C_element112  label="C_element : 0.456"  # scripted group (container) (typed FeaturePython)
  n = 0.456179
FEATURE [App::DocumentObjectGroupPython] N_element044  label="N_element : 0.761"  # scripted group (container) (typed FeaturePython)
  n = 0.035172
FEATURE [App::DocumentObjectGroupPython] O_element096  label="O_element : 0.407"  # scripted group (container) (typed FeaturePython)
  n = 0.40678
FEATURE [App::DocumentObjectGroupPython] G4_TISSUE_METHANE  label="G4_TISSUE-METHANE"  # scripted group (container) (typed FeaturePython)
  Dunit = g/cm3
  Dvalue = 0.00106409
  Group = -> [H_element102,C_element112,N_element044,O_element096]
  conduct = 2
  density = 1
  expand = 3
  formula = G4_TISSUE-METHANE
  name = G4_TISSUE-METHANE
  specific = 4
FEATURE [App::DocumentObjectGroupPython] H_element103  label="H_element : 0.103"  # scripted group (container) (typed FeaturePython)
  n = 0.102672
FEATURE [App::DocumentObjectGroupPython] C_element113  label="C_element : 0.569"  # scripted group (container) (typed FeaturePython)
  n = 0.56894
FEATURE [App::DocumentObjectGroupPython] N_element045  label="N_element : 0.762"  # scripted group (container) (typed FeaturePython)
  n = 0.035022
FEATURE [App::DocumentObjectGroupPython] O_element097  label="O_element : 0.293"  # scripted group (container) (typed FeaturePython)
  n = 0.293366
FEATURE [App::DocumentObjectGroupPython] G4_TISSUE_PROPANE  label="G4_TISSUE-PROPANE"  # scripted group (container) (typed FeaturePython)
  Dunit = g/cm3
  Dvalue = 0.00182628
  Group = -> [H_element103,C_element113,N_element045,O_element097]
  conduct = 2
  density = 1
  expand = 3
  formula = G4_TISSUE-PROPANE
  name = G4_TISSUE-PROPANE
  specific = 4
FEATURE [App::DocumentObjectGroupPython] Ti_element003  label="Ti_element : 1"  # scripted group (container) (typed FeaturePython)
  n = 1
  ref = Ti_element
FEATURE [App::DocumentObjectGroupPython] O_element098  label="O_element : 052"  # scripted group (container) (typed FeaturePython)
  n = 2
  ref = O_element
FEATURE [App::DocumentObjectGroupPython] G4_TITANIUM_DIOXIDE  # scripted group (container) (typed FeaturePython)
  Dunit = g/cm3
  Dvalue = 4.26
  Group = -> [Ti_element003,O_element098]
  conduct = 2
  density = 1
  expand = 3
  formula = G4_TITANIUM_DIOXIDE
  name = G4_TITANIUM_DIOXIDE
  specific = 4
FEATURE [App::DocumentObjectGroupPython] C_element114  label="C_element : 061"  # scripted group (container) (typed FeaturePython)
  n = 7
  ref = C_element
FEATURE [App::DocumentObjectGroupPython] H_element104  label="H_element : 055"  # scripted group (container) (typed FeaturePython)
  n = 8
  ref = H_element
FEATURE [App::DocumentObjectGroupPython] G4_TOLUENE  # scripted group (container) (typed FeaturePython)
  Dunit = g/cm3
  Dvalue = 0.8669
  Group = -> [C_element114,H_element104]
  conduct = 2
  density = 1
  expand = 3
  formula = G4_TOLUENE
  name = G4_TOLUENE
  specific = 4
FEATURE [App::DocumentObjectGroupPython] C_element115  label="C_element : 062"  # scripted group (container) (typed FeaturePython)
  n = 2
  ref = C_element
FEATURE [App::DocumentObjectGroupPython] H_element105  label="H_element : 056"  # scripted group (container) (typed FeaturePython)
  n = 1
  ref = H_element
FEATURE [App::DocumentObjectGroupPython] Cl_element028  label="Cl_element : 014"  # scripted group (container) (typed FeaturePython)
  n = 3
  ref = Cl_element
FEATURE [App::DocumentObjectGroupPython] G4_TRICHLOROETHYLENE  # scripted group (container) (typed FeaturePython)
  Dunit = g/cm3
  Dvalue = 1.46
  Group = -> [C_element115,H_element105,Cl_element028]
  conduct = 2
  density = 1
  expand = 3
  formula = G4_TRICHLOROETHYLENE
  name = G4_TRICHLOROETHYLENE
  specific = 4
FEATURE [App::DocumentObjectGroupPython] C_element116  label="C_element : 063"  # scripted group (container) (typed FeaturePython)
  n = 6
  ref = C_element
FEATURE [App::DocumentObjectGroupPython] H_element106  label="H_element : 15"  # scripted group (container) (typed FeaturePython)
  n = 15
  ref = H_element
FEATURE [App::DocumentObjectGroupPython] O_element099  label="O_element : 053"  # scripted group (container) (typed FeaturePython)
  n = 4
  ref = O_element
FEATURE [App::DocumentObjectGroupPython] P_element012  label="P_element : 1"  # scripted group (container) (typed FeaturePython)
  n = 1
  ref = P_element
FEATURE [App::DocumentObjectGroupPython] G4_TRIETHYL_PHOSPHATE  # scripted group (container) (typed FeaturePython)
  Dunit = g/cm3
  Dvalue = 1.07
  Group = -> [C_element116,H_element106,O_element099,P_element012]
  conduct = 2
  density = 1
  expand = 3
  formula = G4_TRIETHYL_PHOSPHATE
  name = G4_TRIETHYL_PHOSPHATE
  specific = 4
FEATURE [App::DocumentObjectGroupPython] W_element003  label="W_element : 003"  # scripted group (container) (typed FeaturePython)
  n = 1
  ref = W_element
FEATURE [App::DocumentObjectGroupPython] F_element017  label="F_element : 6"  # scripted group (container) (typed FeaturePython)
  n = 6
  ref = F_element
FEATURE [App::DocumentObjectGroupPython] G4_TUNGSTEN_HEXAFLUORIDE  # scripted group (container) (typed FeaturePython)
  Dunit = g/cm3
  Dvalue = 2.4
  Group = -> [W_element003,F_element017]
  conduct = 2
  density = 1
  expand = 3
  formula = G4_TUNGSTEN_HEXAFLUORIDE
  name = G4_TUNGSTEN_HEXAFLUORIDE
  specific = 4
FEATURE [App::DocumentObjectGroupPython] U_element001  label="U_element : 1"  # scripted group (container) (typed FeaturePython)
  n = 1
  ref = U_element
FEATURE [App::DocumentObjectGroupPython] C_element117  label="C_element : 064"  # scripted group (container) (typed FeaturePython)
  n = 2
  ref = C_element
FEATURE [App::DocumentObjectGroupPython] G4_URANIUM_DICARBIDE  # scripted group (container) (typed FeaturePython)
  Dunit = g/cm3
  Dvalue = 11.28
  Group = -> [U_element001,C_element117]
  conduct = 2
  density = 1
  expand = 3
  formula = G4_URANIUM_DICARBIDE
  name = G4_URANIUM_DICARBIDE
  specific = 4
FEATURE [App::DocumentObjectGroupPython] U_element002  label="U_element : 002"  # scripted group (container) (typed FeaturePython)
  n = 1
  ref = U_element
FEATURE [App::DocumentObjectGroupPython] C_element118  label="C_element : 065"  # scripted group (container) (typed FeaturePython)
  n = 1
  ref = C_element
FEATURE [App::DocumentObjectGroupPython] G4_URANIUM_MONOCARBIDE  # scripted group (container) (typed FeaturePython)
  Dunit = g/cm3
  Dvalue = 13.63
  Group = -> [U_element002,C_element118]
  conduct = 2
  density = 1
  expand = 3
  formula = G4_URANIUM_MONOCARBIDE
  name = G4_URANIUM_MONOCARBIDE
  specific = 4
FEATURE [App::DocumentObjectGroupPython] U_element003  label="U_element : 003"  # scripted group (container) (typed FeaturePython)
  n = 1
  ref = U_element
FEATURE [App::DocumentObjectGroupPython] O_element100  label="O_element : 054"  # scripted group (container) (typed FeaturePython)
  n = 2
  ref = O_element
FEATURE [App::DocumentObjectGroupPython] G4_URANIUM_OXIDE  # scripted group (container) (typed FeaturePython)
  Dunit = g/cm3
  Dvalue = 10.96
  Group = -> [U_element003,O_element100]
  conduct = 2
  density = 1
  expand = 3
  formula = G4_URANIUM_OXIDE
  name = G4_URANIUM_OXIDE
  specific = 4
FEATURE [App::DocumentObjectGroupPython] C_element119  label="C_element : 066"  # scripted group (container) (typed FeaturePython)
  n = 1
  ref = C_element
FEATURE [App::DocumentObjectGroupPython] H_element107  label="H_element : 057"  # scripted group (container) (typed FeaturePython)
  n = 4
  ref = H_element
FEATURE [App::DocumentObjectGroupPython] N_element046  label="N_element : 019"  # scripted group (container) (typed FeaturePython)
  n = 2
  ref = N_element
FEATURE [App::DocumentObjectGroupPython] O_element101  label="O_element : 055"  # scripted group (container) (typed FeaturePython)
  n = 1
  ref = O_element
FEATURE [App::DocumentObjectGroupPython] G4_UREA  # scripted group (container) (typed FeaturePython)
  Dunit = g/cm3
  Dvalue = 1.323
  Group = -> [C_element119,H_element107,N_element046,O_element101]
  conduct = 2
  density = 1
  expand = 3
  formula = G4_UREA
  name = G4_UREA
  specific = 4
FEATURE [App::DocumentObjectGroupPython] C_element120  label="C_element : 067"  # scripted group (container) (typed FeaturePython)
  n = 5
  ref = C_element
FEATURE [App::DocumentObjectGroupPython] H_element108  label="H_element : 058"  # scripted group (container) (typed FeaturePython)
  n = 11
  ref = H_element
FEATURE [App::DocumentObjectGroupPython] N_element047  label="N_element : 020"  # scripted group (container) (typed FeaturePython)
  n = 1
  ref = N_element
FEATURE [App::DocumentObjectGroupPython] O_element102  label="O_element : 056"  # scripted group (container) (typed FeaturePython)
  n = 2
  ref = O_element
FEATURE [App::DocumentObjectGroupPython] G4_VALINE  # scripted group (container) (typed FeaturePython)
  Dunit = g/cm3
  Dvalue = 1.23
  Group = -> [C_element120,H_element108,N_element047,O_element102]
  conduct = 2
  density = 1
  expand = 3
  formula = G4_VALINE
  name = G4_VALINE
  specific = 4
FEATURE [App::DocumentObjectGroupPython] H_element109  label="H_element : 0.009"  # scripted group (container) (typed FeaturePython)
  n = 0.009417
FEATURE [App::DocumentObjectGroupPython] C_element121  label="C_element : 0.281"  # scripted group (container) (typed FeaturePython)
  n = 0.280555
FEATURE [App::DocumentObjectGroupPython] F_element018  label="F_element : 0.710"  # scripted group (container) (typed FeaturePython)
  n = 0.710028
FEATURE [App::DocumentObjectGroupPython] G4_VITON  # scripted group (container) (typed FeaturePython)
  Dunit = g/cm3
  Dvalue = 1.8
  Group = -> [H_element109,C_element121,F_element018]
  conduct = 2
  density = 1
  expand = 3
  formula = G4_VITON
  name = G4_VITON
  specific = 4
FEATURE [App::DocumentObjectGroupPython] H_element110  label="H_element : 059"  # scripted group (container) (typed FeaturePython)
  n = 2
  ref = H_element
FEATURE [App::DocumentObjectGroupPython] O_element103  label="O_element : 057"  # scripted group (container) (typed FeaturePython)
  n = 1
  ref = O_element
FEATURE [App::DocumentObjectGroupPython] G4_WATER  # scripted group (container) (typed FeaturePython)
  Dunit = g/cm3
  Dvalue = 1
  Group = -> [H_element110,O_element103]
  conduct = 2
  density = 1
  expand = 3
  formula = G4_WATER
  name = G4_WATER
  specific = 4
FEATURE [App::DocumentObjectGroupPython] H_element111  label="H_element : 060"  # scripted group (container) (typed FeaturePython)
  n = 2
  ref = H_element
FEATURE [App::DocumentObjectGroupPython] O_element104  label="O_element : 058"  # scripted group (container) (typed FeaturePython)
  n = 1
  ref = O_element
FEATURE [App::DocumentObjectGroupPython] G4_WATER_VAPOR  # scripted group (container) (typed FeaturePython)
  Dunit = g/cm3
  Dvalue = 0.000756182
  Group = -> [H_element111,O_element104]
  conduct = 2
  density = 1
  expand = 3
  formula = G4_WATER_VAPOR
  name = G4_WATER_VAPOR
  specific = 4
FEATURE [App::DocumentObjectGroupPython] C_element122  label="C_element : 068"  # scripted group (container) (typed FeaturePython)
  n = 8
  ref = C_element
FEATURE [App::DocumentObjectGroupPython] H_element112  label="H_element : 061"  # scripted group (container) (typed FeaturePython)
  n = 10
  ref = H_element
FEATURE [App::DocumentObjectGroupPython] G4_XYLENE  # scripted group (container) (typed FeaturePython)
  Dunit = g/cm3
  Dvalue = 0.87
  Group = -> [C_element122,H_element112]
  conduct = 2
  density = 1
  expand = 3
  formula = G4_XYLENE
  name = G4_XYLENE
  specific = 4
FEATURE [App::DocumentObjectGroupPython] C_element123  label="C_element : 069"  # scripted group (container) (typed FeaturePython)
  n = 1
  ref = C_element
FEATURE [App::DocumentObjectGroupPython] G4_GRAPHITE  # scripted group (container) (typed FeaturePython)
  Dunit = g/cm3
  Dvalue = 2.21
  Group = -> [C_element123]
  conduct = 2
  density = 1
  expand = 3
  formula = G4_GRAPHITE
  name = G4_GRAPHITE
  specific = 4
FEATURE [App::DocumentObjectGroupPython] NIST  # scripted group (container) (typed FeaturePython)
  Group = -> [G4_A_150_TISSUE,G4_ACETONE,G4_ACETYLENE,G4_ADENINE,G4_ADIPOSE_TISSUE_ICRP,G4_AIR,G4_ALANINE,G4_ALUMINUM_OXIDE,G4_AMBER,G4_AMMONIA,G4_ANILINE,G4_ANTHRACENE,G4_B_100_BONE,G4_BAKELITE,G4_BARIUM_FLUORIDE,G4_BARIUM_SULFATE,G4_BENZENE,G4_BERYLLIUM_OXIDE,G4_BGO,G4_BLOOD_ICRP,G4_BONE_COMPACT_ICRU,G4_BONE_CORTICAL_ICRP,G4_BORON_CARBIDE,G4_BORON_OXIDE,G4_BRAIN_ICRP,G4_BUTANE,G4_N_BUTYL_ALCOHOL,G4_C_552,+152 more]
FEATURE [App::DocumentObjectGroupPython] H_element113  label="H_element : 062"  # scripted group (container) (typed FeaturePython)
  n = 1
  ref = H_element
FEATURE [App::DocumentObjectGroupPython] G4_H  # scripted group (container) (typed FeaturePython)
  Dunit = g/cm3
  Dvalue = 8.3748e-05
  Group = -> [H_element113]
  conduct = 2
  density = 1
  expand = 3
  formula = H
  name = G4_H
  specific = 4
FEATURE [App::DocumentObjectGroupPython] He_element001  label="He_element : 1"  # scripted group (container) (typed FeaturePython)
  n = 1
  ref = He_element
FEATURE [App::DocumentObjectGroupPython] G4_He  # scripted group (container) (typed FeaturePython)
  Dunit = g/cm3
  Dvalue = 0.000166322
  Group = -> [He_element001]
  conduct = 2
  density = 1
  expand = 3
  formula = He
  name = G4_He
  specific = 4
FEATURE [App::DocumentObjectGroupPython] Li_element008  label="Li_element : 008"  # scripted group (container) (typed FeaturePython)
  n = 1
  ref = Li_element
FEATURE [App::DocumentObjectGroupPython] G4_Li  # scripted group (container) (typed FeaturePython)
  Dunit = g/cm3
  Dvalue = 0.534
  Group = -> [Li_element008]
  conduct = 2
  density = 1
  expand = 3
  formula = Li
  name = G4_Li
  specific = 4
FEATURE [App::DocumentObjectGroupPython] Be_element002  label="Be_element : 002"  # scripted group (container) (typed FeaturePython)
  n = 1
  ref = Be_element
FEATURE [App::DocumentObjectGroupPython] G4_Be  # scripted group (container) (typed FeaturePython)
  Dunit = g/cm3
  Dvalue = 1.848
  Group = -> [Be_element002]
  conduct = 2
  density = 1
  expand = 3
  formula = Be
  name = G4_Be
  specific = 4
FEATURE [App::DocumentObjectGroupPython] B_element007  label="B_element : 007"  # scripted group (container) (typed FeaturePython)
  n = 1
  ref = B_element
FEATURE [App::DocumentObjectGroupPython] G4_B  # scripted group (container) (typed FeaturePython)
  Dunit = g/cm3
  Dvalue = 2.37
  Group = -> [B_element007]
  conduct = 2
  density = 1
  expand = 3
  formula = B
  name = G4_B
  specific = 4
FEATURE [App::DocumentObjectGroupPython] C_element124  label="C_element : 070"  # scripted group (container) (typed FeaturePython)
  n = 1
  ref = C_element
FEATURE [App::DocumentObjectGroupPython] G4_C  # scripted group (container) (typed FeaturePython)
  Dunit = g/cm3
  Dvalue = 2
  Group = -> [C_element124]
  conduct = 2
  density = 1
  expand = 3
  formula = C
  name = G4_C
  specific = 4
FEATURE [App::DocumentObjectGroupPython] N_element048  label="N_element : 021"  # scripted group (container) (typed FeaturePython)
  n = 1
  ref = N_element
FEATURE [App::DocumentObjectGroupPython] G4_N  # scripted group (container) (typed FeaturePython)
  Dunit = g/cm3
  Dvalue = 0.0011652
  Group = -> [N_element048]
  conduct = 2
  density = 1
  expand = 3
  formula = N
  name = G4_N
  specific = 4
FEATURE [App::DocumentObjectGroupPython] O_element105  label="O_element : 059"  # scripted group (container) (typed FeaturePython)
  n = 1
  ref = O_element
FEATURE [App::DocumentObjectGroupPython] G4_O  # scripted group (container) (typed FeaturePython)
  Dunit = g/cm3
  Dvalue = 0.00133151
  Group = -> [O_element105]
  conduct = 2
  density = 1
  expand = 3
  formula = O
  name = G4_O
  specific = 4
FEATURE [App::DocumentObjectGroupPython] F_element019  label="F_element : 008"  # scripted group (container) (typed FeaturePython)
  n = 1
  ref = F_element
FEATURE [App::DocumentObjectGroupPython] G4_F  # scripted group (container) (typed FeaturePython)
  Dunit = g/cm3
  Dvalue = 0.00158029
  Group = -> [F_element019]
  conduct = 2
  density = 1
  expand = 3
  formula = F
  name = G4_F
  specific = 4
FEATURE [App::DocumentObjectGroupPython] Ne_element001  label="Ne_element : 1"  # scripted group (container) (typed FeaturePython)
  n = 1
  ref = Ne_element
FEATURE [App::DocumentObjectGroupPython] G4_Ne  # scripted group (container) (typed FeaturePython)
  Dunit = g/cm3
  Dvalue = 0.000838505
  Group = -> [Ne_element001]
  conduct = 2
  density = 1
  expand = 3
  formula = Ne
  name = G4_Ne
  specific = 4
FEATURE [App::DocumentObjectGroupPython] Na_element020  label="Na_element : 005"  # scripted group (container) (typed FeaturePython)
  n = 1
  ref = Na_element
FEATURE [App::DocumentObjectGroupPython] G4_Na  # scripted group (container) (typed FeaturePython)
  Dunit = g/cm3
  Dvalue = 0.971
  Group = -> [Na_element020]
  conduct = 2
  density = 1
  expand = 3
  formula = Na
  name = G4_Na
  specific = 4
FEATURE [App::DocumentObjectGroupPython] Mg_element011  label="Mg_element : 005"  # scripted group (container) (typed FeaturePython)
  n = 1
  ref = Mg_element
FEATURE [App::DocumentObjectGroupPython] G4_Mg  # scripted group (container) (typed FeaturePython)
  Dunit = g/cm3
  Dvalue = 1.74
  Group = -> [Mg_element011]
  conduct = 2
  density = 1
  expand = 3
  formula = Mg
  name = G4_Mg
  specific = 4
FEATURE [App::DocumentObjectGroupPython] Al_element004  label="Al_element : 1"  # scripted group (container) (typed FeaturePython)
  n = 1
  ref = Al_element
FEATURE [App::DocumentObjectGroupPython] G4_Al  # scripted group (container) (typed FeaturePython)
  Dunit = g/cm3
  Dvalue = 2.699
  Group = -> [Al_element004]
  conduct = 2
  density = 1
  expand = 3
  formula = Al
  name = G4_Al
  specific = 4
FEATURE [App::DocumentObjectGroupPython] Si_element007  label="Si_element : 002"  # scripted group (container) (typed FeaturePython)
  n = 1
  ref = Si_element
FEATURE [App::DocumentObjectGroupPython] G4_Si  # scripted group (container) (typed FeaturePython)
  Dunit = g/cm3
  Dvalue = 2.33
  Group = -> [Si_element007]
  conduct = 2
  density = 1
  expand = 3
  formula = Si
  name = G4_Si
  specific = 4
FEATURE [App::DocumentObjectGroupPython] P_element013  label="P_element : 002"  # scripted group (container) (typed FeaturePython)
  n = 1
  ref = P_element
FEATURE [App::DocumentObjectGroupPython] G4_P  # scripted group (container) (typed FeaturePython)
  Dunit = g/cm3
  Dvalue = 2.2
  Group = -> [P_element013]
  conduct = 2
  density = 1
  expand = 3
  formula = P
  name = G4_P
  specific = 4
FEATURE [App::DocumentObjectGroupPython] S_element023  label="S_element : 007"  # scripted group (container) (typed FeaturePython)
  n = 1
  ref = S_element
FEATURE [App::DocumentObjectGroupPython] G4_S  # scripted group (container) (typed FeaturePython)
  Dunit = g/cm3
  Dvalue = 2
  Group = -> [S_element023]
  conduct = 2
  density = 1
  expand = 3
  formula = S
  name = G4_S
  specific = 4
FEATURE [App::DocumentObjectGroupPython] Cl_element029  label="Cl_element : 015"  # scripted group (container) (typed FeaturePython)
  n = 1
  ref = Cl_element
FEATURE [App::DocumentObjectGroupPython] G4_Cl  # scripted group (container) (typed FeaturePython)
  Dunit = g/cm3
  Dvalue = 0.00299473
  Group = -> [Cl_element029]
  conduct = 2
  density = 1
  expand = 3
  formula = Cl
  name = G4_Cl
  specific = 4
FEATURE [App::DocumentObjectGroupPython] Ar_element002  label="Ar_element : 1"  # scripted group (container) (typed FeaturePython)
  n = 1
  ref = Ar_element
FEATURE [App::DocumentObjectGroupPython] G4_Ar  # scripted group (container) (typed FeaturePython)
  Dunit = g/cm3
  Dvalue = 0.00166201
  Group = -> [Ar_element002]
  conduct = 2
  density = 1
  expand = 3
  formula = Ar
  name = G4_Ar
  specific = 4
FEATURE [App::DocumentObjectGroupPython] K_element013  label="K_element : 003"  # scripted group (container) (typed FeaturePython)
  n = 1
  ref = K_element
FEATURE [App::DocumentObjectGroupPython] G4_K  # scripted group (container) (typed FeaturePython)
  Dunit = g/cm3
  Dvalue = 0.862
  Group = -> [K_element013]
  conduct = 2
  density = 1
  expand = 3
  formula = K
  name = G4_K
  specific = 4
FEATURE [App::DocumentObjectGroupPython] Ca_element014  label="Ca_element : 007"  # scripted group (container) (typed FeaturePython)
  n = 1
  ref = Ca_element
FEATURE [App::DocumentObjectGroupPython] G4_Ca  # scripted group (container) (typed FeaturePython)
  Dunit = g/cm3
  Dvalue = 1.55
  Group = -> [Ca_element014]
  conduct = 2
  density = 1
  expand = 3
  formula = Ca
  name = G4_Ca
  specific = 4
FEATURE [App::DocumentObjectGroupPython] Sc_element001  label="Sc_element : 1"  # scripted group (container) (typed FeaturePython)
  n = 1
  ref = Sc_element
FEATURE [App::DocumentObjectGroupPython] G4_Sc  # scripted group (container) (typed FeaturePython)
  Dunit = g/cm3
  Dvalue = 2.989
  Group = -> [Sc_element001]
  conduct = 2
  density = 1
  expand = 3
  formula = Sc
  name = G4_Sc
  specific = 4
FEATURE [App::DocumentObjectGroupPython] Ti_element004  label="Ti_element : 002"  # scripted group (container) (typed FeaturePython)
  n = 1
  ref = Ti_element
FEATURE [App::DocumentObjectGroupPython] G4_Ti  # scripted group (container) (typed FeaturePython)
  Dunit = g/cm3
  Dvalue = 4.54
  Group = -> [Ti_element004]
  conduct = 2
  density = 1
  expand = 3
  formula = Ti
  name = G4_Ti
  specific = 4
FEATURE [App::DocumentObjectGroupPython] V_element001  label="V_element : 1"  # scripted group (container) (typed FeaturePython)
  n = 1
  ref = V_element
FEATURE [App::DocumentObjectGroupPython] G4_V  # scripted group (container) (typed FeaturePython)
  Dunit = g/cm3
  Dvalue = 6.11
  Group = -> [V_element001]
  conduct = 2
  density = 1
  expand = 3
  formula = V
  name = G4_V
  specific = 4
FEATURE [App::DocumentObjectGroupPython] Cr_element001  label="Cr_element : 1"  # scripted group (container) (typed FeaturePython)
  n = 1
  ref = Cr_element
FEATURE [App::DocumentObjectGroupPython] G4_Cr  # scripted group (container) (typed FeaturePython)
  Dunit = g/cm3
  Dvalue = 7.18
  Group = -> [Cr_element001]
  conduct = 2
  density = 1
  expand = 3
  formula = Cr
  name = G4_Cr
  specific = 4
FEATURE [App::DocumentObjectGroupPython] Mn_element001  label="Mn_element : 1"  # scripted group (container) (typed FeaturePython)
  n = 1
  ref = Mn_element
FEATURE [App::DocumentObjectGroupPython] G4_Mn  # scripted group (container) (typed FeaturePython)
  Dunit = g/cm3
  Dvalue = 7.44
  Group = -> [Mn_element001]
  conduct = 2
  density = 1
  expand = 3
  formula = Mn
  name = G4_Mn
  specific = 4
FEATURE [App::DocumentObjectGroupPython] Fe_element007  label="Fe_element : 004"  # scripted group (container) (typed FeaturePython)
  n = 1
  ref = Fe_element
FEATURE [App::DocumentObjectGroupPython] G4_Fe  # scripted group (container) (typed FeaturePython)
  Dunit = g/cm3
  Dvalue = 7.874
  Group = -> [Fe_element007]
  conduct = 2
  density = 1
  expand = 3
  formula = Fe
  name = G4_Fe
  specific = 4
FEATURE [App::DocumentObjectGroupPython] Co_element001  label="Co_element : 1"  # scripted group (container) (typed FeaturePython)
  n = 1
  ref = Co_element
FEATURE [App::DocumentObjectGroupPython] G4_Co  # scripted group (container) (typed FeaturePython)
  Dunit = g/cm3
  Dvalue = 8.9
  Group = -> [Co_element001]
  conduct = 2
  density = 1
  expand = 3
  formula = Co
  name = G4_Co
  specific = 4
FEATURE [App::DocumentObjectGroupPython] Ni_element001  label="Ni_element : 1"  # scripted group (container) (typed FeaturePython)
  n = 1
  ref = Ni_element
FEATURE [App::DocumentObjectGroupPython] G4_Ni  # scripted group (container) (typed FeaturePython)
  Dunit = g/cm3
  Dvalue = 8.902
  Group = -> [Ni_element001]
  conduct = 2
  density = 1
  expand = 3
  formula = Ni
  name = G4_Ni
  specific = 4
FEATURE [App::DocumentObjectGroupPython] Cu_element001  label="Cu_element : 1"  # scripted group (container) (typed FeaturePython)
  n = 1
  ref = Cu_element
FEATURE [App::DocumentObjectGroupPython] G4_Cu  # scripted group (container) (typed FeaturePython)
  Dunit = g/cm3
  Dvalue = 8.96
  Group = -> [Cu_element001]
  conduct = 2
  density = 1
  expand = 3
  formula = Cu
  name = G4_Cu
  specific = 4
FEATURE [App::DocumentObjectGroupPython] Zn_element001  label="Zn_element : 1"  # scripted group (container) (typed FeaturePython)
  n = 1
  ref = Zn_element
FEATURE [App::DocumentObjectGroupPython] G4_Zn  # scripted group (container) (typed FeaturePython)
  Dunit = g/cm3
  Dvalue = 7.133
  Group = -> [Zn_element001]
  conduct = 2
  density = 1
  expand = 3
  formula = Zn
  name = G4_Zn
  specific = 4
FEATURE [App::DocumentObjectGroupPython] Ga_element002  label="Ga_element : 002"  # scripted group (container) (typed FeaturePython)
  n = 1
  ref = Ga_element
FEATURE [App::DocumentObjectGroupPython] G4_Ga  # scripted group (container) (typed FeaturePython)
  Dunit = g/cm3
  Dvalue = 5.904
  Group = -> [Ga_element002]
  conduct = 2
  density = 1
  expand = 3
  formula = Ga
  name = G4_Ga
  specific = 4
FEATURE [App::DocumentObjectGroupPython] Ge_element002  label="Ge_element : 1"  # scripted group (container) (typed FeaturePython)
  n = 1
  ref = Ge_element
FEATURE [App::DocumentObjectGroupPython] G4_Ge  # scripted group (container) (typed FeaturePython)
  Dunit = g/cm3
  Dvalue = 5.323
  Group = -> [Ge_element002]
  conduct = 2
  density = 1
  expand = 3
  formula = Ge
  name = G4_Ge
  specific = 4
FEATURE [App::DocumentObjectGroupPython] As_element003  label="As_element : 002"  # scripted group (container) (typed FeaturePython)
  n = 1
  ref = As_element
FEATURE [App::DocumentObjectGroupPython] G4_As  # scripted group (container) (typed FeaturePython)
  Dunit = g/cm3
  Dvalue = 5.73
  Group = -> [As_element003]
  conduct = 2
  density = 1
  expand = 3
  formula = As
  name = G4_As
  specific = 4
FEATURE [App::DocumentObjectGroupPython] Se_element001  label="Se_element : 1"  # scripted group (container) (typed FeaturePython)
  n = 1
  ref = Se_element
FEATURE [App::DocumentObjectGroupPython] G4_Se  # scripted group (container) (typed FeaturePython)
  Dunit = g/cm3
  Dvalue = 4.5
  Group = -> [Se_element001]
  conduct = 2
  density = 1
  expand = 3
  formula = Se
  name = G4_Se
  specific = 4
FEATURE [App::DocumentObjectGroupPython] Br_element007  label="Br_element : 004"  # scripted group (container) (typed FeaturePython)
  n = 1
  ref = Br_element
FEATURE [App::DocumentObjectGroupPython] G4_Br  # scripted group (container) (typed FeaturePython)
  Dunit = g/cm3
  Dvalue = 0.0070721
  Group = -> [Br_element007]
  conduct = 2
  density = 1
  expand = 3
  formula = Br
  name = G4_Br
  specific = 4
FEATURE [App::DocumentObjectGroupPython] Kr_element001  label="Kr_element : 1"  # scripted group (container) (typed FeaturePython)
  n = 1
  ref = Kr_element
FEATURE [App::DocumentObjectGroupPython] G4_Kr  # scripted group (container) (typed FeaturePython)
  Dunit = g/cm3
  Dvalue = 0.00347832
  Group = -> [Kr_element001]
  conduct = 2
  density = 1
  expand = 3
  formula = Kr
  name = G4_Kr
  specific = 4
FEATURE [App::DocumentObjectGroupPython] Rb_element001  label="Rb_element : 1"  # scripted group (container) (typed FeaturePython)
  n = 1
  ref = Rb_element
FEATURE [App::DocumentObjectGroupPython] G4_Rb  # scripted group (container) (typed FeaturePython)
  Dunit = g/cm3
  Dvalue = 1.532
  Group = -> [Rb_element001]
  conduct = 2
  density = 1
  expand = 3
  formula = Rb
  name = G4_Rb
  specific = 4
FEATURE [App::DocumentObjectGroupPython] Sr_element001  label="Sr_element : 1"  # scripted group (container) (typed FeaturePython)
  n = 1
  ref = Sr_element
FEATURE [App::DocumentObjectGroupPython] G4_Sr  # scripted group (container) (typed FeaturePython)
  Dunit = g/cm3
  Dvalue = 2.54
  Group = -> [Sr_element001]
  conduct = 2
  density = 1
  expand = 3
  formula = Sr
  name = G4_Sr
  specific = 4
FEATURE [App::DocumentObjectGroupPython] Y_element001  label="Y_element : 1"  # scripted group (container) (typed FeaturePython)
  n = 1
  ref = Y_element
FEATURE [App::DocumentObjectGroupPython] G4_Y  # scripted group (container) (typed FeaturePython)
  Dunit = g/cm3
  Dvalue = 4.469
  Group = -> [Y_element001]
  conduct = 2
  density = 1
  expand = 3
  formula = Y
  name = G4_Y
  specific = 4
FEATURE [App::DocumentObjectGroupPython] Zr_element001  label="Zr_element : 1"  # scripted group (container) (typed FeaturePython)
  n = 1
  ref = Zr_element
FEATURE [App::DocumentObjectGroupPython] G4_Zr  # scripted group (container) (typed FeaturePython)
  Dunit = g/cm3
  Dvalue = 6.506
  Group = -> [Zr_element001]
  conduct = 2
  density = 1
  expand = 3
  formula = Zr
  name = G4_Zr
  specific = 4
FEATURE [App::DocumentObjectGroupPython] Nb_element001  label="Nb_element : 1"  # scripted group (container) (typed FeaturePython)
  n = 1
  ref = Nb_element
FEATURE [App::DocumentObjectGroupPython] G4_Nb  # scripted group (container) (typed FeaturePython)
  Dunit = g/cm3
  Dvalue = 8.57
  Group = -> [Nb_element001]
  conduct = 2
  density = 1
  expand = 3
  formula = Nb
  name = G4_Nb
  specific = 4
FEATURE [App::DocumentObjectGroupPython] Mo_element001  label="Mo_element : 1"  # scripted group (container) (typed FeaturePython)
  n = 1
  ref = Mo_element
FEATURE [App::DocumentObjectGroupPython] G4_Mo  # scripted group (container) (typed FeaturePython)
  Dunit = g/cm3
  Dvalue = 10.22
  Group = -> [Mo_element001]
  conduct = 2
  density = 1
  expand = 3
  formula = Mo
  name = G4_Mo
  specific = 4
FEATURE [App::DocumentObjectGroupPython] Tc_element001  label="Tc_element : 1"  # scripted group (container) (typed FeaturePython)
  n = 1
  ref = Tc_element
FEATURE [App::DocumentObjectGroupPython] G4_Tc  # scripted group (container) (typed FeaturePython)
  Dunit = g/cm3
  Dvalue = 11.5
  Group = -> [Tc_element001]
  conduct = 2
  density = 1
  expand = 3
  formula = Tc
  name = G4_Tc
  specific = 4
FEATURE [App::DocumentObjectGroupPython] Ru_element001  label="Ru_element : 1"  # scripted group (container) (typed FeaturePython)
  n = 1
  ref = Ru_element
FEATURE [App::DocumentObjectGroupPython] G4_Ru  # scripted group (container) (typed FeaturePython)
  Dunit = g/cm3
  Dvalue = 12.41
  Group = -> [Ru_element001]
  conduct = 2
  density = 1
  expand = 3
  formula = Ru
  name = G4_Ru
  specific = 4
FEATURE [App::DocumentObjectGroupPython] Rh_element001  label="Rh_element : 1"  # scripted group (container) (typed FeaturePython)
  n = 1
  ref = Rh_element
FEATURE [App::DocumentObjectGroupPython] G4_Rh  # scripted group (container) (typed FeaturePython)
  Dunit = g/cm3
  Dvalue = 12.41
  Group = -> [Rh_element001]
  conduct = 2
  density = 1
  expand = 3
  formula = Rh
  name = G4_Rh
  specific = 4
FEATURE [App::DocumentObjectGroupPython] Pd_element001  label="Pd_element : 1"  # scripted group (container) (typed FeaturePython)
  n = 1
  ref = Pd_element
FEATURE [App::DocumentObjectGroupPython] G4_Pd  # scripted group (container) (typed FeaturePython)
  Dunit = g/cm3
  Dvalue = 12.02
  Group = -> [Pd_element001]
  conduct = 2
  density = 1
  expand = 3
  formula = Pd
  name = G4_Pd
  specific = 4
FEATURE [App::DocumentObjectGroupPython] Ag_element006  label="Ag_element : 004"  # scripted group (container) (typed FeaturePython)
  n = 1
  ref = Ag_element
FEATURE [App::DocumentObjectGroupPython] G4_Ag  # scripted group (container) (typed FeaturePython)
  Dunit = g/cm3
  Dvalue = 10.5
  Group = -> [Ag_element006]
  conduct = 2
  density = 1
  expand = 3
  formula = Ag
  name = G4_Ag
  specific = 4
FEATURE [App::DocumentObjectGroupPython] Cd_element003  label="Cd_element : 003"  # scripted group (container) (typed FeaturePython)
  n = 1
  ref = Cd_element
FEATURE [App::DocumentObjectGroupPython] G4_Cd  # scripted group (container) (typed FeaturePython)
  Dunit = g/cm3
  Dvalue = 8.65
  Group = -> [Cd_element003]
  conduct = 2
  density = 1
  expand = 3
  formula = Cd
  name = G4_Cd
  specific = 4
FEATURE [App::DocumentObjectGroupPython] In_element001  label="In_element : 1"  # scripted group (container) (typed FeaturePython)
  n = 1
  ref = In_element
FEATURE [App::DocumentObjectGroupPython] G4_In  # scripted group (container) (typed FeaturePython)
  Dunit = g/cm3
  Dvalue = 7.31
  Group = -> [In_element001]
  conduct = 2
  density = 1
  expand = 3
  formula = In
  name = G4_In
  specific = 4
FEATURE [App::DocumentObjectGroupPython] Sn_element001  label="Sn_element : 1"  # scripted group (container) (typed FeaturePython)
  n = 1
  ref = Sn_element
FEATURE [App::DocumentObjectGroupPython] G4_Sn  # scripted group (container) (typed FeaturePython)
  Dunit = g/cm3
  Dvalue = 7.31
  Group = -> [Sn_element001]
  conduct = 2
  density = 1
  expand = 3
  formula = Sn
  name = G4_Sn
  specific = 4
FEATURE [App::DocumentObjectGroupPython] Sb_element001  label="Sb_element : 1"  # scripted group (container) (typed FeaturePython)
  n = 1
  ref = Sb_element
FEATURE [App::DocumentObjectGroupPython] G4_Sb  # scripted group (container) (typed FeaturePython)
  Dunit = g/cm3
  Dvalue = 6.691
  Group = -> [Sb_element001]
  conduct = 2
  density = 1
  expand = 3
  formula = Sb
  name = G4_Sb
  specific = 4
FEATURE [App::DocumentObjectGroupPython] Te_element002  label="Te_element : 002"  # scripted group (container) (typed FeaturePython)
  n = 1
  ref = Te_element
FEATURE [App::DocumentObjectGroupPython] G4_Te  # scripted group (container) (typed FeaturePython)
  Dunit = g/cm3
  Dvalue = 6.24
  Group = -> [Te_element002]
  conduct = 2
  density = 1
  expand = 3
  formula = Te
  name = G4_Te
  specific = 4
FEATURE [App::DocumentObjectGroupPython] I_element010  label="I_element : 006"  # scripted group (container) (typed FeaturePython)
  n = 1
  ref = I_element
FEATURE [App::DocumentObjectGroupPython] G4_I  # scripted group (container) (typed FeaturePython)
  Dunit = g/cm3
  Dvalue = 4.93
  Group = -> [I_element010]
  conduct = 2
  density = 1
  expand = 3
  formula = I
  name = G4_I
  specific = 4
FEATURE [App::DocumentObjectGroupPython] Xe_element001  label="Xe_element : 1"  # scripted group (container) (typed FeaturePython)
  n = 1
  ref = Xe_element
FEATURE [App::DocumentObjectGroupPython] G4_Xe  # scripted group (container) (typed FeaturePython)
  Dunit = g/cm3
  Dvalue = 0.00548536
  Group = -> [Xe_element001]
  conduct = 2
  density = 1
  expand = 3
  formula = Xe
  name = G4_Xe
  specific = 4
FEATURE [App::DocumentObjectGroupPython] Cs_element003  label="Cs_element : 003"  # scripted group (container) (typed FeaturePython)
  n = 1
  ref = Cs_element
FEATURE [App::DocumentObjectGroupPython] G4_Cs  # scripted group (container) (typed FeaturePython)
  Dunit = g/cm3
  Dvalue = 1.873
  Group = -> [Cs_element003]
  conduct = 2
  density = 1
  expand = 3
  formula = Cs
  name = G4_Cs
  specific = 4
FEATURE [App::DocumentObjectGroupPython] Ba_element003  label="Ba_element : 003"  # scripted group (container) (typed FeaturePython)
  n = 1
  ref = Ba_element
FEATURE [App::DocumentObjectGroupPython] G4_Ba  # scripted group (container) (typed FeaturePython)
  Dunit = g/cm3
  Dvalue = 3.5
  Group = -> [Ba_element003]
  conduct = 2
  density = 1
  expand = 3
  formula = Ba
  name = G4_Ba
  specific = 4
FEATURE [App::DocumentObjectGroupPython] La_element003  label="La_element : 003"  # scripted group (container) (typed FeaturePython)
  n = 1
  ref = La_element
FEATURE [App::DocumentObjectGroupPython] G4_La  # scripted group (container) (typed FeaturePython)
  Dunit = g/cm3
  Dvalue = 6.154
  Group = -> [La_element003]
  conduct = 2
  density = 1
  expand = 3
  formula = La
  name = G4_La
  specific = 4
FEATURE [App::DocumentObjectGroupPython] Ce_element002  label="Ce_element : 1"  # scripted group (container) (typed FeaturePython)
  n = 1
  ref = Ce_element
FEATURE [App::DocumentObjectGroupPython] G4_Ce  # scripted group (container) (typed FeaturePython)
  Dunit = g/cm3
  Dvalue = 6.657
  Group = -> [Ce_element002]
  conduct = 2
  density = 1
  expand = 3
  formula = Ce
  name = G4_Ce
  specific = 4
FEATURE [App::DocumentObjectGroupPython] Pr_element001  label="Pr_element : 1"  # scripted group (container) (typed FeaturePython)
  n = 1
  ref = Pr_element
FEATURE [App::DocumentObjectGroupPython] G4_Pr  # scripted group (container) (typed FeaturePython)
  Dunit = g/cm3
  Dvalue = 6.71
  Group = -> [Pr_element001]
  conduct = 2
  density = 1
  expand = 3
  formula = Pr
  name = G4_Pr
  specific = 4
FEATURE [App::DocumentObjectGroupPython] Nd_element001  label="Nd_element : 1"  # scripted group (container) (typed FeaturePython)
  n = 1
  ref = Nd_element
FEATURE [App::DocumentObjectGroupPython] G4_Nd  # scripted group (container) (typed FeaturePython)
  Dunit = g/cm3
  Dvalue = 6.9
  Group = -> [Nd_element001]
  conduct = 2
  density = 1
  expand = 3
  formula = Nd
  name = G4_Nd
  specific = 4
FEATURE [App::DocumentObjectGroupPython] Pm_element001  label="Pm_element : 1"  # scripted group (container) (typed FeaturePython)
  n = 1
  ref = Pm_element
FEATURE [App::DocumentObjectGroupPython] G4_Pm  # scripted group (container) (typed FeaturePython)
  Dunit = g/cm3
  Dvalue = 7.22
  Group = -> [Pm_element001]
  conduct = 2
  density = 1
  expand = 3
  formula = Pm
  name = G4_Pm
  specific = 4
FEATURE [App::DocumentObjectGroupPython] Sm_element001  label="Sm_element : 1"  # scripted group (container) (typed FeaturePython)
  n = 1
  ref = Sm_element
FEATURE [App::DocumentObjectGroupPython] G4_Sm  # scripted group (container) (typed FeaturePython)
  Dunit = g/cm3
  Dvalue = 7.46
  Group = -> [Sm_element001]
  conduct = 2
  density = 1
  expand = 3
  formula = Sm
  name = G4_Sm
  specific = 4
FEATURE [App::DocumentObjectGroupPython] Eu_element001  label="Eu_element : 1"  # scripted group (container) (typed FeaturePython)
  n = 1
  ref = Eu_element
FEATURE [App::DocumentObjectGroupPython] G4_Eu  # scripted group (container) (typed FeaturePython)
  Dunit = g/cm3
  Dvalue = 5.243
  Group = -> [Eu_element001]
  conduct = 2
  density = 1
  expand = 3
  formula = Eu
  name = G4_Eu
  specific = 4
FEATURE [App::DocumentObjectGroupPython] Gd_element002  label="Gd_element : 1"  # scripted group (container) (typed FeaturePython)
  n = 1
  ref = Gd_element
FEATURE [App::DocumentObjectGroupPython] G4_Gd  # scripted group (container) (typed FeaturePython)
  Dunit = g/cm3
  Dvalue = 7.9004
  Group = -> [Gd_element002]
  conduct = 2
  density = 1
  expand = 3
  formula = Gd
  name = G4_Gd
  specific = 4
FEATURE [App::DocumentObjectGroupPython] Tb_element001  label="Tb_element : 1"  # scripted group (container) (typed FeaturePython)
  n = 1
  ref = Tb_element
FEATURE [App::DocumentObjectGroupPython] G4_Tb  # scripted group (container) (typed FeaturePython)
  Dunit = g/cm3
  Dvalue = 8.229
  Group = -> [Tb_element001]
  conduct = 2
  density = 1
  expand = 3
  formula = Tb
  name = G4_Tb
  specific = 4
FEATURE [App::DocumentObjectGroupPython] Dy_element001  label="Dy_element : 1"  # scripted group (container) (typed FeaturePython)
  n = 1
  ref = Dy_element
FEATURE [App::DocumentObjectGroupPython] G4_Dy  # scripted group (container) (typed FeaturePython)
  Dunit = g/cm3
  Dvalue = 8.55
  Group = -> [Dy_element001]
  conduct = 2
  density = 1
  expand = 3
  formula = Dy
  name = G4_Dy
  specific = 4
FEATURE [App::DocumentObjectGroupPython] Ho_element001  label="Ho_element : 1"  # scripted group (container) (typed FeaturePython)
  n = 1
  ref = Ho_element
FEATURE [App::DocumentObjectGroupPython] G4_Ho  # scripted group (container) (typed FeaturePython)
  Dunit = g/cm3
  Dvalue = 8.795
  Group = -> [Ho_element001]
  conduct = 2
  density = 1
  expand = 3
  formula = Ho
  name = G4_Ho
  specific = 4
FEATURE [App::DocumentObjectGroupPython] Er_element001  label="Er_element : 1"  # scripted group (container) (typed FeaturePython)
  n = 1
  ref = Er_element
FEATURE [App::DocumentObjectGroupPython] G4_Er  # scripted group (container) (typed FeaturePython)
  Dunit = g/cm3
  Dvalue = 9.066
  Group = -> [Er_element001]
  conduct = 2
  density = 1
  expand = 3
  formula = Er
  name = G4_Er
  specific = 4
FEATURE [App::DocumentObjectGroupPython] Tm_element001  label="Tm_element : 1"  # scripted group (container) (typed FeaturePython)
  n = 1
  ref = Tm_element
FEATURE [App::DocumentObjectGroupPython] G4_Tm  # scripted group (container) (typed FeaturePython)
  Dunit = g/cm3
  Dvalue = 9.321
  Group = -> [Tm_element001]
  conduct = 2
  density = 1
  expand = 3
  formula = Tm
  name = G4_Tm
  specific = 4
FEATURE [App::DocumentObjectGroupPython] Yb_element001  label="Yb_element : 1"  # scripted group (container) (typed FeaturePython)
  n = 1
  ref = Yb_element
FEATURE [App::DocumentObjectGroupPython] G4_Yb  # scripted group (container) (typed FeaturePython)
  Dunit = g/cm3
  Dvalue = 6.73
  Group = -> [Yb_element001]
  conduct = 2
  density = 1
  expand = 3
  formula = Yb
  name = G4_Yb
  specific = 4
FEATURE [App::DocumentObjectGroupPython] Lu_element001  label="Lu_element : 1"  # scripted group (container) (typed FeaturePython)
  n = 1
  ref = Lu_element
FEATURE [App::DocumentObjectGroupPython] G4_Lu  # scripted group (container) (typed FeaturePython)
  Dunit = g/cm3
  Dvalue = 9.84
  Group = -> [Lu_element001]
  conduct = 2
  density = 1
  expand = 3
  formula = Lu
  name = G4_Lu
  specific = 4
FEATURE [App::DocumentObjectGroupPython] Hf_element001  label="Hf_element : 1"  # scripted group (container) (typed FeaturePython)
  n = 1
  ref = Hf_element
FEATURE [App::DocumentObjectGroupPython] G4_Hf  # scripted group (container) (typed FeaturePython)
  Dunit = g/cm3
  Dvalue = 13.31
  Group = -> [Hf_element001]
  conduct = 2
  density = 1
  expand = 3
  formula = Hf
  name = G4_Hf
  specific = 4
FEATURE [App::DocumentObjectGroupPython] Ta_element001  label="Ta_element : 1"  # scripted group (container) (typed FeaturePython)
  n = 1
  ref = Ta_element
FEATURE [App::DocumentObjectGroupPython] G4_Ta  # scripted group (container) (typed FeaturePython)
  Dunit = g/cm3
  Dvalue = 16.654
  Group = -> [Ta_element001]
  conduct = 2
  density = 1
  expand = 3
  formula = Ta
  name = G4_Ta
  specific = 4
FEATURE [App::DocumentObjectGroupPython] W_element004  label="W_element : 004"  # scripted group (container) (typed FeaturePython)
  n = 1
  ref = W_element
FEATURE [App::DocumentObjectGroupPython] G4_W  # scripted group (container) (typed FeaturePython)
  Dunit = g/cm3
  Dvalue = 19.3
  Group = -> [W_element004]
  conduct = 2
  density = 1
  expand = 3
  formula = W
  name = G4_W
  specific = 4
FEATURE [App::DocumentObjectGroupPython] Re_element001  label="Re_element : 1"  # scripted group (container) (typed FeaturePython)
  n = 1
  ref = Re_element
FEATURE [App::DocumentObjectGroupPython] G4_Re  # scripted group (container) (typed FeaturePython)
  Dunit = g/cm3
  Dvalue = 21.02
  Group = -> [Re_element001]
  conduct = 2
  density = 1
  expand = 3
  formula = Re
  name = G4_Re
  specific = 4
FEATURE [App::DocumentObjectGroupPython] Os_element001  label="Os_element : 1"  # scripted group (container) (typed FeaturePython)
  n = 1
  ref = Os_element
FEATURE [App::DocumentObjectGroupPython] G4_Os  # scripted group (container) (typed FeaturePython)
  Dunit = g/cm3
  Dvalue = 22.57
  Group = -> [Os_element001]
  conduct = 2
  density = 1
  expand = 3
  formula = Os
  name = G4_Os
  specific = 4
FEATURE [App::DocumentObjectGroupPython] Ir_element001  label="Ir_element : 1"  # scripted group (container) (typed FeaturePython)
  n = 1
  ref = Ir_element
FEATURE [App::DocumentObjectGroupPython] G4_Ir  # scripted group (container) (typed FeaturePython)
  Dunit = g/cm3
  Dvalue = 22.42
  Group = -> [Ir_element001]
  conduct = 2
  density = 1
  expand = 3
  formula = Ir
  name = G4_Ir
  specific = 4
FEATURE [App::DocumentObjectGroupPython] Pt_element001  label="Pt_element : 1"  # scripted group (container) (typed FeaturePython)
  n = 1
  ref = Pt_element
FEATURE [App::DocumentObjectGroupPython] G4_Pt  # scripted group (container) (typed FeaturePython)
  Dunit = g/cm3
  Dvalue = 21.45
  Group = -> [Pt_element001]
  conduct = 2
  density = 1
  expand = 3
  formula = Pt
  name = G4_Pt
  specific = 4
FEATURE [App::DocumentObjectGroupPython] Au_element001  label="Au_element : 1"  # scripted group (container) (typed FeaturePython)
  n = 1
  ref = Au_element
FEATURE [App::DocumentObjectGroupPython] G4_Au  # scripted group (container) (typed FeaturePython)
  Dunit = g/cm3
  Dvalue = 19.32
  Group = -> [Au_element001]
  conduct = 2
  density = 1
  expand = 3
  formula = Au
  name = G4_Au
  specific = 4
FEATURE [App::DocumentObjectGroupPython] Hg_element002  label="Hg_element : 002"  # scripted group (container) (typed FeaturePython)
  n = 1
  ref = Hg_element
FEATURE [App::DocumentObjectGroupPython] G4_Hg  # scripted group (container) (typed FeaturePython)
  Dunit = g/cm3
  Dvalue = 13.546
  Group = -> [Hg_element002]
  conduct = 2
  density = 1
  expand = 3
  formula = Hg
  name = G4_Hg
  specific = 4
FEATURE [App::DocumentObjectGroupPython] Tl_element002  label="Tl_element : 002"  # scripted group (container) (typed FeaturePython)
  n = 1
  ref = Tl_element
FEATURE [App::DocumentObjectGroupPython] G4_Tl  # scripted group (container) (typed FeaturePython)
  Dunit = g/cm3
  Dvalue = 11.72
  Group = -> [Tl_element002]
  conduct = 2
  density = 1
  expand = 3
  formula = Tl
  name = G4_Tl
  specific = 4
FEATURE [App::DocumentObjectGroupPython] Pb_element003  label="Pb_element : 1"  # scripted group (container) (typed FeaturePython)
  n = 1
  ref = Pb_element
FEATURE [App::DocumentObjectGroupPython] G4_Pb  # scripted group (container) (typed FeaturePython)
  Dunit = g/cm3
  Dvalue = 11.35
  Group = -> [Pb_element003]
  conduct = 2
  density = 1
  expand = 3
  formula = Pb
  name = G4_Pb
  specific = 4
FEATURE [App::DocumentObjectGroupPython] Bi_element002  label="Bi_element : 1"  # scripted group (container) (typed FeaturePython)
  n = 1
  ref = Bi_element
FEATURE [App::DocumentObjectGroupPython] G4_Bi  # scripted group (container) (typed FeaturePython)
  Dunit = g/cm3
  Dvalue = 9.747
  Group = -> [Bi_element002]
  conduct = 2
  density = 1
  expand = 3
  formula = Bi
  name = G4_Bi
  specific = 4
FEATURE [App::DocumentObjectGroupPython] Po_element001  label="Po_element : 1"  # scripted group (container) (typed FeaturePython)
  n = 1
  ref = Po_element
FEATURE [App::DocumentObjectGroupPython] G4_Po  # scripted group (container) (typed FeaturePython)
  Dunit = g/cm3
  Dvalue = 9.32
  Group = -> [Po_element001]
  conduct = 2
  density = 1
  expand = 3
  formula = Po
  name = G4_Po
  specific = 4
FEATURE [App::DocumentObjectGroupPython] At_element001  label="At_element : 1"  # scripted group (container) (typed FeaturePython)
  n = 1
  ref = At_element
FEATURE [App::DocumentObjectGroupPython] G4_At  # scripted group (container) (typed FeaturePython)
  Dunit = g/cm3
  Dvalue = 9.32
  Group = -> [At_element001]
  conduct = 2
  density = 1
  expand = 3
  formula = At
  name = G4_At
  specific = 4
FEATURE [App::DocumentObjectGroupPython] Rn_element001  label="Rn_element : 1"  # scripted group (container) (typed FeaturePython)
  n = 1
  ref = Rn_element
FEATURE [App::DocumentObjectGroupPython] G4_Rn  # scripted group (container) (typed FeaturePython)
  Dunit = g/cm3
  Dvalue = 0.00900662
  Group = -> [Rn_element001]
  conduct = 2
  density = 1
  expand = 3
  formula = Rn
  name = G4_Rn
  specific = 4
FEATURE [App::DocumentObjectGroupPython] Fr_element001  label="Fr_element : 1"  # scripted group (container) (typed FeaturePython)
  n = 1
  ref = Fr_element
FEATURE [App::DocumentObjectGroupPython] G4_Fr  # scripted group (container) (typed FeaturePython)
  Dunit = g/cm3
  Dvalue = 1
  Group = -> [Fr_element001]
  conduct = 2
  density = 1
  expand = 3
  formula = Fr
  name = G4_Fr
  specific = 4
FEATURE [App::DocumentObjectGroupPython] Ra_element001  label="Ra_element : 1"  # scripted group (container) (typed FeaturePython)
  n = 1
  ref = Ra_element
FEATURE [App::DocumentObjectGroupPython] G4_Ra  # scripted group (container) (typed FeaturePython)
  Dunit = g/cm3
  Dvalue = 5
  Group = -> [Ra_element001]
  conduct = 2
  density = 1
  expand = 3
  formula = Ra
  name = G4_Ra
  specific = 4
FEATURE [App::DocumentObjectGroupPython] Ac_element001  label="Ac_element : 1"  # scripted group (container) (typed FeaturePython)
  n = 1
  ref = Ac_element
FEATURE [App::DocumentObjectGroupPython] G4_Ac  # scripted group (container) (typed FeaturePython)
  Dunit = g/cm3
  Dvalue = 10.07
  Group = -> [Ac_element001]
  conduct = 2
  density = 1
  expand = 3
  formula = Ac
  name = G4_Ac
  specific = 4
FEATURE [App::DocumentObjectGroupPython] Th_element001  label="Th_element : 1"  # scripted group (container) (typed FeaturePython)
  n = 1
  ref = Th_element
FEATURE [App::DocumentObjectGroupPython] G4_Th  # scripted group (container) (typed FeaturePython)
  Dunit = g/cm3
  Dvalue = 11.72
  Group = -> [Th_element001]
  conduct = 2
  density = 1
  expand = 3
  formula = Th
  name = G4_Th
  specific = 4
FEATURE [App::DocumentObjectGroupPython] Pa_element001  label="Pa_element : 1"  # scripted group (container) (typed FeaturePython)
  n = 1
  ref = Pa_element
FEATURE [App::DocumentObjectGroupPython] G4_Pa  # scripted group (container) (typed FeaturePython)
  Dunit = g/cm3
  Dvalue = 15.37
  Group = -> [Pa_element001]
  conduct = 2
  density = 1
  expand = 3
  formula = Pa
  name = G4_Pa
  specific = 4
FEATURE [App::DocumentObjectGroupPython] U_element004  label="U_element : 004"  # scripted group (container) (typed FeaturePython)
  n = 1
  ref = U_element
FEATURE [App::DocumentObjectGroupPython] G4_U  # scripted group (container) (typed FeaturePython)
  Dunit = g/cm3
  Dvalue = 18.95
  Group = -> [U_element004]
  conduct = 2
  density = 1
  expand = 3
  formula = U
  name = G4_U
  specific = 4
FEATURE [App::DocumentObjectGroupPython] Np_element001  label="Np_element : 1"  # scripted group (container) (typed FeaturePython)
  n = 1
  ref = Np_element
FEATURE [App::DocumentObjectGroupPython] G4_Np  # scripted group (container) (typed FeaturePython)
  Dunit = g/cm3
  Dvalue = 20.25
  Group = -> [Np_element001]
  conduct = 2
  density = 1
  expand = 3
  formula = Np
  name = G4_Np
  specific = 4
FEATURE [App::DocumentObjectGroupPython] Pu_element002  label="Pu_element : 002"  # scripted group (container) (typed FeaturePython)
  n = 1
  ref = Pu_element
FEATURE [App::DocumentObjectGroupPython] G4_Pu  # scripted group (container) (typed FeaturePython)
  Dunit = g/cm3
  Dvalue = 19.84
  Group = -> [Pu_element002]
  conduct = 2
  density = 1
  expand = 3
  formula = Pu
  name = G4_Pu
  specific = 4
FEATURE [App::DocumentObjectGroupPython] Am_element001  label="Am_element : 1"  # scripted group (container) (typed FeaturePython)
  n = 1
  ref = Am_element
FEATURE [App::DocumentObjectGroupPython] G4_Am  # scripted group (container) (typed FeaturePython)
  Dunit = g/cm3
  Dvalue = 13.67
  Group = -> [Am_element001]
  conduct = 2
  density = 1
  expand = 3
  formula = Am
  name = G4_Am
  specific = 4
FEATURE [App::DocumentObjectGroupPython] Cm_element001  label="Cm_element : 1"  # scripted group (container) (typed FeaturePython)
  n = 1
  ref = Cm_element
FEATURE [App::DocumentObjectGroupPython] G4_Cm  # scripted group (container) (typed FeaturePython)
  Dunit = g/cm3
  Dvalue = 13.51
  Group = -> [Cm_element001]
  conduct = 2
  density = 1
  expand = 3
  formula = Cm
  name = G4_Cm
  specific = 4
FEATURE [App::DocumentObjectGroupPython] Bk_element001  label="Bk_element : 1"  # scripted group (container) (typed FeaturePython)
  n = 1
  ref = Bk_element
FEATURE [App::DocumentObjectGroupPython] G4_Bk  # scripted group (container) (typed FeaturePython)
  Dunit = g/cm3
  Dvalue = 14
  Group = -> [Bk_element001]
  conduct = 2
  density = 1
  expand = 3
  formula = Bk
  name = G4_Bk
  specific = 4
FEATURE [App::DocumentObjectGroupPython] Cf_element001  label="Cf_element : 1"  # scripted group (container) (typed FeaturePython)
  n = 1
  ref = Cf_element
FEATURE [App::DocumentObjectGroupPython] G4_Cf  # scripted group (container) (typed FeaturePython)
  Dunit = g/cm3
  Dvalue = 10
  Group = -> [Cf_element001]
  conduct = 2
  density = 1
  expand = 3
  formula = Cf
  name = G4_Cf
  specific = 4
FEATURE [App::DocumentObjectGroupPython] Element  # scripted group (container) (typed FeaturePython)
  Group = -> [G4_H,G4_He,G4_Li,G4_Be,G4_B,G4_C,G4_N,G4_O,G4_F,G4_Ne,G4_Na,G4_Mg,G4_Al,G4_Si,G4_P,G4_S,G4_Cl,G4_Ar,G4_K,G4_Ca,G4_Sc,G4_Ti,G4_V,G4_Cr,G4_Mn,G4_Fe,G4_Co,G4_Ni,G4_Cu,G4_Zn,G4_Ga,G4_Ge,G4_As,G4_Se,G4_Br,G4_Kr,G4_Rb,G4_Sr,G4_Y,G4_Zr,G4_Nb,G4_Mo,G4_Tc,G4_Ru,G4_Rh,G4_Pd,G4_Ag,G4_Cd,G4_In,G4_Sn,G4_Sb,G4_Te,G4_I,G4_Xe,G4_Cs,G4_Ba,G4_La,G4_Ce,G4_Pr,G4_Nd,G4_Pm,G4_Sm,G4_Eu,G4_Gd,G4_Tb,G4_Dy,G4_Ho,G4_Er,+30 more]
FEATURE [App::DocumentObjectGroupPython] H_element114  label="H_element : 063"  # scripted group (container) (typed FeaturePython)
  n = 2
  ref = H_element
FEATURE [App::DocumentObjectGroupPython] G4_lH2  # scripted group (container) (typed FeaturePython)
  Dunit = g/cm3
  Dvalue = 0.0708
  Group = -> [H_element114]
  conduct = 2
  density = 1
  expand = 3
  formula = G4_lH2
  name = G4_lH2
  specific = 4
FEATURE [App::DocumentObjectGroupPython] N_element049  label="N_element : 022"  # scripted group (container) (typed FeaturePython)
  n = 2
  ref = N_element
FEATURE [App::DocumentObjectGroupPython] G4_lN2  # scripted group (container) (typed FeaturePython)
  Dunit = g/cm3
  Dvalue = 0.807
  Group = -> [N_element049]
  conduct = 2
  density = 1
  expand = 3
  formula = G4_lN2
  name = G4_lN2
  specific = 4
FEATURE [App::DocumentObjectGroupPython] O_element106  label="O_element : 060"  # scripted group (container) (typed FeaturePython)
  n = 2
  ref = O_element
FEATURE [App::DocumentObjectGroupPython] G4_lO2  # scripted group (container) (typed FeaturePython)
  Dunit = g/cm3
  Dvalue = 1.141
  Group = -> [O_element106]
  conduct = 2
  density = 1
  expand = 3
  formula = G4_lO2
  name = G4_lO2
  specific = 4
FEATURE [App::DocumentObjectGroupPython] Ar  label="Ar : 1"  # scripted group (container) (typed FeaturePython)
  n = 1
  ref = Ar
FEATURE [App::DocumentObjectGroupPython] G4_lAr  # scripted group (container) (typed FeaturePython)
  Dunit = g/cm3
  Dvalue = 1.396
  Group = -> [Ar]
  conduct = 2
  density = 1
  expand = 3
  formula = G4_lAr
  name = G4_lAr
  specific = 4
FEATURE [App::DocumentObjectGroupPython] Br  label="Br : 1"  # scripted group (container) (typed FeaturePython)
  n = 1
  ref = Br
FEATURE [App::DocumentObjectGroupPython] G4_lBr  # scripted group (container) (typed FeaturePython)
  Dunit = g/cm3
  Dvalue = 3.1028
  Group = -> [Br]
  conduct = 2
  density = 1
  expand = 3
  formula = G4_lBr
  name = G4_lBr
  specific = 4
FEATURE [App::DocumentObjectGroupPython] Kr  label="Kr : 1"  # scripted group (container) (typed FeaturePython)
  n = 1
  ref = Kr
FEATURE [App::DocumentObjectGroupPython] G4_lKr  # scripted group (container) (typed FeaturePython)
  Dunit = g/cm3
  Dvalue = 2.418
  Group = -> [Kr]
  conduct = 2
  density = 1
  expand = 3
  formula = G4_lKr
  name = G4_lKr
  specific = 4
FEATURE [App::DocumentObjectGroupPython] Xe  label="Xe : 1"  # scripted group (container) (typed FeaturePython)
  n = 1
  ref = Xe
FEATURE [App::DocumentObjectGroupPython] G4_lXe  # scripted group (container) (typed FeaturePython)
  Dunit = g/cm3
  Dvalue = 2.953
  Group = -> [Xe]
  conduct = 2
  density = 1
  expand = 3
  formula = G4_lXe
  name = G4_lXe
  specific = 4
FEATURE [App::DocumentObjectGroupPython] O_element107  label="O_element : 061"  # scripted group (container) (typed FeaturePython)
  n = 4
  ref = O_element
FEATURE [App::DocumentObjectGroupPython] Pb_element004  label="Pb_element : 002"  # scripted group (container) (typed FeaturePython)
  n = 1
  ref = Pb_element
FEATURE [App::DocumentObjectGroupPython] W_element005  label="W_element : 005"  # scripted group (container) (typed FeaturePython)
  n = 1
  ref = W_element
FEATURE [App::DocumentObjectGroupPython] G4_PbWO4  # scripted group (container) (typed FeaturePython)
  Dunit = g/cm3
  Dvalue = 8.28
  Group = -> [O_element107,Pb_element004,W_element005]
  conduct = 2
  density = 1
  expand = 3
  formula = G4_PbWO4
  name = G4_PbWO4
  specific = 4
FEATURE [App::DocumentObjectGroupPython] alactic  label="alactic : 1"  # scripted group (container) (typed FeaturePython)
  n = 1
  ref = alactic
FEATURE [App::DocumentObjectGroupPython] G4_Galactic  # scripted group (container) (typed FeaturePython)
  Dunit = g/cm3
  Dvalue = 0
  Group = -> [alactic]
  conduct = 2
  density = 1
  expand = 3
  formula = G4_Galactic
  name = G4_Galactic
  specific = 4
FEATURE [App::DocumentObjectGroupPython] RAPHITE_POROUS  label="RAPHITE_POROUS : 1"  # scripted group (container) (typed FeaturePython)
  n = 1
  ref = RAPHITE_POROUS
FEATURE [App::DocumentObjectGroupPython] G4_GRAPHITE_POROUS  # scripted group (container) (typed FeaturePython)
  Dunit = g/cm3
  Dvalue = 1.7
  Group = -> [RAPHITE_POROUS]
  conduct = 2
  density = 1
  expand = 3
  formula = G4_GRAPHITE_POROUS
  name = G4_GRAPHITE_POROUS
  specific = 4
FEATURE [App::DocumentObjectGroupPython] H_element115  label="H_element : 0.150"  # scripted group (container) (typed FeaturePython)
  n = 0.080538
FEATURE [App::DocumentObjectGroupPython] C_element125  label="C_element : 0.600"  # scripted group (container) (typed FeaturePython)
  n = 0.599848
FEATURE [App::DocumentObjectGroupPython] O_element108  label="O_element : 0.320"  # scripted group (container) (typed FeaturePython)
  n = 0.319614
FEATURE [App::DocumentObjectGroupPython] G4_LUCITE  # scripted group (container) (typed FeaturePython)
  Dunit = g/cm3
  Dvalue = 1.19
  Group = -> [H_element115,C_element125,O_element108]
  conduct = 2
  density = 1
  expand = 3
  formula = G4_LUCITE
  name = G4_LUCITE
  specific = 4
FEATURE [App::DocumentObjectGroupPython] Cu_element002  label="Cu_element : 62"  # scripted group (container) (typed FeaturePython)
  n = 62
  ref = Cu_element
FEATURE [App::DocumentObjectGroupPython] Zn_element002  label="Zn_element : 35"  # scripted group (container) (typed FeaturePython)
  n = 35
  ref = Zn_element
FEATURE [App::DocumentObjectGroupPython] Pb_element005  label="Pb_element : 3"  # scripted group (container) (typed FeaturePython)
  n = 3
  ref = Pb_element
FEATURE [App::DocumentObjectGroupPython] G4_BRASS  # scripted group (container) (typed FeaturePython)
  Dunit = g/cm3
  Dvalue = 8.52
  Group = -> [Cu_element002,Zn_element002,Pb_element005]
  conduct = 2
  density = 1
  expand = 3
  formula = G4_BRASS
  name = G4_BRASS
  specific = 4
FEATURE [App::DocumentObjectGroupPython] Cu_element003  label="Cu_element : 89"  # scripted group (container) (typed FeaturePython)
  n = 89
  ref = Cu_element
FEATURE [App::DocumentObjectGroupPython] Zn_element003  label="Zn_element : 9"  # scripted group (container) (typed FeaturePython)
  n = 9
  ref = Zn_element
FEATURE [App::DocumentObjectGroupPython] Pb_element006  label="Pb_element : 2"  # scripted group (container) (typed FeaturePython)
  n = 2
  ref = Pb_element
FEATURE [App::DocumentObjectGroupPython] G4_BRONZE  # scripted group (container) (typed FeaturePython)
  Dunit = g/cm3
  Dvalue = 8.82
  Group = -> [Cu_element003,Zn_element003,Pb_element006]
  conduct = 2
  density = 1
  expand = 3
  formula = G4_BRONZE
  name = G4_BRONZE
  specific = 4
FEATURE [App::DocumentObjectGroupPython] Fe_element008  label="Fe_element : 74"  # scripted group (container) (typed FeaturePython)
  n = 74
  ref = Fe_element
FEATURE [App::DocumentObjectGroupPython] Cr_element002  label="Cr_element : 18"  # scripted group (container) (typed FeaturePython)
  n = 18
  ref = Cr_element
FEATURE [App::DocumentObjectGroupPython] Ni_element002  label="Ni_element : 8"  # scripted group (container) (typed FeaturePython)
  n = 8
  ref = Ni_element
FEATURE [App::DocumentObjectGroupPython] G4_STAINLESS_STEEL  label="G4_STAINLESS-STEEL"  # scripted group (container) (typed FeaturePython)
  Dunit = g/cm3
  Dvalue = 8
  Group = -> [Fe_element008,Cr_element002,Ni_element002]
  conduct = 2
  density = 1
  expand = 3
  formula = G4_STAINLESS-STEEL
  name = G4_STAINLESS-STEEL
  specific = 4
FEATURE [App::DocumentObjectGroupPython] H_element116  label="H_element : 064"  # scripted group (container) (typed FeaturePython)
  n = 18
  ref = H_element
FEATURE [App::DocumentObjectGroupPython] C_element126  label="C_element : 071"  # scripted group (container) (typed FeaturePython)
  n = 12
  ref = C_element
FEATURE [App::DocumentObjectGroupPython] O_element109  label="O_element : 062"  # scripted group (container) (typed FeaturePython)
  n = 7
  ref = O_element
FEATURE [App::DocumentObjectGroupPython] G4_CR39  # scripted group (container) (typed FeaturePython)
  Dunit = g/cm3
  Dvalue = 1.32
  Group = -> [H_element116,C_element126,O_element109]
  conduct = 2
  density = 1
  expand = 3
  formula = G4_CR39
  name = G4_CR39
  specific = 4
FEATURE [App::DocumentObjectGroupPython] H_element117  label="H_element : 38"  # scripted group (container) (typed FeaturePython)
  n = 38
  ref = H_element
FEATURE [App::DocumentObjectGroupPython] C_element127  label="C_element : 072"  # scripted group (container) (typed FeaturePython)
  n = 18
  ref = C_element
FEATURE [App::DocumentObjectGroupPython] O_element110  label="O_element : 063"  # scripted group (container) (typed FeaturePython)
  n = 1
  ref = O_element
FEATURE [App::DocumentObjectGroupPython] G4_OCTADECANOL  # scripted group (container) (typed FeaturePython)
  Dunit = g/cm3
  Dvalue = 0.812
  Group = -> [H_element117,C_element127,O_element110]
  conduct = 2
  density = 1
  expand = 3
  formula = G4_OCTADECANOL
  name = G4_OCTADECANOL
  specific = 4
FEATURE [App::DocumentObjectGroupPython] HEP  # scripted group (container) (typed FeaturePython)
  Group = -> [G4_lH2,G4_lN2,G4_lO2,G4_lAr,G4_lBr,G4_lKr,G4_lXe,G4_PbWO4,G4_Galactic,G4_GRAPHITE_POROUS,G4_LUCITE,G4_BRASS,G4_BRONZE,G4_STAINLESS_STEEL,G4_CR39,G4_OCTADECANOL]
FEATURE [App::DocumentObjectGroupPython] C_element128  label="C_element : 073"  # scripted group (container) (typed FeaturePython)
  n = 14
  ref = C_element
FEATURE [App::DocumentObjectGroupPython] H_element118  label="H_element : 065"  # scripted group (container) (typed FeaturePython)
  n = 10
  ref = H_element
FEATURE [App::DocumentObjectGroupPython] O_element111  label="O_element : 064"  # scripted group (container) (typed FeaturePython)
  n = 2
  ref = O_element
FEATURE [App::DocumentObjectGroupPython] N_element050  label="N_element : 023"  # scripted group (container) (typed FeaturePython)
  n = 2
  ref = N_element
FEATURE [App::DocumentObjectGroupPython] G4_KEVLAR  # scripted group (container) (typed FeaturePython)
  Dunit = g/cm3
  Dvalue = 1.44
  Group = -> [C_element128,H_element118,O_element111,N_element050]
  conduct = 2
  density = 1
  expand = 3
  formula = G4_KEVLAR
  name = G4_KEVLAR
  specific = 4
FEATURE [App::DocumentObjectGroupPython] C_element129  label="C_element : 074"  # scripted group (container) (typed FeaturePython)
  n = 10
  ref = C_element
FEATURE [App::DocumentObjectGroupPython] H_element119  label="H_element : 066"  # scripted group (container) (typed FeaturePython)
  n = 8
  ref = H_element
FEATURE [App::DocumentObjectGroupPython] O_element112  label="O_element : 065"  # scripted group (container) (typed FeaturePython)
  n = 4
  ref = O_element
FEATURE [App::DocumentObjectGroupPython] G4_DACRON  # scripted group (container) (typed FeaturePython)
  Dunit = g/cm3
  Dvalue = 1.4
  Group = -> [C_element129,H_element119,O_element112]
  conduct = 2
  density = 1
  expand = 3
  formula = G4_DACRON
  name = G4_DACRON
  specific = 4
FEATURE [App::DocumentObjectGroupPython] C_element130  label="C_element : 075"  # scripted group (container) (typed FeaturePython)
  n = 4
  ref = C_element
FEATURE [App::DocumentObjectGroupPython] H_element120  label="H_element : 067"  # scripted group (container) (typed FeaturePython)
  n = 5
  ref = H_element
FEATURE [App::DocumentObjectGroupPython] Cl_element030  label="Cl_element : 016"  # scripted group (container) (typed FeaturePython)
  n = 1
  ref = Cl_element
FEATURE [App::DocumentObjectGroupPython] G4_NEOPRENE  # scripted group (container) (typed FeaturePython)
  Dunit = g/cm3
  Dvalue = 1.23
  Group = -> [C_element130,H_element120,Cl_element030]
  conduct = 2
  density = 1
  expand = 3
  formula = G4_NEOPRENE
  name = G4_NEOPRENE
  specific = 4
FEATURE [App::DocumentObjectGroupPython] Space  # scripted group (container) (typed FeaturePython)
  Group = -> [G4_KEVLAR,G4_DACRON,G4_NEOPRENE]
FEATURE [App::DocumentObjectGroupPython] H_element121  label="H_element : 068"  # scripted group (container) (typed FeaturePython)
  n = 5
  ref = H_element
FEATURE [App::DocumentObjectGroupPython] C_element131  label="C_element : 076"  # scripted group (container) (typed FeaturePython)
  n = 4
  ref = C_element
FEATURE [App::DocumentObjectGroupPython] N_element051  label="N_element : 3"  # scripted group (container) (typed FeaturePython)
  n = 3
  ref = N_element
FEATURE [App::DocumentObjectGroupPython] O_element113  label="O_element : 066"  # scripted group (container) (typed FeaturePython)
  n = 1
  ref = O_element
FEATURE [App::DocumentObjectGroupPython] G4_CYTOSINE  # scripted group (container) (typed FeaturePython)
  Dunit = g/cm3
  Dvalue = 1.55
  Group = -> [H_element121,C_element131,N_element051,O_element113]
  conduct = 2
  density = 1
  expand = 3
  formula = G4_CYTOSINE
  name = G4_CYTOSINE
  specific = 4
FEATURE [App::DocumentObjectGroupPython] H_element122  label="H_element : 069"  # scripted group (container) (typed FeaturePython)
  n = 6
  ref = H_element
FEATURE [App::DocumentObjectGroupPython] C_element132  label="C_element : 077"  # scripted group (container) (typed FeaturePython)
  n = 5
  ref = C_element
FEATURE [App::DocumentObjectGroupPython] N_element052  label="N_element : 024"  # scripted group (container) (typed FeaturePython)
  n = 2
  ref = N_element
FEATURE [App::DocumentObjectGroupPython] O_element114  label="O_element : 067"  # scripted group (container) (typed FeaturePython)
  n = 2
  ref = O_element
FEATURE [App::DocumentObjectGroupPython] G4_THYMINE  # scripted group (container) (typed FeaturePython)
  Dunit = g/cm3
  Dvalue = 1.23
  Group = -> [H_element122,C_element132,N_element052,O_element114]
  conduct = 2
  density = 1
  expand = 3
  formula = G4_THYMINE
  name = G4_THYMINE
  specific = 4
FEATURE [App::DocumentObjectGroupPython] H_element123  label="H_element : 070"  # scripted group (container) (typed FeaturePython)
  n = 4
  ref = H_element
FEATURE [App::DocumentObjectGroupPython] C_element133  label="C_element : 078"  # scripted group (container) (typed FeaturePython)
  n = 4
  ref = C_element
FEATURE [App::DocumentObjectGroupPython] N_element053  label="N_element : 025"  # scripted group (container) (typed FeaturePython)
  n = 2
  ref = N_element
FEATURE [App::DocumentObjectGroupPython] O_element115  label="O_element : 068"  # scripted group (container) (typed FeaturePython)
  n = 2
  ref = O_element
FEATURE [App::DocumentObjectGroupPython] G4_URACIL  # scripted group (container) (typed FeaturePython)
  Dunit = g/cm3
  Dvalue = 1.32
  Group = -> [H_element123,C_element133,N_element053,O_element115]
  conduct = 2
  density = 1
  expand = 3
  formula = G4_URACIL
  name = G4_URACIL
  specific = 4
FEATURE [App::DocumentObjectGroupPython] H_element124  label="H_element : 071"  # scripted group (container) (typed FeaturePython)
  n = 4
  ref = H_element
FEATURE [App::DocumentObjectGroupPython] C_element134  label="C_element : 079"  # scripted group (container) (typed FeaturePython)
  n = 5
  ref = C_element
FEATURE [App::DocumentObjectGroupPython] N_element054  label="N_element : 026"  # scripted group (container) (typed FeaturePython)
  n = 5
  ref = N_element
FEATURE [App::DocumentObjectGroupPython] G4_DNA_ADENINE  # scripted group (container) (typed FeaturePython)
  Dunit = g/cm3
  Dvalue = 1
  Group = -> [H_element124,C_element134,N_element054]
  conduct = 2
  density = 1
  expand = 3
  formula = G4_DNA_ADENINE
  name = G4_DNA_ADENINE
  specific = 4
FEATURE [App::DocumentObjectGroupPython] H_element125  label="H_element : 072"  # scripted group (container) (typed FeaturePython)
  n = 4
  ref = H_element
FEATURE [App::DocumentObjectGroupPython] C_element135  label="C_element : 080"  # scripted group (container) (typed FeaturePython)
  n = 5
  ref = C_element
FEATURE [App::DocumentObjectGroupPython] N_element055  label="N_element : 027"  # scripted group (container) (typed FeaturePython)
  n = 5
  ref = N_element
FEATURE [App::DocumentObjectGroupPython] O_element116  label="O_element : 069"  # scripted group (container) (typed FeaturePython)
  n = 1
  ref = O_element
FEATURE [App::DocumentObjectGroupPython] G4_DNA_GUANINE  # scripted group (container) (typed FeaturePython)
  Dunit = g/cm3
  Dvalue = 1
  Group = -> [H_element125,C_element135,N_element055,O_element116]
  conduct = 2
  density = 1
  expand = 3
  formula = G4_DNA_GUANINE
  name = G4_DNA_GUANINE
  specific = 4
FEATURE [App::DocumentObjectGroupPython] H_element126  label="H_element : 073"  # scripted group (container) (typed FeaturePython)
  n = 4
  ref = H_element
FEATURE [App::DocumentObjectGroupPython] C_element136  label="C_element : 081"  # scripted group (container) (typed FeaturePython)
  n = 4
  ref = C_element
FEATURE [App::DocumentObjectGroupPython] N_element056  label="N_element : 028"  # scripted group (container) (typed FeaturePython)
  n = 3
  ref = N_element
FEATURE [App::DocumentObjectGroupPython] O_element117  label="O_element : 070"  # scripted group (container) (typed FeaturePython)
  n = 1
  ref = O_element
FEATURE [App::DocumentObjectGroupPython] G4_DNA_CYTOSINE  # scripted group (container) (typed FeaturePython)
  Dunit = g/cm3
  Dvalue = 1
  Group = -> [H_element126,C_element136,N_element056,O_element117]
  conduct = 2
  density = 1
  expand = 3
  formula = G4_DNA_CYTOSINE
  name = G4_DNA_CYTOSINE
  specific = 4
FEATURE [App::DocumentObjectGroupPython] H_element127  label="H_element : 074"  # scripted group (container) (typed FeaturePython)
  n = 5
  ref = H_element
FEATURE [App::DocumentObjectGroupPython] C_element137  label="C_element : 082"  # scripted group (container) (typed FeaturePython)
  n = 5
  ref = C_element
FEATURE [App::DocumentObjectGroupPython] N_element057  label="N_element : 029"  # scripted group (container) (typed FeaturePython)
  n = 2
  ref = N_element
FEATURE [App::DocumentObjectGroupPython] O_element118  label="O_element : 071"  # scripted group (container) (typed FeaturePython)
  n = 2
  ref = O_element
FEATURE [App::DocumentObjectGroupPython] G4_DNA_THYMINE  # scripted group (container) (typed FeaturePython)
  Dunit = g/cm3
  Dvalue = 1
  Group = -> [H_element127,C_element137,N_element057,O_element118]
  conduct = 2
  density = 1
  expand = 3
  formula = G4_DNA_THYMINE
  name = G4_DNA_THYMINE
  specific = 4
FEATURE [App::DocumentObjectGroupPython] H_element128  label="H_element : 075"  # scripted group (container) (typed FeaturePython)
  n = 3
  ref = H_element
FEATURE [App::DocumentObjectGroupPython] C_element138  label="C_element : 083"  # scripted group (container) (typed FeaturePython)
  n = 4
  ref = C_element
FEATURE [App::DocumentObjectGroupPython] N_element058  label="N_element : 030"  # scripted group (container) (typed FeaturePython)
  n = 2
  ref = N_element
FEATURE [App::DocumentObjectGroupPython] O_element119  label="O_element : 072"  # scripted group (container) (typed FeaturePython)
  n = 2
  ref = O_element
FEATURE [App::DocumentObjectGroupPython] G4_DNA_URACIL  # scripted group (container) (typed FeaturePython)
  Dunit = g/cm3
  Dvalue = 1
  Group = -> [H_element128,C_element138,N_element058,O_element119]
  conduct = 2
  density = 1
  expand = 3
  formula = G4_DNA_URACIL
  name = G4_DNA_URACIL
  specific = 4
FEATURE [App::DocumentObjectGroupPython] H_element129  label="H_element : 076"  # scripted group (container) (typed FeaturePython)
  n = 10
  ref = H_element
FEATURE [App::DocumentObjectGroupPython] C_element139  label="C_element : 084"  # scripted group (container) (typed FeaturePython)
  n = 10
  ref = C_element
FEATURE [App::DocumentObjectGroupPython] N_element059  label="N_element : 031"  # scripted group (container) (typed FeaturePython)
  n = 5
  ref = N_element
FEATURE [App::DocumentObjectGroupPython] O_element120  label="O_element : 073"  # scripted group (container) (typed FeaturePython)
  n = 4
  ref = O_element
FEATURE [App::DocumentObjectGroupPython] G4_DNA_ADENOSINE  # scripted group (container) (typed FeaturePython)
  Dunit = g/cm3
  Dvalue = 1
  Group = -> [H_element129,C_element139,N_element059,O_element120]
  conduct = 2
  density = 1
  expand = 3
  formula = G4_DNA_ADENOSINE
  name = G4_DNA_ADENOSINE
  specific = 4
FEATURE [App::DocumentObjectGroupPython] H_element130  label="H_element : 077"  # scripted group (container) (typed FeaturePython)
  n = 10
  ref = H_element
FEATURE [App::DocumentObjectGroupPython] C_element140  label="C_element : 085"  # scripted group (container) (typed FeaturePython)
  n = 10
  ref = C_element
FEATURE [App::DocumentObjectGroupPython] N_element060  label="N_element : 032"  # scripted group (container) (typed FeaturePython)
  n = 5
  ref = N_element
FEATURE [App::DocumentObjectGroupPython] O_element121  label="O_element : 074"  # scripted group (container) (typed FeaturePython)
  n = 5
  ref = O_element
FEATURE [App::DocumentObjectGroupPython] G4_DNA_GUANOSINE  # scripted group (container) (typed FeaturePython)
  Dunit = g/cm3
  Dvalue = 1
  Group = -> [H_element130,C_element140,N_element060,O_element121]
  conduct = 2
  density = 1
  expand = 3
  formula = G4_DNA_GUANOSINE
  name = G4_DNA_GUANOSINE
  specific = 4
FEATURE [App::DocumentObjectGroupPython] H_element131  label="H_element : 078"  # scripted group (container) (typed FeaturePython)
  n = 10
  ref = H_element
FEATURE [App::DocumentObjectGroupPython] C_element141  label="C_element : 086"  # scripted group (container) (typed FeaturePython)
  n = 9
  ref = C_element
FEATURE [App::DocumentObjectGroupPython] N_element061  label="N_element : 033"  # scripted group (container) (typed FeaturePython)
  n = 3
  ref = N_element
FEATURE [App::DocumentObjectGroupPython] O_element122  label="O_element : 075"  # scripted group (container) (typed FeaturePython)
  n = 5
  ref = O_element
FEATURE [App::DocumentObjectGroupPython] G4_DNA_CYTIDINE  # scripted group (container) (typed FeaturePython)
  Dunit = g/cm3
  Dvalue = 1
  Group = -> [H_element131,C_element141,N_element061,O_element122]
  conduct = 2
  density = 1
  expand = 3
  formula = G4_DNA_CYTIDINE
  name = G4_DNA_CYTIDINE
  specific = 4
FEATURE [App::DocumentObjectGroupPython] H_element132  label="H_element : 079"  # scripted group (container) (typed FeaturePython)
  n = 9
  ref = H_element
FEATURE [App::DocumentObjectGroupPython] C_element142  label="C_element : 087"  # scripted group (container) (typed FeaturePython)
  n = 9
  ref = C_element
FEATURE [App::DocumentObjectGroupPython] N_element062  label="N_element : 034"  # scripted group (container) (typed FeaturePython)
  n = 2
  ref = N_element
FEATURE [App::DocumentObjectGroupPython] O_element123  label="O_element : 076"  # scripted group (container) (typed FeaturePython)
  n = 6
  ref = O_element
FEATURE [App::DocumentObjectGroupPython] G4_DNA_URIDINE  # scripted group (container) (typed FeaturePython)
  Dunit = g/cm3
  Dvalue = 1
  Group = -> [H_element132,C_element142,N_element062,O_element123]
  conduct = 2
  density = 1
  expand = 3
  formula = G4_DNA_URIDINE
  name = G4_DNA_URIDINE
  specific = 4
FEATURE [App::DocumentObjectGroupPython] H_element133  label="H_element : 080"  # scripted group (container) (typed FeaturePython)
  n = 11
  ref = H_element
FEATURE [App::DocumentObjectGroupPython] C_element143  label="C_element : 088"  # scripted group (container) (typed FeaturePython)
  n = 10
  ref = C_element
FEATURE [App::DocumentObjectGroupPython] N_element063  label="N_element : 035"  # scripted group (container) (typed FeaturePython)
  n = 2
  ref = N_element
FEATURE [App::DocumentObjectGroupPython] O_element124  label="O_element : 077"  # scripted group (container) (typed FeaturePython)
  n = 6
  ref = O_element
FEATURE [App::DocumentObjectGroupPython] G4_DNA_METHYLURIDINE  # scripted group (container) (typed FeaturePython)
  Dunit = g/cm3
  Dvalue = 1
  Group = -> [H_element133,C_element143,N_element063,O_element124]
  conduct = 2
  density = 1
  expand = 3
  formula = G4_DNA_METHYLURIDINE
  name = G4_DNA_METHYLURIDINE
  specific = 4
FEATURE [App::DocumentObjectGroupPython] P_element014  label="P_element : 003"  # scripted group (container) (typed FeaturePython)
  n = 1
  ref = P_element
FEATURE [App::DocumentObjectGroupPython] O_element125  label="O_element : 078"  # scripted group (container) (typed FeaturePython)
  n = 3
  ref = O_element
FEATURE [App::DocumentObjectGroupPython] G4_DNA_MONOPHOSPHATE  # scripted group (container) (typed FeaturePython)
  Dunit = g/cm3
  Dvalue = 1
  Group = -> [P_element014,O_element125]
  conduct = 2
  density = 1
  expand = 3
  formula = G4_DNA_MONOPHOSPHATE
  name = G4_DNA_MONOPHOSPHATE
  specific = 4
FEATURE [App::DocumentObjectGroupPython] H_element134  label="H_element : 081"  # scripted group (container) (typed FeaturePython)
  n = 10
  ref = H_element
FEATURE [App::DocumentObjectGroupPython] C_element144  label="C_element : 089"  # scripted group (container) (typed FeaturePython)
  n = 10
  ref = C_element
FEATURE [App::DocumentObjectGroupPython] N_element064  label="N_element : 036"  # scripted group (container) (typed FeaturePython)
  n = 5
  ref = N_element
FEATURE [App::DocumentObjectGroupPython] O_element126  label="O_element : 079"  # scripted group (container) (typed FeaturePython)
  n = 7
  ref = O_element
FEATURE [App::DocumentObjectGroupPython] P_element015  label="P_element : 004"  # scripted group (container) (typed FeaturePython)
  n = 1
  ref = P_element
FEATURE [App::DocumentObjectGroupPython] G4_DNA_A  # scripted group (container) (typed FeaturePython)
  Dunit = g/cm3
  Dvalue = 1
  Group = -> [H_element134,C_element144,N_element064,O_element126,P_element015]
  conduct = 2
  density = 1
  expand = 3
  formula = G4_DNA_A
  name = G4_DNA_A
  specific = 4
FEATURE [App::DocumentObjectGroupPython] H_element135  label="H_element : 082"  # scripted group (container) (typed FeaturePython)
  n = 10
  ref = H_element
FEATURE [App::DocumentObjectGroupPython] C_element145  label="C_element : 090"  # scripted group (container) (typed FeaturePython)
  n = 10
  ref = C_element
FEATURE [App::DocumentObjectGroupPython] N_element065  label="N_element : 037"  # scripted group (container) (typed FeaturePython)
  n = 5
  ref = N_element
FEATURE [App::DocumentObjectGroupPython] O_element127  label="O_element : 8"  # scripted group (container) (typed FeaturePython)
  n = 8
  ref = O_element
FEATURE [App::DocumentObjectGroupPython] P_element016  label="P_element : 005"  # scripted group (container) (typed FeaturePython)
  n = 1
  ref = P_element
FEATURE [App::DocumentObjectGroupPython] G4_DNA_G  # scripted group (container) (typed FeaturePython)
  Dunit = g/cm3
  Dvalue = 1
  Group = -> [H_element135,C_element145,N_element065,O_element127,P_element016]
  conduct = 2
  density = 1
  expand = 3
  formula = G4_DNA_G
  name = G4_DNA_G
  specific = 4
FEATURE [App::DocumentObjectGroupPython] H_element136  label="H_element : 083"  # scripted group (container) (typed FeaturePython)
  n = 10
  ref = H_element
FEATURE [App::DocumentObjectGroupPython] C_element146  label="C_element : 091"  # scripted group (container) (typed FeaturePython)
  n = 9
  ref = C_element
FEATURE [App::DocumentObjectGroupPython] N_element066  label="N_element : 038"  # scripted group (container) (typed FeaturePython)
  n = 3
  ref = N_element
FEATURE [App::DocumentObjectGroupPython] O_element128  label="O_element : 080"  # scripted group (container) (typed FeaturePython)
  n = 8
  ref = O_element
FEATURE [App::DocumentObjectGroupPython] P_element017  label="P_element : 006"  # scripted group (container) (typed FeaturePython)
  n = 1
  ref = P_element
FEATURE [App::DocumentObjectGroupPython] G4_DNA_C  # scripted group (container) (typed FeaturePython)
  Dunit = g/cm3
  Dvalue = 1
  Group = -> [H_element136,C_element146,N_element066,O_element128,P_element017]
  conduct = 2
  density = 1
  expand = 3
  formula = G4_DNA_C
  name = G4_DNA_C
  specific = 4
FEATURE [App::DocumentObjectGroupPython] H_element137  label="H_element : 084"  # scripted group (container) (typed FeaturePython)
  n = 9
  ref = H_element
FEATURE [App::DocumentObjectGroupPython] C_element147  label="C_element : 092"  # scripted group (container) (typed FeaturePython)
  n = 9
  ref = C_element
FEATURE [App::DocumentObjectGroupPython] N_element067  label="N_element : 039"  # scripted group (container) (typed FeaturePython)
  n = 2
  ref = N_element
FEATURE [App::DocumentObjectGroupPython] O_element129  label="O_element : 9"  # scripted group (container) (typed FeaturePython)
  n = 9
  ref = O_element
FEATURE [App::DocumentObjectGroupPython] P_element018  label="P_element : 007"  # scripted group (container) (typed FeaturePython)
  n = 1
  ref = P_element
FEATURE [App::DocumentObjectGroupPython] G4_DNA_U  # scripted group (container) (typed FeaturePython)
  Dunit = g/cm3
  Dvalue = 1
  Group = -> [H_element137,C_element147,N_element067,O_element129,P_element018]
  conduct = 2
  density = 1
  expand = 3
  formula = G4_DNA_U
  name = G4_DNA_U
  specific = 4
FEATURE [App::DocumentObjectGroupPython] H_element138  label="H_element : 085"  # scripted group (container) (typed FeaturePython)
  n = 11
  ref = H_element
FEATURE [App::DocumentObjectGroupPython] C_element148  label="C_element : 093"  # scripted group (container) (typed FeaturePython)
  n = 10
  ref = C_element
FEATURE [App::DocumentObjectGroupPython] N_element068  label="N_element : 040"  # scripted group (container) (typed FeaturePython)
  n = 2
  ref = N_element
FEATURE [App::DocumentObjectGroupPython] O_element130  label="O_element : 081"  # scripted group (container) (typed FeaturePython)
  n = 9
  ref = O_element
FEATURE [App::DocumentObjectGroupPython] P_element019  label="P_element : 008"  # scripted group (container) (typed FeaturePython)
  n = 1
  ref = P_element
FEATURE [App::DocumentObjectGroupPython] G4_DNA_MU  # scripted group (container) (typed FeaturePython)
  Dunit = g/cm3
  Dvalue = 1
  Group = -> [H_element138,C_element148,N_element068,O_element130,P_element019]
  conduct = 2
  density = 1
  expand = 3
  formula = G4_DNA_MU
  name = G4_DNA_MU
  specific = 4
FEATURE [App::DocumentObjectGroupPython] BioChemical  # scripted group (container) (typed FeaturePython)
  Group = -> [G4_CYTOSINE,G4_THYMINE,G4_URACIL,G4_DNA_ADENINE,G4_DNA_GUANINE,G4_DNA_CYTOSINE,G4_DNA_THYMINE,G4_DNA_URACIL,G4_DNA_ADENOSINE,G4_DNA_GUANOSINE,G4_DNA_CYTIDINE,G4_DNA_URIDINE,G4_DNA_METHYLURIDINE,G4_DNA_MONOPHOSPHATE,G4_DNA_A,G4_DNA_G,G4_DNA_C,G4_DNA_U,G4_DNA_MU]
FEATURE [App::DocumentObjectGroupPython] G4Materials  # scripted group (container) (typed FeaturePython)
  Group = -> [NIST,Element,HEP,Space,BioChemical]
  version = 1
FEATURE [App::DocumentObjectGroupPython] Geant4  # scripted group (container) (typed FeaturePython)
  Group = -> [G4Isotopes,G4Elements,G4Materials]
FEATURE [App::DocumentObjectGroupPython] Materials  # scripted group (container) (typed FeaturePython)
  Group = -> [Geant4]
FEATURE [Part::FeaturePython] GDMLBox_WorldBox  # WARN: FeaturePython — macro-defined, semantics opaque (R4)
  lunit = 2
  material = 5
  x = 20
  y = 20
  z = 20
FEATURE [Sketcher::SketchObject] Sketch
  FullyConstrained = false
  sketch-geometry (4):
    g0: ArcOfCircle CenterX=0 CenterY=0 CenterZ=0 NormalX=0 NormalY=0 NormalZ=1 AngleXU=0 Radius=5.61268 StartAngle=0 EndAngle=3.14159
    g1: LineSegment StartX=5.61268 StartY=0 StartZ=0 EndX=0.046736 EndY=1.79644 EndZ=0
    g2: LineSegment StartX=0.046736 StartY=1.79644 StartZ=0 EndX=-1.78598 EndY=-2.14051 EndZ=0
    g3: LineSegment StartX=-1.78598 StartY=-2.14051 StartZ=0 EndX=-5.61268 EndY=9e-16 EndZ=0
  constraints (7):
    c: Coincident(g0,g-1)
    c: PointOnObject(g0,g-1)
    c: PointOnObject(g0,g-1)
    c: Coincident(g0,g1)
    c: Coincident(g1,g2)
    c: Coincident(g2,g3)
    c: Coincident(g3,g0)
FEATURE [Part::Extrusion] Extrude
  Base = -> Sketch
  Dir = (0,0,1)
  DirMode = 2
  FaceMakerClass = Part::FaceMakerBullseye
  LengthFwd = 10
  LengthRev = 0
  Solid = true
  Symmetric = false
FEATURE [App::Part] Part
  Group = -> [Sketch,Extrude]
  Origin = -> Origin001
FEATURE [App::Part] worldVOL
  Group = -> [GDMLBox_WorldBox,Part]
  Origin = -> Origin
